FCSTD DOCUMENT  (FreeCAD 0.20R29410 (Git))
Label: step2-sketch-plates-freecad
License: All rights reserved
LicenseURL: http://en.wikipedia.org/wiki/All_rights_reserved
objects: Sketcher::SketchObject×4
note: 4 computed .brp shape members not serialized (recipe doc carries the construction recipe); baked Part::Feature solids carry a one-line shape summary decoded from their .brp

FEATURE [Sketcher::SketchObject] Sketch004  label="bottom-plates"
  FullyConstrained = false
  sketch-geometry (112):
    g0: LineSegment StartX=92.1533 StartY=-3.22906 StartZ=0 EndX=109.153 EndY=-3.22906 EndZ=0
    g1: ArcOfCircle CenterX=109.153 CenterY=-5.22906 CenterZ=0 NormalX=0 NormalY=0 NormalZ=1 AngleXU=0 Radius=2 StartAngle=0 EndAngle=1.5708
    g2: LineSegment StartX=111.153 StartY=-5.22906 StartZ=0 EndX=111.153 EndY=-6.07906 EndZ=0
    g3: ArcOfCircle CenterX=113.153 CenterY=-6.07906 CenterZ=0 NormalX=0 NormalY=0 NormalZ=1 AngleXU=0 Radius=2 StartAngle=3.14159 EndAngle=4.71239
    g4: LineSegment StartX=113.153 StartY=-8.07906 StartZ=0 EndX=128.153 EndY=-8.07906 EndZ=0
    g5: ArcOfCircle CenterX=128.153 CenterY=-10.0791 CenterZ=0 NormalX=0 NormalY=0 NormalZ=1 AngleXU=0 Radius=2 StartAngle=0 EndAngle=1.5708
    g6: LineSegment StartX=130.153 StartY=-10.0791 StartZ=0 EndX=130.153 EndY=-18.0791 EndZ=0
    g7: ArcOfCircle CenterX=132.153 CenterY=-18.0791 CenterZ=0 NormalX=0 NormalY=0 NormalZ=1 AngleXU=0 Radius=2 StartAngle=3.14159 EndAngle=4.71239
    g8: LineSegment StartX=132.153 StartY=-20.0791 StartZ=0 EndX=147.153 EndY=-20.0791 EndZ=0
    g9: ArcOfCircle CenterX=147.153 CenterY=-22.0791 CenterZ=0 NormalX=0 NormalY=0 NormalZ=1 AngleXU=0 Radius=2 StartAngle=0 EndAngle=1.5708
    g10: LineSegment StartX=149.153 StartY=-22.0791 StartZ=0 EndX=149.153 EndY=-77.0791 EndZ=0
    g11: ArcOfCircle CenterX=147.153 CenterY=-77.0791 CenterZ=0 NormalX=0 NormalY=0 NormalZ=1 AngleXU=0 Radius=2 StartAngle=4.71239 EndAngle=6.28319
    g12: LineSegment StartX=147.153 StartY=-79.0791 StartZ=0 EndX=130.153 EndY=-79.0791 EndZ=0
    g13: ArcOfCircle CenterX=130.153 CenterY=-81.0791 CenterZ=0 NormalX=0 NormalY=0 NormalZ=1 AngleXU=0 Radius=2 StartAngle=1.5708 EndAngle=3.14159
    g14: LineSegment StartX=128.153 StartY=-81.0791 StartZ=0 EndX=128.153 EndY=-82.0791 EndZ=0
    g15: ArcOfCircle CenterX=126.653 CenterY=-82.0791 CenterZ=0 NormalX=0 NormalY=0 NormalZ=1 AngleXU=0 Radius=1.5 StartAngle=4.71239 EndAngle=6.28319
    g16: LineSegment StartX=126.653 StartY=-83.5791 StartZ=0 EndX=88.1533 EndY=-83.5791 EndZ=0
    g17: ArcOfCircle CenterX=88.1533 CenterY=-85.5791 CenterZ=0 NormalX=0 NormalY=0 NormalZ=1 AngleXU=0 Radius=2 StartAngle=1.5708 EndAngle=3.14159
    g18: LineSegment StartX=86.1533 StartY=-85.5791 StartZ=0 EndX=86.1533 EndY=-88.5791 EndZ=0
    g19: ArcOfCircle CenterX=84.1533 CenterY=-88.5791 CenterZ=0 NormalX=0 NormalY=0 NormalZ=1 AngleXU=0 Radius=2 StartAngle=4.71239 EndAngle=6.28319
    g20: Circle CenterX=18.6533 CenterY=-59.0791 CenterZ=0 NormalX=0 NormalY=0 NormalZ=-1 AngleXU=0 Radius=1.1
    g21: LineSegment StartX=12.6533 StartY=-75.5791 StartZ=0 EndX=12.6533 EndY=-10.0791 EndZ=0
    g22: ArcOfCircle CenterX=14.6533 CenterY=-10.0791 CenterZ=0 NormalX=0 NormalY=0 NormalZ=1 AngleXU=0 Radius=2 StartAngle=1.5708 EndAngle=3.14159
    g23: LineSegment StartX=14.6533 StartY=-8.07906 StartZ=0 EndX=88.1533 EndY=-8.07906 EndZ=0
    g24: ArcOfCircle CenterX=88.1533 CenterY=-6.07906 CenterZ=0 NormalX=0 NormalY=0 NormalZ=1 AngleXU=0 Radius=2 StartAngle=4.71239 EndAngle=6.28319
    g25: LineSegment StartX=90.1533 StartY=-6.07906 StartZ=0 EndX=90.1533 EndY=-5.22906 EndZ=0
    g26: ArcOfCircle CenterX=92.1533 CenterY=-5.22906 CenterZ=0 NormalX=0 NormalY=0 NormalZ=1 AngleXU=0 Radius=2 StartAngle=1.5708 EndAngle=3.14159
    g27: ArcOfCircle CenterX=26.7587 CenterY=-99.1946 CenterZ=0 NormalX=0 NormalY=0 NormalZ=1 AngleXU=0 Radius=3.4 StartAngle=3.56097 EndAngle=4.80802
    g28: Circle CenterX=50.1533 CenterY=-11.5791 CenterZ=0 NormalX=0 NormalY=0 NormalZ=-1 AngleXU=0 Radius=1.1
    g29: LineSegment StartX=13.6533 StartY=-79.5791 StartZ=0 EndX=23.6533 EndY=-100.579 EndZ=0
    g30: Circle CenterX=50.1533 CenterY=-59.0791 CenterZ=0 NormalX=0 NormalY=0 NormalZ=-1 AngleXU=0 Radius=1.1
    g31: ArcOfCircle CenterX=77.65 CenterY=-201.358 CenterZ=0 NormalX=0 NormalY=0 NormalZ=1 AngleXU=0 Radius=110.97 StartAngle=1.51216 EndAngle=2.04393
    g32: Circle CenterX=129.153 CenterY=-21.0791 CenterZ=0 NormalX=0 NormalY=0 NormalZ=-1 AngleXU=0 Radius=1.1
    g33: ArcOfCircle CenterX=22.8742 CenterY=-75.1488 CenterZ=0 NormalX=0 NormalY=0 NormalZ=1 AngleXU=0 Radius=10.23 StartAngle=3.18366 EndAngle=3.58948
    g34: Circle CenterX=42.1533 CenterY=-85.0791 CenterZ=0 NormalX=0 NormalY=0 NormalZ=-1 AngleXU=0 Radius=1.1
    g35: Circle CenterX=127.653 CenterY=-77.5791 CenterZ=0 NormalX=0 NormalY=0 NormalZ=-1 AngleXU=0 Radius=1.1
    g36: Circle CenterX=50.1533 CenterY=-31.0791 CenterZ=0 NormalX=0 NormalY=0 NormalZ=-1 AngleXU=0 Radius=1.1
    g37: Circle CenterX=18.6533 CenterY=-31.0791 CenterZ=0 NormalX=0 NormalY=0 NormalZ=-1 AngleXU=0 Radius=1.1
    g38: GeomPoint X=18.6533 Y=-80.4791 Z=0
    g39: GeomPoint X=18.6533 Y=-11.5791 Z=0
    g40: LineSegment StartX=20.3854 StartY=-80.4791 StartZ=0 EndX=19.5193 EndY=-78.9791 EndZ=0
    g41: LineSegment StartX=19.5193 StartY=-78.9791 StartZ=0 EndX=17.7873 EndY=-78.9791 EndZ=0
    g42: LineSegment StartX=17.7873 StartY=-78.9791 StartZ=0 EndX=16.9212 EndY=-80.4791 EndZ=0
    g43: LineSegment StartX=16.9212 StartY=-80.4791 StartZ=0 EndX=17.7873 EndY=-81.9791 EndZ=0
    g44: LineSegment StartX=17.7873 StartY=-81.9791 StartZ=0 EndX=19.5193 EndY=-81.9791 EndZ=0
    g45: LineSegment StartX=19.5193 StartY=-81.9791 StartZ=0 EndX=20.3854 EndY=-80.4791 EndZ=0
    g46: Circle CenterX=18.6533 CenterY=-80.4791 CenterZ=0 NormalX=0 NormalY=0 NormalZ=1 AngleXU=0 Radius=1.73205
    g47: LineSegment StartX=20.3854 StartY=-11.5791 StartZ=0 EndX=19.5193 EndY=-10.0791 EndZ=0
    g48: LineSegment StartX=19.5193 StartY=-10.0791 StartZ=0 EndX=17.7873 EndY=-10.0791 EndZ=0
    g49: LineSegment StartX=17.7873 StartY=-10.0791 StartZ=0 EndX=16.9212 EndY=-11.5791 EndZ=0
    g50: LineSegment StartX=16.9212 StartY=-11.5791 StartZ=0 EndX=17.7873 EndY=-13.0791 EndZ=0
    g51: LineSegment StartX=17.7873 StartY=-13.0791 StartZ=0 EndX=19.5193 EndY=-13.0791 EndZ=0
    g52: LineSegment StartX=19.5193 StartY=-13.0791 StartZ=0 EndX=20.3854 EndY=-11.5791 EndZ=0
    g53: Circle CenterX=18.6533 CenterY=-11.5791 CenterZ=0 NormalX=0 NormalY=0 NormalZ=1 AngleXU=0 Radius=1.73205
    g54: LineSegment StartX=-92.1533 StartY=-3.22906 StartZ=0 EndX=-109.153 EndY=-3.22906 EndZ=0
    g55: ArcOfCircle CenterX=-109.153 CenterY=-5.22906 CenterZ=0 NormalX=0 NormalY=0 NormalZ=1 AngleXU=0 Radius=2 StartAngle=1.5708 EndAngle=3.14159
    g56: LineSegment StartX=-111.153 StartY=-5.22906 StartZ=0 EndX=-111.153 EndY=-6.07906 EndZ=0
    g57: ArcOfCircle CenterX=-113.153 CenterY=-6.07906 CenterZ=0 NormalX=0 NormalY=0 NormalZ=1 AngleXU=0 Radius=2 StartAngle=4.71239 EndAngle=6.28319
    g58: LineSegment StartX=-113.153 StartY=-8.07906 StartZ=0 EndX=-128.153 EndY=-8.07906 EndZ=0
    g59: ArcOfCircle CenterX=-128.153 CenterY=-10.0791 CenterZ=0 NormalX=0 NormalY=0 NormalZ=1 AngleXU=0 Radius=2 StartAngle=1.5708 EndAngle=3.14159
    g60: LineSegment StartX=-130.153 StartY=-10.0791 StartZ=0 EndX=-130.153 EndY=-18.0791 EndZ=0
    g61: ArcOfCircle CenterX=-132.153 CenterY=-18.0791 CenterZ=0 NormalX=0 NormalY=0 NormalZ=1 AngleXU=0 Radius=2 StartAngle=4.71239 EndAngle=6.28319
    g62: LineSegment StartX=-132.153 StartY=-20.0791 StartZ=0 EndX=-147.153 EndY=-20.0791 EndZ=0
    g63: ArcOfCircle CenterX=-147.153 CenterY=-22.0791 CenterZ=0 NormalX=0 NormalY=0 NormalZ=1 AngleXU=0 Radius=2 StartAngle=1.5708 EndAngle=3.14159
    g64: LineSegment StartX=-149.153 StartY=-22.0791 StartZ=0 EndX=-149.153 EndY=-77.0791 EndZ=0
    g65: ArcOfCircle CenterX=-147.153 CenterY=-77.0791 CenterZ=0 NormalX=0 NormalY=0 NormalZ=1 AngleXU=0 Radius=2 StartAngle=3.14159 EndAngle=4.71239
    g66: LineSegment StartX=-147.153 StartY=-79.0791 StartZ=0 EndX=-130.153 EndY=-79.0791 EndZ=0
    g67: ArcOfCircle CenterX=-130.153 CenterY=-81.0791 CenterZ=0 NormalX=0 NormalY=0 NormalZ=1 AngleXU=0 Radius=2 StartAngle=0 EndAngle=1.5708
    g68: LineSegment StartX=-128.153 StartY=-81.0791 StartZ=0 EndX=-128.153 EndY=-82.0791 EndZ=0
    g69: ArcOfCircle CenterX=-126.653 CenterY=-82.0791 CenterZ=0 NormalX=0 NormalY=0 NormalZ=1 AngleXU=0 Radius=1.5 StartAngle=3.14159 EndAngle=4.71239
    g70: LineSegment StartX=-126.653 StartY=-83.5791 StartZ=0 EndX=-88.1533 EndY=-83.5791 EndZ=0
    g71: ArcOfCircle CenterX=-88.1533 CenterY=-85.5791 CenterZ=0 NormalX=0 NormalY=0 NormalZ=1 AngleXU=0 Radius=2 StartAngle=0 EndAngle=1.5708
    g72: LineSegment StartX=-86.1533 StartY=-85.5791 StartZ=0 EndX=-86.1533 EndY=-88.5791 EndZ=0
    g73: ArcOfCircle CenterX=-84.1533 CenterY=-88.5791 CenterZ=0 NormalX=0 NormalY=0 NormalZ=1 AngleXU=0 Radius=2 StartAngle=3.14159 EndAngle=4.71239
    g74: Circle CenterX=-18.6533 CenterY=-59.0791 CenterZ=0 NormalX=0 NormalY=0 NormalZ=-1 AngleXU=0 Radius=1.1
    g75: LineSegment StartX=-12.6533 StartY=-75.5791 StartZ=0 EndX=-12.6533 EndY=-10.0791 EndZ=0
    g76: ArcOfCircle CenterX=-14.6533 CenterY=-10.0791 CenterZ=0 NormalX=0 NormalY=0 NormalZ=1 AngleXU=0 Radius=2 StartAngle=0 EndAngle=1.5708
    g77: LineSegment StartX=-14.6533 StartY=-8.07906 StartZ=0 EndX=-88.1533 EndY=-8.07906 EndZ=0
    g78: ArcOfCircle CenterX=-88.1533 CenterY=-6.07906 CenterZ=0 NormalX=0 NormalY=0 NormalZ=1 AngleXU=0 Radius=2 StartAngle=3.14159 EndAngle=4.71239
    g79: LineSegment StartX=-90.1533 StartY=-6.07906 StartZ=0 EndX=-90.1533 EndY=-5.22906 EndZ=0
    g80: ArcOfCircle CenterX=-92.1533 CenterY=-5.22906 CenterZ=0 NormalX=0 NormalY=0 NormalZ=1 AngleXU=0 Radius=2 StartAngle=0 EndAngle=1.5708
    g81: ArcOfCircle CenterX=-26.7587 CenterY=-99.1946 CenterZ=0 NormalX=0 NormalY=0 NormalZ=1 AngleXU=0 Radius=3.4 StartAngle=4.61676 EndAngle=5.8638
    g82: Circle CenterX=-50.1533 CenterY=-11.5791 CenterZ=0 NormalX=0 NormalY=0 NormalZ=-1 AngleXU=0 Radius=1.1
    g83: LineSegment StartX=-13.6533 StartY=-79.5791 StartZ=0 EndX=-23.6533 EndY=-100.579 EndZ=0
    g84: Circle CenterX=-50.1533 CenterY=-59.0791 CenterZ=0 NormalX=0 NormalY=0 NormalZ=-1 AngleXU=0 Radius=1.1
    g85: ArcOfCircle CenterX=-77.65 CenterY=-201.358 CenterZ=0 NormalX=0 NormalY=0 NormalZ=1 AngleXU=0 Radius=110.97 StartAngle=1.09766 EndAngle=1.62943
    g86: Circle CenterX=-129.153 CenterY=-21.0791 CenterZ=0 NormalX=0 NormalY=0 NormalZ=-1 AngleXU=0 Radius=1.1
    g87: ArcOfCircle CenterX=-22.8742 CenterY=-75.1488 CenterZ=0 NormalX=0 NormalY=0 NormalZ=1 AngleXU=0 Radius=10.23 StartAngle=5.8353 EndAngle=6.24112
    g88: Circle CenterX=-42.1533 CenterY=-85.0791 CenterZ=0 NormalX=0 NormalY=0 NormalZ=-1 AngleXU=0 Radius=1.1
    g89: LineSegment StartX=-31.0333 StartY=-19.7091 StartZ=0 EndX=-40.2733 EndY=-19.7091 EndZ=0
    g90: LineSegment StartX=-40.2733 StartY=-19.7091 StartZ=0 EndX=-40.2733 EndY=-28.0791 EndZ=0
    g91: LineSegment StartX=-40.2733 StartY=-28.0791 StartZ=0 EndX=-31.0333 EndY=-28.0791 EndZ=0
    g92: LineSegment StartX=-31.0333 StartY=-28.0791 StartZ=0 EndX=-31.0333 EndY=-19.7091 EndZ=0
    g93: Circle CenterX=-127.653 CenterY=-77.5791 CenterZ=0 NormalX=0 NormalY=0 NormalZ=-1 AngleXU=0 Radius=1.1
    g94: Circle CenterX=-50.1533 CenterY=-31.0791 CenterZ=0 NormalX=0 NormalY=0 NormalZ=-1 AngleXU=0 Radius=1.1
    g95: Circle CenterX=-18.6533 CenterY=-31.0791 CenterZ=0 NormalX=0 NormalY=0 NormalZ=-1 AngleXU=0 Radius=1.1
    g96: GeomPoint X=-18.6533 Y=-80.4791 Z=0
    g97: GeomPoint X=-18.6533 Y=-11.5791 Z=0
    g98: LineSegment StartX=-20.3854 StartY=-80.4791 StartZ=0 EndX=-19.5193 EndY=-78.9791 EndZ=0
    g99: LineSegment StartX=-19.5193 StartY=-78.9791 StartZ=0 EndX=-17.7873 EndY=-78.9791 EndZ=0
    g100: LineSegment StartX=-17.7873 StartY=-78.9791 StartZ=0 EndX=-16.9212 EndY=-80.4791 EndZ=0
    g101: LineSegment StartX=-16.9212 StartY=-80.4791 StartZ=0 EndX=-17.7873 EndY=-81.9791 EndZ=0
    g102: LineSegment StartX=-17.7873 StartY=-81.9791 StartZ=0 EndX=-19.5193 EndY=-81.9791 EndZ=0
    g103: LineSegment StartX=-19.5193 StartY=-81.9791 StartZ=0 EndX=-20.3854 EndY=-80.4791 EndZ=0
    g104: Circle CenterX=-18.6533 CenterY=-80.4791 CenterZ=0 NormalX=0 NormalY=0 NormalZ=1 AngleXU=0 Radius=1.73205
    g105: LineSegment StartX=-20.3854 StartY=-11.5791 StartZ=0 EndX=-19.5193 EndY=-10.0791 EndZ=0
    g106: LineSegment StartX=-19.5193 StartY=-10.0791 StartZ=0 EndX=-17.7873 EndY=-10.0791 EndZ=0
    g107: LineSegment StartX=-17.7873 StartY=-10.0791 StartZ=0 EndX=-16.9212 EndY=-11.5791 EndZ=0
    g108: LineSegment StartX=-16.9212 StartY=-11.5791 StartZ=0 EndX=-17.7873 EndY=-13.0791 EndZ=0
    g109: LineSegment StartX=-17.7873 StartY=-13.0791 StartZ=0 EndX=-19.5193 EndY=-13.0791 EndZ=0
    g110: LineSegment StartX=-19.5193 StartY=-13.0791 StartZ=0 EndX=-20.3854 EndY=-11.5791 EndZ=0
    g111: Circle CenterX=-18.6533 CenterY=-11.5791 CenterZ=0 NormalX=0 NormalY=0 NormalZ=1 AngleXU=0 Radius=1.73205
  constraints (267):
    c: Coincident(g0,g1)
    c: Coincident(g1,g2)
    c: Vertical(g2)
    c: Coincident(g2,g3)
    c: Coincident(g3,g4)
    c: Horizontal(g4)
    c: Coincident(g4,g5)
    c: Coincident(g5,g6)
    c: Vertical(g6)
    c: Coincident(g6,g7)
    c: Coincident(g7,g8)
    c: Horizontal(g8)
    c: Coincident(g9,g10)
    c: Vertical(g10)
    c: Coincident(g10,g11)
    c: Horizontal(g12)
    c: Coincident(g12,g13)
    c: Coincident(g13,g14)
    c: Vertical(g14)
    c: Coincident(g14,g15)
    c: Coincident(g15,g16)
    c: Horizontal(g16)
    c: Coincident(g16,g17)
    c: Coincident(g17,g18)
    c: Vertical(g18)
    c: Coincident(g18,g19)
    c: Vertical(g21)
    c: Coincident(g21,g22)
    c: Horizontal(g23)
    c: Coincident(g23,g24)
    c: Coincident(g24,g25)
    c: Vertical(g25)
    c: Coincident(g25,g26)
    c: Horizontal(g23,g4)
    c: DistanceY(g27,g29) = 21
    c: DistanceY(g21,g21) = 65.5
    c: Radius(g15) = 1.5
    c: Radius(g1) = 2
    c: Equal(g26,g24)
    c: Coincident(g21,g33)
    c: Coincident(g29,g33)
    c: Coincident(g27,g29)
    c: Coincident(g27,g31)
    c: Coincident(g19,g31)
    c: Radius(g31) = 110.97
    c: Coincident(g0,g26)
    c: Coincident(g22,g23)
    c: Vertical(g38,g39)
    c: Coincident(g40,g41)
    c: Coincident(g41,g42)
    c: Coincident(g42,g43)
    c: Coincident(g43,g44)
    c: Coincident(g44,g45)
    c: Coincident(g45,g40)
    c: Equal(g40, g41-g45) x5
    c: PointOnObject(g40,g46)
    c: PointOnObject(g41,g46)
    c: PointOnObject(g42,g46)
    c: PointOnObject(g43,g46)
    c: PointOnObject(g44,g46)
    c: PointOnObject(g45,g46)
    c: Horizontal(g41)
    c: Coincident(g47,g48)
    c: Coincident(g48,g49)
    c: Coincident(g49,g50)
    c: Coincident(g50,g51)
    c: Coincident(g51,g52)
    c: Coincident(g52,g47)
    c: Equal(g47, g48-g52) x5
    c: PointOnObject(g47,g53)
    c: PointOnObject(g48,g53)
    c: PointOnObject(g49,g53)
    c: PointOnObject(g50,g53)
    c: PointOnObject(g51,g53)
    c: PointOnObject(g52,g53)
    c: Distance(g49,g47) = 3
    c: Equal(g41,g52)
    c: Horizontal(g48)
    c: Coincident(g39,g53)
    c: DistanceX(g21,g39) = 6
    c: DistanceY(g39,g22) = 3.5
    c: Coincident(g38,g46)
    c: Radius(g33) = 10.23
    c: Radius(g27) = 3.4
    c: Equal(g19,g17)
    c: DistanceY(g8,g4) = 12
    c: DistanceY(g11,g8) = 59
    c: DistanceY(g15,g12) = 4.5
    c: DistanceY(g29,g21) = 4
    c: DistanceX(g27,g27) = 3.43
    c: Equal(g1,g26)
    c: Equal(g5,g3)
    c: Equal(g3,g24)
    c: Equal(g9,g7)
    c: Equal(g7,g1)
    c: Equal(g17,g11)
    c: Equal(g11,g13)
    c: Equal(g13,g9)
    c: Equal(g22,g26)
    c: Horizontal(g0)
    c: Vertical(g22,g22)
    c: Horizontal(g21,g22)
    c: Vertical(g24,g23)
    c: Horizontal(g24,g24)
    c: Horizontal(g26,g25)
    c: Vertical(g0,g26)
    c: Vertical(g0,g1)
    c: Horizontal(g1,g1)
    c: Horizontal(g2,g3)
    c: Vertical(g3,g3)
    c: Vertical(g4,g5)
    c: Horizontal(g5,g5)
    c: Horizontal(g6,g7)
    c: Vertical(g7,g7)
    c: Vertical(g8,g9)
    c: Horizontal(g9,g9)
    c: Horizontal(g10,g11)
    c: Vertical(g11,g11)
    c: Vertical(g13,g12)
    c: Horizontal(g13,g13)
    c: Horizontal(g14,g15)
    c: Vertical(g15,g15)
    c: Vertical(g16,g17)
    c: Horizontal(g17,g17)
    c: Horizontal(g19,g18)
    c: Vertical(g19,g19)
    c: DistanceY(g27,g27) = 2
    c: DistanceY(g27,g19) = 12
    c: Horizontal(g39,g28)
    c: DistanceX(g39,g28) = 31.5
    c: Vertical(g28,g36)
    c: Vertical(g36,g30)
    c: DistanceY(g36,g28) = 19.5
    c: DistanceY(g30,g36) = 28
    c: DistanceY(g34,g30) = 26
    c: DistanceY(g38,g20) = 21.4
    c: DistanceX(g34,g30) = 8
    c: DistanceY(g32,g7) = 3
    c: DistanceX(g32,g7) = 3
    c: DistanceX(g35,g13) = 2.5
    c: DistanceY(g13,g35) = 3.5
    c: DistanceX(g14,g10) = 21
    c: DistanceX(g27,g18) = 62.5
    c: DistanceX(g18,g14) = 42
    c: Horizontal(g20,g30)
    c: Vertical(g20,g37)
    c: Vertical(g37,g39)
    c: Equal(g28,g36)
    c: Equal(g28,g30)
    c: Equal(g28,g20)
    c: Equal(g28,g37)
    c: Equal(g28,g34)
    c: Diameter(g28) = 2.2
    c: DistanceX(g22,g24) = 73.5
    c: DistanceX(g24,g3) = 25
    c: DistanceX(g3,g5) = 15
    c: DistanceX(g5,g9) = 19
    c: DistanceY(g3,g1) = 0.85
    c: Coincident(g8,g9)
    c: DistanceX(g21,g29) = 1
    c: Horizontal(g37,g36)
    c: Coincident(g12,g11)
    c: Coincident(g54,g55)
    c: Coincident(g55,g56)
    c: Vertical(g56)
    c: Coincident(g56,g57)
    c: Coincident(g57,g58)
    c: Horizontal(g58)
    c: Coincident(g58,g59)
    c: Coincident(g59,g60)
    c: Vertical(g60)
    c: Coincident(g60,g61)
    c: Coincident(g61,g62)
    c: Horizontal(g62)
    c: Coincident(g63,g64)
    c: Vertical(g64)
    c: Coincident(g64,g65)
    c: Horizontal(g66)
    c: Coincident(g66,g67)
    c: Coincident(g67,g68)
    c: Vertical(g68)
    c: Coincident(g68,g69)
    c: Coincident(g69,g70)
    c: Horizontal(g70)
    c: Coincident(g70,g71)
    c: Coincident(g71,g72)
    c: Vertical(g72)
    c: Coincident(g72,g73)
    c: Vertical(g75)
    c: Coincident(g75,g76)
    c: Horizontal(g77)
    c: Coincident(g77,g78)
    c: Coincident(g78,g79)
    c: Vertical(g79)
    c: Coincident(g79,g80)
    c: Horizontal(g89)
    c: Coincident(g89,g90)
    c: Vertical(g90)
    c: Coincident(g90,g91)
    c: Horizontal(g91)
    c: Coincident(g91,g92)
    c: Vertical(g92)
    c: Coincident(g92,g89)
    c: Radius(g69) = 1.5
    c: Radius(g55) = 2
    c: Equal(g80,g78)
    c: Coincident(g75,g87)
    c: Coincident(g83,g87)
    c: Coincident(g81,g83)
    c: Coincident(g81,g85)
    c: Coincident(g73,g85)
    c: Radius(g85) = 110.97
    c: Coincident(g54,g80)
    c: Coincident(g76,g77)
    c: Coincident(g98,g99)
    c: Coincident(g99,g100)
    c: Coincident(g100,g101)
    c: Coincident(g101,g102)
    c: Coincident(g102,g103)
    c: Coincident(g103,g98)
    c: Equal(g98, g99-g103) x5
    c: PointOnObject(g98,g104)
    c: PointOnObject(g99,g104)
    c: PointOnObject(g100,g104)
    c: PointOnObject(g101,g104)
    c: PointOnObject(g102,g104)
    c: PointOnObject(g103,g104)
    c: Horizontal(g99)
    c: Coincident(g105,g106)
    c: Coincident(g106,g107)
    c: Coincident(g107,g108)
    c: Coincident(g108,g109)
    c: Coincident(g109,g110)
    c: Coincident(g110,g105)
    c: Equal(g105, g106-g110) x5
    c: PointOnObject(g105,g111)
    c: PointOnObject(g106,g111)
    c: PointOnObject(g107,g111)
    c: PointOnObject(g108,g111)
    c: PointOnObject(g109,g111)
    c: PointOnObject(g110,g111)
    c: Distance(g107,g105) = 3
    c: Equal(g99,g110)
    c: Horizontal(g106)
    c: Coincident(g97,g111)
    c: Coincident(g96,g104)
    c: Radius(g87) = 10.23
    c: Radius(g81) = 3.4
    c: Equal(g73,g71)
    c: Equal(g55,g80)
    c: Equal(g59,g57)
    c: Equal(g57,g78)
    c: Equal(g63,g61)
    c: Equal(g61,g55)
    c: Equal(g71,g65)
    c: Equal(g65,g67)
    c: Equal(g67,g63)
    c: Equal(g76,g80)
    c: Horizontal(g54)
    c: Equal(g82,g94)
    c: Equal(g82,g84)
    c: Equal(g82,g74)
    c: Equal(g82,g95)
    c: Equal(g82,g88)
    c: Diameter(g82) = 2.2
    c: Coincident(g62,g63)
    c: Coincident(g66,g65)
FEATURE [Sketcher::SketchObject] Sketch005  label="shields"
  FullyConstrained = false
  sketch-geometry (86):
    g0: Circle CenterX=48.0022 CenterY=192.575 CenterZ=0 NormalX=0 NormalY=0 NormalZ=1 AngleXU=0 Radius=1.1
    g1: Circle CenterX=79.5022 CenterY=192.575 CenterZ=0 NormalX=0 NormalY=0 NormalZ=1 AngleXU=0 Radius=1.1
    g2: Circle CenterX=48.0022 CenterY=145.075 CenterZ=0 NormalX=0 NormalY=0 NormalZ=1 AngleXU=0 Radius=1.1
    g3: Circle CenterX=79.5022 CenterY=145.075 CenterZ=0 NormalX=0 NormalY=0 NormalZ=1 AngleXU=0 Radius=1.1
    g4: ArcOfCircle CenterX=44.0022 CenterY=193.575 CenterZ=0 NormalX=0 NormalY=0 NormalZ=1 AngleXU=0 Radius=2 StartAngle=1.5708 EndAngle=3.14159
    g5: LineSegment StartX=44.0022 StartY=195.575 StartZ=0 EndX=80.5022 EndY=195.575 EndZ=0
    g6: ArcOfCircle CenterX=80.5022 CenterY=193.575 CenterZ=0 NormalX=0 NormalY=0 NormalZ=1 AngleXU=0 Radius=2 StartAngle=6e-16 EndAngle=1.5708
    g7: LineSegment StartX=82.5022 StartY=193.575 StartZ=0 EndX=82.5022 EndY=144.075 EndZ=0
    g8: ArcOfCircle CenterX=80.5022 CenterY=144.075 CenterZ=0 NormalX=0 NormalY=0 NormalZ=1 AngleXU=0 Radius=2 StartAngle=4.71239 EndAngle=6.28319
    g9: ArcOfCircle CenterX=44.0022 CenterY=132.075 CenterZ=0 NormalX=0 NormalY=0 NormalZ=1 AngleXU=0 Radius=2 StartAngle=3.14159 EndAngle=4.71239
    g10: LineSegment StartX=42.0022 StartY=132.075 StartZ=0 EndX=42.0022 EndY=193.575 EndZ=0
    g11: GeomPoint X=42.0022 Y=195.575 Z=0
    g12: GeomPoint X=82.5022 Y=142.075 Z=0
    g13: Circle CenterX=74.5022 CenterY=160.575 CenterZ=0 NormalX=0 NormalY=0 NormalZ=1 AngleXU=0 Radius=4
    g14: Circle CenterX=66.5649 CenterY=170.075 CenterZ=0 NormalX=0 NormalY=0 NormalZ=1 AngleXU=0 Radius=1.1
    g15: Circle CenterX=66.5649 CenterY=151.075 CenterZ=0 NormalX=0 NormalY=0 NormalZ=1 AngleXU=0 Radius=1.1
    g16: Circle CenterX=74.5022 CenterY=171.075 CenterZ=0 NormalX=0 NormalY=0 NormalZ=1 AngleXU=0 Radius=1.1
    g17: Circle CenterX=74.5022 CenterY=150.075 CenterZ=0 NormalX=0 NormalY=0 NormalZ=1 AngleXU=0 Radius=1.1
    g18: Circle CenterX=13.2827 CenterY=170.075 CenterZ=0 NormalX=0 NormalY=0 NormalZ=1 AngleXU=0 Radius=1.1
    g19: Circle CenterX=10.0331 CenterY=171.075 CenterZ=0 NormalX=0 NormalY=0 NormalZ=1 AngleXU=0 Radius=1.1
    g20: Circle CenterX=10.0331 CenterY=150.075 CenterZ=0 NormalX=0 NormalY=0 NormalZ=1 AngleXU=0 Radius=1.1
    g21: Circle CenterX=13.2827 CenterY=151.075 CenterZ=0 NormalX=0 NormalY=0 NormalZ=1 AngleXU=0 Radius=1.1
    g22: Circle CenterX=-13.2173 CenterY=192.575 CenterZ=0 NormalX=0 NormalY=0 NormalZ=1 AngleXU=0 Radius=1.1
    g23: Circle CenterX=18.2827 CenterY=192.575 CenterZ=0 NormalX=0 NormalY=0 NormalZ=1 AngleXU=0 Radius=1.1
    g24: Circle CenterX=-13.2173 CenterY=145.075 CenterZ=0 NormalX=0 NormalY=0 NormalZ=1 AngleXU=0 Radius=1.1
    g25: Circle CenterX=18.2827 CenterY=145.075 CenterZ=0 NormalX=0 NormalY=0 NormalZ=1 AngleXU=0 Radius=1.1
    g26: ArcOfCircle CenterX=-17.2173 CenterY=193.575 CenterZ=0 NormalX=0 NormalY=0 NormalZ=1 AngleXU=0 Radius=2 StartAngle=1.5708 EndAngle=3.14159
    g27: LineSegment StartX=-17.2173 StartY=195.575 StartZ=0 EndX=19.2827 EndY=195.575 EndZ=0
    g28: ArcOfCircle CenterX=19.2827 CenterY=193.575 CenterZ=0 NormalX=0 NormalY=0 NormalZ=1 AngleXU=0 Radius=2 StartAngle=3.4e-15 EndAngle=1.5708
    g29: LineSegment StartX=21.2827 StartY=193.575 StartZ=0 EndX=21.2827 EndY=144.075 EndZ=0
    g30: ArcOfCircle CenterX=19.2827 CenterY=144.075 CenterZ=0 NormalX=0 NormalY=0 NormalZ=1 AngleXU=0 Radius=2 StartAngle=4.71239 EndAngle=6.28319
    g31: ArcOfCircle CenterX=-17.2173 CenterY=132.075 CenterZ=0 NormalX=0 NormalY=0 NormalZ=1 AngleXU=0 Radius=2 StartAngle=3.14159 EndAngle=4.71239
    g32: LineSegment StartX=-19.2173 StartY=132.075 StartZ=0 EndX=-19.2173 EndY=193.575 EndZ=0
    g33: GeomPoint X=-19.2173 Y=195.575 Z=0
    g34: GeomPoint X=21.2827 Y=142.075 Z=0
    g35: Circle CenterX=13.2827 CenterY=160.575 CenterZ=0 NormalX=0 NormalY=0 NormalZ=1 AngleXU=0 Radius=4
    g36: Circle CenterX=-67.6669 CenterY=163.075 CenterZ=0 NormalX=0 NormalY=0 NormalZ=1 AngleXU=0 Radius=1.1
    g37: Circle CenterX=-86.7669 CenterY=161.975 CenterZ=0 NormalX=0 NormalY=0 NormalZ=1 AngleXU=0 Radius=1.1
    g38: Circle CenterX=-90.1669 CenterY=192.575 CenterZ=0 NormalX=0 NormalY=0 NormalZ=1 AngleXU=0 Radius=1.1
    g39: Circle CenterX=-58.6669 CenterY=192.575 CenterZ=0 NormalX=0 NormalY=0 NormalZ=1 AngleXU=0 Radius=1.1
    g40: Circle CenterX=-90.1669 CenterY=145.075 CenterZ=0 NormalX=0 NormalY=0 NormalZ=1 AngleXU=0 Radius=1.1
    g41: Circle CenterX=-58.6669 CenterY=145.075 CenterZ=0 NormalX=0 NormalY=0 NormalZ=1 AngleXU=0 Radius=1.1
    g42: ArcOfCircle CenterX=-91.1669 CenterY=193.575 CenterZ=0 NormalX=0 NormalY=0 NormalZ=1 AngleXU=0 Radius=2 StartAngle=1.5708 EndAngle=3.14159
    g43: LineSegment StartX=-91.1669 StartY=195.575 StartZ=0 EndX=-54.6669 EndY=195.575 EndZ=0
    g44: ArcOfCircle CenterX=-54.6669 CenterY=193.575 CenterZ=0 NormalX=0 NormalY=0 NormalZ=1 AngleXU=0 Radius=2 StartAngle=1.8e-15 EndAngle=1.5708
    g45: LineSegment StartX=-52.6669 StartY=193.575 StartZ=0 EndX=-52.6669 EndY=132.075 EndZ=0
    g46: ArcOfCircle CenterX=-54.6669 CenterY=132.075 CenterZ=0 NormalX=0 NormalY=0 NormalZ=1 AngleXU=0 Radius=2 StartAngle=4.71239 EndAngle=6.28319
    g47: ArcOfCircle CenterX=-91.1669 CenterY=144.075 CenterZ=0 NormalX=0 NormalY=0 NormalZ=1 AngleXU=0 Radius=2 StartAngle=3.14159 EndAngle=4.71239
    g48: LineSegment StartX=-93.1669 StartY=144.075 StartZ=0 EndX=-93.1669 EndY=193.575 EndZ=0
    g49: GeomPoint X=-93.1669 Y=195.575 Z=0
    g50: GeomPoint X=-52.6669 Y=130.075 Z=0
    g51: LineSegment StartX=-6.21728 StartY=130.075 StartZ=0 EndX=-17.2173 EndY=130.075 EndZ=0
    g52: LineSegment StartX=19.2827 StartY=142.075 StartZ=0 EndX=-2.21728 EndY=142.075 EndZ=0
    g53: LineSegment StartX=-4.21728 StartY=140.075 StartZ=0 EndX=-4.21728 EndY=132.075 EndZ=0
    g54: ArcOfCircle CenterX=-6.21728 CenterY=132.075 CenterZ=0 NormalX=0 NormalY=0 NormalZ=1 AngleXU=0 Radius=2 StartAngle=4.71239 EndAngle=6.28319
    g55: ArcOfCircle CenterX=-2.21728 CenterY=140.075 CenterZ=0 NormalX=0 NormalY=0 NormalZ=1 AngleXU=0 Radius=2 StartAngle=1.5708 EndAngle=3.14159
    g56: LineSegment StartX=55.0022 StartY=130.075 StartZ=0 EndX=44.0022 EndY=130.075 EndZ=0
    g57: LineSegment StartX=80.5022 StartY=142.075 StartZ=0 EndX=59.0022 EndY=142.075 EndZ=0
    g58: LineSegment StartX=57.0022 StartY=140.075 StartZ=0 EndX=57.0022 EndY=132.075 EndZ=0
    g59: ArcOfCircle CenterX=55.0022 CenterY=132.075 CenterZ=0 NormalX=0 NormalY=0 NormalZ=1 AngleXU=0 Radius=2 StartAngle=4.71239 EndAngle=6.28319
    g60: ArcOfCircle CenterX=59.0022 CenterY=140.075 CenterZ=0 NormalX=0 NormalY=0 NormalZ=1 AngleXU=0 Radius=2 StartAngle=1.5708 EndAngle=3.14159
    g61: LineSegment StartX=-69.6669 StartY=142.075 StartZ=0 EndX=-91.1669 EndY=142.075 EndZ=0
    g62: LineSegment StartX=-54.6669 StartY=130.075 StartZ=0 EndX=-65.6669 EndY=130.075 EndZ=0
    g63: LineSegment StartX=-67.6669 StartY=132.075 StartZ=0 EndX=-67.6669 EndY=140.075 EndZ=0
    g64: ArcOfCircle CenterX=-65.6669 CenterY=132.075 CenterZ=0 NormalX=0 NormalY=0 NormalZ=1 AngleXU=0 Radius=2 StartAngle=3.14159 EndAngle=4.71239
    g65: ArcOfCircle CenterX=-69.6669 CenterY=140.075 CenterZ=0 NormalX=0 NormalY=0 NormalZ=1 AngleXU=0 Radius=2 StartAngle=5.01027e-11 EndAngle=1.5708
    g66: Circle CenterX=48.0022 CenterY=173.075 CenterZ=0 NormalX=0 NormalY=0 NormalZ=1 AngleXU=0 Radius=1.1
    g67: Circle CenterX=-58.6669 CenterY=173.075 CenterZ=0 NormalX=0 NormalY=0 NormalZ=1 AngleXU=0 Radius=1.1
    g68: Circle CenterX=-13.2173 CenterY=173.075 CenterZ=0 NormalX=0 NormalY=0 NormalZ=1 AngleXU=0 Radius=1.1
    g69: LineSegment StartX=-67.1669 StartY=148.322 StartZ=0 EndX=-67.1669 EndY=159.827 EndZ=0
    g70: LineSegment StartX=-67.1669 StartY=159.827 StartZ=0 EndX=-70.9145 EndY=163.575 EndZ=0
    g71: LineSegment StartX=-70.9145 StartY=163.575 StartZ=0 EndX=-82.4192 EndY=163.575 EndZ=0
    g72: LineSegment StartX=-82.4192 StartY=163.575 StartZ=0 EndX=-86.1669 EndY=159.827 EndZ=0
    g73: LineSegment StartX=-86.1669 StartY=159.827 StartZ=0 EndX=-86.1669 EndY=148.322 EndZ=0
    g74: LineSegment StartX=-86.1669 StartY=148.322 StartZ=0 EndX=-82.4192 EndY=144.575 EndZ=0
    g75: LineSegment StartX=-82.4192 StartY=144.575 StartZ=0 EndX=-70.9145 EndY=144.575 EndZ=0
    g76: LineSegment StartX=-70.9145 StartY=144.575 StartZ=0 EndX=-67.1669 EndY=148.322 EndZ=0
    g77: LineSegment StartX=-82.4192 StartY=163.575 StartZ=0 EndX=-70.9145 EndY=144.575 EndZ=0
    g78: LineSegment StartX=-82.4192 StartY=144.575 StartZ=0 EndX=-70.9145 EndY=163.575 EndZ=0
    g79: GeomPoint X=-76.6669 Y=154.075 Z=0
    g80: LineSegment StartX=-85.6669 StartY=163.075 StartZ=0 EndX=-85.6669 EndY=145.075 EndZ=0
    g81: LineSegment StartX=-85.6669 StartY=145.075 StartZ=0 EndX=-67.6669 EndY=145.075 EndZ=0
    g82: LineSegment StartX=-67.6669 StartY=145.075 StartZ=0 EndX=-67.6669 EndY=163.075 EndZ=0
    g83: LineSegment StartX=-67.6669 StartY=163.075 StartZ=0 EndX=-85.6669 EndY=163.075 EndZ=0
    g84: GeomPoint X=-76.6669 Y=154.075 Z=0
    g85: LineSegment StartX=-85.6669 StartY=163.075 StartZ=0 EndX=-88.2969 EndY=163.075 EndZ=0
  constraints (223):
    c: Equal(g0,g1)
    c: Equal(g0,g2)
    c: Equal(g0,g3)
    c: Diameter(g0) = 2.2
    c: Vertical(g0,g2)
    c: Vertical(g1,g3)
    c: Horizontal(g0,g1)
    c: Horizontal(g2,g3)
    c: Tangent(g4,g5) = 1.5708
    c: Tangent(g5,g6) = 1.5708
    c: Tangent(g6,g7) = 1.5708
    c: Tangent(g7,g8) = 1.5708
    c: Tangent(g8,g57) = 1.5708
    c: Tangent(g56,g9) = 1.5708
    c: Tangent(g9,g10) = 1.5708
    c: Tangent(g10,g4) = 1.5708
    c: Horizontal(g5)
    c: Vertical(g7)
    c: Vertical(g10)
    c: Equal(g4,g6)
    c: Equal(g6,g8)
    c: Equal(g8,g9)
    c: PointOnObject(g11,g5)
    c: PointOnObject(g11,g10)
    c: PointOnObject(g12,g7)
    c: DistanceX(g4,g0) = 6
    c: DistanceY(g0,g4) = 3
    c: Radius(g6) = 2
    c: DistanceX(g1,g6) = 3
    c: DistanceX(g13,g6) = 8
    c: Equal(g14,g15)
    c: Vertical(g14,g15)
    c: Distance(g14,g15) = 19
    c: Equal(g16,g17)
    c: Vertical(g17,g16)
    c: Distance(g16,g17) = 21
    c: Equal(g18,g19)
    c: Equal(g18,g20)
    c: Equal(g18,g21)
    c: Diameter(g18) = 2.2
    c: Vertical(g19,g20)
    c: Distance(g19,g20) = 21
    c: Vertical(g18,g21)
    c: Distance(g18,g21) = 19
    c: Distance(g15,g17) = 8
    c: Distance(g14,g16) = 8
    c: Distance(g20,g21) = 3.4
    c: Distance(g19,g18) = 3.4
    c: Equal(g22,g23)
    c: Equal(g22,g24)
    c: Equal(g22,g25)
    c: Equal(g0,g22) = 2.2
    c: Vertical(g22,g24)
    c: Vertical(g23,g25)
    c: Horizontal(g22,g23)
    c: Horizontal(g24,g25)
    c: Distance(g22,g23) = 31.5
    c: Distance(g22,g24) = 47.5
    c: Tangent(g26,g27) = 1.5708
    c: Tangent(g27,g28) = 1.5708
    c: Tangent(g28,g29) = 1.5708
    c: Tangent(g29,g30) = 1.5708
    c: Tangent(g30,g52) = 1.5708
    c: Tangent(g51,g31) = 1.5708
    c: Tangent(g31,g32) = 1.5708
    c: Tangent(g32,g26) = 1.5708
    c: Horizontal(g27)
    c: Vertical(g29)
    c: Vertical(g32)
    c: Equal(g26,g28)
    c: Equal(g28,g30)
    c: Equal(g30,g31)
    c: PointOnObject(g33,g27)
    c: PointOnObject(g33,g32)
    c: PointOnObject(g34,g29)
    c: DistanceX(g26,g22) = 6
    c: DistanceY(g22,g26) = 3
    c: Equal(g6,g28) = 2
    c: DistanceX(g23,g28) = 3
    c: Equal(g13,g35) = 8
    c: DistanceX(g35,g28) = 8
    c: DistanceY(g35,g23) = 32
    c: Symmetric(g16,g17,g13)
    c: Symmetric(g18,g21,g35)
    c: Equal(g18,g36) = 2.2
    c: Equal(g38,g39)
    c: Equal(g38,g40)
    c: Equal(g38,g41)
    c: Vertical(g38,g40)
    c: Vertical(g39,g41)
    c: Horizontal(g38,g39)
    c: Horizontal(g40,g41)
    c: Tangent(g42,g43) = 1.5708
    c: Tangent(g43,g44) = 1.5708
    c: Tangent(g44,g45) = 1.5708
    c: Tangent(g45,g46) = 1.5708
    c: Tangent(g46,g62) = 1.5708
    c: Tangent(g61,g47) = 1.5708
    c: Tangent(g47,g48) = 1.5708
    c: Tangent(g48,g42) = 1.5708
    c: Horizontal(g43)
    c: Vertical(g45)
    c: Vertical(g48)
    c: Equal(g42,g44)
    c: Equal(g44,g46)
    c: PointOnObject(g49,g43)
    c: PointOnObject(g49,g48)
    c: PointOnObject(g50,g45)
    c: DistanceX(g42,g38) = 3
    c: DistanceY(g38,g42) = 3
    c: DistanceX(g39,g44) = 6
    c: Horizontal(g51)
    c: PointOnObject(g34,g52)
    c: Horizontal(g52)
    c: Vertical(g53)
    c: DistanceY(g30,g25) = 3
    c: DistanceY(g31,g24) = 15
    c: Tangent(g51,g54) = 1.5708
    c: Tangent(g53,g54) = 1.5708
    c: Tangent(g52,g55) = -1.5708
    c: Tangent(g53,g55) = -1.5708
    c: Equal(g54,g55)
    c: Equal(g55,g31)
    c: Horizontal(g56)
    c: PointOnObject(g12,g57)
    c: Horizontal(g57)
    c: Vertical(g58)
    c: Tangent(g56,g59) = 1.5708
    c: Tangent(g58,g59) = 1.5708
    c: Tangent(g57,g60) = -1.5708
    c: Tangent(g58,g60) = -1.5708
    c: Equal(g60,g59)
    c: Equal(g59,g9)
    c: DistanceY(g8,g3) = 3
    c: Equal(g14,g16)
    c: Equal(g56,g51)
    c: Equal(g10,g32)
    c: DistanceX(g24,g53) = 9
    c: Equal(g43,g5)
    c: Equal(g5,g27)
    c: Equal(g48,g29)
    c: Horizontal(g61)
    c: Distance(g40,g61) = 3
    c: PointOnObject(g50,g62)
    c: Horizontal(g62)
    c: Vertical(g63)
    c: Tangent(g62,g64) = 1.5708
    c: Tangent(g63,g64) = 1.5708
    c: Tangent(g61,g65) = -1.5708
    c: Tangent(g63,g65) = -1.5708
    c: Equal(g65,g64)
    c: Equal(g64,g31)
    c: Equal(g31,g46)
    c: Equal(g46,g47)
    c: Equal(g51,g62)
    c: Horizontal(g46,g31)
    c: DistanceY(g13,g1) = 32
    c: DistanceY(g2,g0) = 47.5
    c: DistanceY(g46,g41) = 15
    c: Vertical(g66,g2)
    c: Equal(g2,g66)
    c: DistanceY(g66,g0) = 19.5
    c: Equal(g39,g67)
    c: Diameter(g67) = 2.2
    c: Vertical(g67,g39)
    c: DistanceY(g67,g39) = 19.5
    c: Equal(g68,g22)
    c: Vertical(g22,g68)
    c: DistanceY(g68,g22) = 19.5
    c: Equal(g72,g74)
    c: Equal(g74,g76)
    c: Equal(g76,g70)
    c: Coincident(g71,g72)
    c: Coincident(g70,g71)
    c: Coincident(g69,g70)
    c: Coincident(g69,g76)
    c: Coincident(g75,g76)
    c: Coincident(g74,g75)
    c: Coincident(g73,g74)
    c: Coincident(g72,g73)
    c: Equal(g71,g75)
    c: Equal(g75,g73)
    c: Equal(g73,g69)
    c: Horizontal(g71)
    c: Horizontal(g75)
    c: Vertical(g73)
    c: Vertical(g69)
    c: Distance(g72) = 5.3
    c: DistanceY(g75,g70) = 19
    c: Coincident(g77,g71)
    c: Coincident(g77,g75)
    c: Coincident(g78,g74)
    c: Coincident(g78,g70)
    c: PointOnObject(g79,g78)
    c: PointOnObject(g79,g77)
    c: Coincident(g80,g81)
    c: Coincident(g81,g82)
    c: Coincident(g82,g83)
    c: Coincident(g83,g80)
    c: Horizontal(g81)
    c: Horizontal(g83)
    c: Vertical(g80)
    c: Vertical(g82)
    c: Symmetric(g81,g80,g84)
    c: Coincident(g79,g84)
    c: Equal(g82,g83)
    c: DistanceY(g81,g82) = 18
    c: Coincident(g85,g80)
    c: Horizontal(g85)
    c: Equal(g37,g36)
    c: Tangent(g37,g80)
    c: Tangent(g37,g85)
    c: Coincident(g36,g82)
    c: Horizontal(g0,g22)
    c: Angle(g71,g70) = 2.35619
    c: Angle(g69,g76) = 2.35619
    c: Angle(g74,g73) = 2.35619
    c: Angle(g73,g72) = 2.35619  'aa'
    c: Distance(g37,g36) = 19.1316
    c: Distance(g69,g69) = 11.5047
    c: Distance(g85) = 2.63
    c: DistanceX(g47,g73) = 7
    c: DistanceY(g47,g79) = 12
FEATURE [Sketcher::SketchObject] Sketch006  label="top-plates"
  FullyConstrained = false
  sketch-geometry (363):
    g0: LineSegment StartX=-85.8065 StartY=66.6618 StartZ=0 EndX=-99.8065 EndY=66.6618 EndZ=0
    g1: LineSegment StartX=-99.8065 StartY=66.6618 StartZ=0 EndX=-99.8065 EndY=52.6618 EndZ=0
    g2: LineSegment StartX=-99.8065 StartY=52.6618 StartZ=0 EndX=-85.8065 EndY=52.6618 EndZ=0
    g3: LineSegment StartX=-85.8065 StartY=52.6618 StartZ=0 EndX=-85.8065 EndY=66.6618 EndZ=0
    g4: LineSegment StartX=-47.8065 StartY=97.6618 StartZ=0 EndX=-61.8065 EndY=97.6618 EndZ=0
    g5: LineSegment StartX=-61.8065 StartY=97.6618 StartZ=0 EndX=-61.8065 EndY=83.6618 EndZ=0
    g6: LineSegment StartX=-61.8065 StartY=83.6618 StartZ=0 EndX=-47.8065 EndY=83.6618 EndZ=0
    g7: LineSegment StartX=-47.8065 StartY=83.6618 StartZ=0 EndX=-47.8065 EndY=97.6618 EndZ=0
    g8: LineSegment StartX=-66.8065 StartY=99.6618 StartZ=0 EndX=-80.8065 EndY=99.6618 EndZ=0
    g9: LineSegment StartX=-80.8065 StartY=99.6618 StartZ=0 EndX=-80.8065 EndY=85.6618 EndZ=0
    g10: LineSegment StartX=-80.8065 StartY=85.6618 StartZ=0 EndX=-66.8065 EndY=85.6618 EndZ=0
    g11: LineSegment StartX=-66.8065 StartY=85.6618 StartZ=0 EndX=-66.8065 EndY=99.6618 EndZ=0
    g12: LineSegment StartX=-47.8065 StartY=59.6618 StartZ=0 EndX=-61.8065 EndY=59.6618 EndZ=0
    g13: LineSegment StartX=-61.8065 StartY=59.6618 StartZ=0 EndX=-61.8065 EndY=45.6618 EndZ=0
    g14: LineSegment StartX=-61.8065 StartY=45.6618 StartZ=0 EndX=-47.8065 EndY=45.6618 EndZ=0
    g15: LineSegment StartX=-47.8065 StartY=45.6618 StartZ=0 EndX=-47.8065 EndY=59.6618 EndZ=0
    g16: LineSegment StartX=-104.806 StartY=80.6618 StartZ=0 EndX=-118.806 EndY=80.6618 EndZ=0
    g17: LineSegment StartX=-118.806 StartY=80.6618 StartZ=0 EndX=-118.806 EndY=66.6618 EndZ=0
    g18: LineSegment StartX=-118.806 StartY=66.6618 StartZ=0 EndX=-104.806 EndY=66.6618 EndZ=0
    g19: LineSegment StartX=-104.806 StartY=66.6618 StartZ=0 EndX=-104.806 EndY=80.6618 EndZ=0
    g20: LineSegment StartX=-123.806 StartY=87.6618 StartZ=0 EndX=-137.806 EndY=87.6618 EndZ=0
    g21: LineSegment StartX=-137.806 StartY=87.6618 StartZ=0 EndX=-137.806 EndY=73.6618 EndZ=0
    g22: LineSegment StartX=-137.806 StartY=73.6618 StartZ=0 EndX=-123.806 EndY=73.6618 EndZ=0
    g23: LineSegment StartX=-123.806 StartY=73.6618 StartZ=0 EndX=-123.806 EndY=87.6618 EndZ=0
    g24: LineSegment StartX=-47.8065 StartY=78.6618 StartZ=0 EndX=-61.8065 EndY=78.6618 EndZ=0
    g25: LineSegment StartX=-61.8065 StartY=78.6618 StartZ=0 EndX=-61.8065 EndY=64.6618 EndZ=0
    g26: LineSegment StartX=-61.8065 StartY=64.6618 StartZ=0 EndX=-47.8065 EndY=64.6618 EndZ=0
    g27: LineSegment StartX=-47.8065 StartY=64.6618 StartZ=0 EndX=-47.8065 EndY=78.6618 EndZ=0
    g28: LineSegment StartX=-123.806 StartY=68.6618 StartZ=0 EndX=-137.806 EndY=68.6618 EndZ=0
    g29: LineSegment StartX=-137.806 StartY=68.6618 StartZ=0 EndX=-137.806 EndY=54.6618 EndZ=0
    g30: LineSegment StartX=-137.806 StartY=54.6618 StartZ=0 EndX=-123.806 EndY=54.6618 EndZ=0
    g31: LineSegment StartX=-123.806 StartY=54.6618 StartZ=0 EndX=-123.806 EndY=68.6618 EndZ=0
    g32: LineSegment StartX=-123.806 StartY=49.6618 StartZ=0 EndX=-137.806 EndY=49.6618 EndZ=0
    g33: LineSegment StartX=-137.806 StartY=49.6618 StartZ=0 EndX=-137.806 EndY=35.6618 EndZ=0
    g34: LineSegment StartX=-137.806 StartY=35.6618 StartZ=0 EndX=-123.806 EndY=35.6618 EndZ=0
    g35: LineSegment StartX=-123.806 StartY=35.6618 StartZ=0 EndX=-123.806 EndY=49.6618 EndZ=0
    g36: LineSegment StartX=-66.8065 StartY=61.6618 StartZ=0 EndX=-80.8065 EndY=61.6618 EndZ=0
    g37: LineSegment StartX=-80.8065 StartY=61.6618 StartZ=0 EndX=-80.8065 EndY=47.6618 EndZ=0
    g38: LineSegment StartX=-80.8065 StartY=47.6618 StartZ=0 EndX=-66.8065 EndY=47.6618 EndZ=0
    g39: LineSegment StartX=-66.8065 StartY=47.6618 StartZ=0 EndX=-66.8065 EndY=61.6618 EndZ=0
    g40: LineSegment StartX=-37.1975 StartY=34.8398 StartZ=0 EndX=-50.9845 EndY=37.2708 EndZ=0
    g41: LineSegment StartX=-50.9845 StartY=37.2708 StartZ=0 EndX=-53.4155 EndY=23.4838 EndZ=0
    g42: LineSegment StartX=-53.4155 StartY=23.4838 StartZ=0 EndX=-39.6285 EndY=21.0528 EndZ=0
    g43: LineSegment StartX=-39.6285 StartY=21.0528 StartZ=0 EndX=-37.1975 EndY=34.8398 EndZ=0
    g44: LineSegment StartX=-104.806 StartY=99.6618 StartZ=0 EndX=-118.806 EndY=99.6618 EndZ=0
    g45: LineSegment StartX=-118.806 StartY=99.6618 StartZ=0 EndX=-118.806 EndY=85.6618 EndZ=0
    g46: LineSegment StartX=-118.806 StartY=85.6618 StartZ=0 EndX=-104.806 EndY=85.6618 EndZ=0
    g47: LineSegment StartX=-104.806 StartY=85.6618 StartZ=0 EndX=-104.806 EndY=99.6618 EndZ=0
    g48: LineSegment StartX=-14.004 StartY=26.0478 StartZ=0 EndX=-26.6923 EndY=31.9638 EndZ=0
    g49: LineSegment StartX=-26.6923 StartY=31.9638 StartZ=0 EndX=-32.6085 EndY=19.2758 EndZ=0
    g50: LineSegment StartX=-32.6085 StartY=19.2758 StartZ=0 EndX=-19.9207 EndY=13.3598 EndZ=0
    g51: LineSegment StartX=-19.9207 StartY=13.3598 StartZ=0 EndX=-14.004 EndY=26.0478 EndZ=0
    g52: LineSegment StartX=-104.806 StartY=61.6618 StartZ=0 EndX=-118.806 EndY=61.6618 EndZ=0
    g53: LineSegment StartX=-118.806 StartY=61.6618 StartZ=0 EndX=-118.806 EndY=47.6618 EndZ=0
    g54: LineSegment StartX=-118.806 StartY=47.6618 StartZ=0 EndX=-104.806 EndY=47.6618 EndZ=0
    g55: LineSegment StartX=-104.806 StartY=47.6618 StartZ=0 EndX=-104.806 EndY=61.6618 EndZ=0
    g56: LineSegment StartX=-66.8065 StartY=66.6618 StartZ=0 EndX=-66.8065 EndY=80.6618 EndZ=0
    g57: LineSegment StartX=-66.8065 StartY=80.6618 StartZ=0 EndX=-80.8065 EndY=80.6618 EndZ=0
    g58: LineSegment StartX=-80.8065 StartY=80.6618 StartZ=0 EndX=-80.8065 EndY=66.6618 EndZ=0
    g59: LineSegment StartX=-80.8065 StartY=66.6618 StartZ=0 EndX=-66.8065 EndY=66.6618 EndZ=0
    g60: LineSegment StartX=-60.8065 StartY=38.1618 StartZ=0 EndX=-74.8065 EndY=38.1618 EndZ=0
    g61: LineSegment StartX=-74.8065 StartY=38.1618 StartZ=0 EndX=-74.8065 EndY=24.1618 EndZ=0
    g62: LineSegment StartX=-74.8065 StartY=24.1618 StartZ=0 EndX=-60.8065 EndY=24.1618 EndZ=0
    g63: LineSegment StartX=-60.8065 StartY=24.1618 StartZ=0 EndX=-60.8065 EndY=38.1618 EndZ=0
    g64: LineSegment StartX=-85.8065 StartY=85.6618 StartZ=0 EndX=-99.8065 EndY=85.6618 EndZ=0
    g65: LineSegment StartX=-99.8065 StartY=85.6618 StartZ=0 EndX=-99.8065 EndY=71.6618 EndZ=0
    g66: LineSegment StartX=-99.8065 StartY=71.6618 StartZ=0 EndX=-85.8065 EndY=71.6618 EndZ=0
    g67: LineSegment StartX=-85.8065 StartY=71.6618 StartZ=0 EndX=-85.8065 EndY=85.6618 EndZ=0
    g68: LineSegment StartX=-85.8065 StartY=104.662 StartZ=0 EndX=-99.8065 EndY=104.662 EndZ=0
    g69: LineSegment StartX=-99.8065 StartY=104.662 StartZ=0 EndX=-99.8065 EndY=90.6618 EndZ=0
    g70: LineSegment StartX=-99.8065 StartY=90.6618 StartZ=0 EndX=-85.8065 EndY=90.6618 EndZ=0
    g71: LineSegment StartX=-85.8065 StartY=90.6618 StartZ=0 EndX=-85.8065 EndY=104.662 EndZ=0
    g72: LineSegment StartX=-15.8065 StartY=10.6618 StartZ=0 EndX=-6.57107 EndY=30.0562 EndZ=0
    g73: ArcOfCircle CenterX=-8.37679 CenterY=30.916 CenterZ=0 NormalX=0 NormalY=0 NormalZ=1 AngleXU=0 Radius=2 StartAngle=5.83877 EndAngle=7.30333
    g74: ArcOfCircle CenterX=-50.6965 CenterY=-38.0083 CenterZ=0 NormalX=0 NormalY=0 NormalZ=1 AngleXU=0 Radius=82.8797 StartAngle=1.02014 EndAngle=1.47771
    g75: ArcOfCircle CenterX=-42.8065 CenterY=46.5039 CenterZ=0 NormalX=0 NormalY=0 NormalZ=1 AngleXU=0 Radius=2 StartAngle=3.14159 EndAngle=4.6193
    g76: LineSegment StartX=-44.8065 StartY=46.5039 StartZ=0 EndX=-44.8065 EndY=74.6618 EndZ=0
    g77: ArcOfCircle CenterX=-42.8065 CenterY=74.6618 CenterZ=0 NormalX=0 NormalY=0 NormalZ=1 AngleXU=0 Radius=2 StartAngle=1.5708 EndAngle=3.14159
    g78: LineSegment StartX=-42.8065 StartY=76.6618 StartZ=0 EndX=-41.8065 EndY=76.6618 EndZ=0
    g79: ArcOfCircle CenterX=-41.8065 CenterY=78.6618 CenterZ=0 NormalX=0 NormalY=0 NormalZ=1 AngleXU=0 Radius=2 StartAngle=4.71239 EndAngle=6.28319
    g80: LineSegment StartX=-39.8065 StartY=78.6618 StartZ=0 EndX=-39.8065 EndY=81.6618 EndZ=0
    g81: ArcOfCircle CenterX=-41.8065 CenterY=81.6618 CenterZ=0 NormalX=0 NormalY=0 NormalZ=1 AngleXU=0 Radius=2 StartAngle=0 EndAngle=1.5708
    g82: LineSegment StartX=-41.8065 StartY=83.6618 StartZ=0 EndX=-42.8065 EndY=83.6618 EndZ=0
    g83: ArcOfCircle CenterX=-42.8065 CenterY=85.6618 CenterZ=0 NormalX=0 NormalY=0 NormalZ=1 AngleXU=0 Radius=2 StartAngle=3.14159 EndAngle=4.71239
    g84: LineSegment StartX=-44.8065 StartY=85.6618 StartZ=0 EndX=-44.8065 EndY=101.162 EndZ=0
    g85: ArcOfCircle CenterX=-46.8065 CenterY=101.162 CenterZ=0 NormalX=0 NormalY=0 NormalZ=1 AngleXU=0 Radius=2 StartAngle=0 EndAngle=1.5708
    g86: LineSegment StartX=-46.8065 StartY=103.162 StartZ=0 EndX=-80.3065 EndY=103.162 EndZ=0
    g87: ArcOfCircle CenterX=-80.3065 CenterY=105.162 CenterZ=0 NormalX=0 NormalY=0 NormalZ=1 AngleXU=0 Radius=2 StartAngle=3.14159 EndAngle=4.71239
    g88: LineSegment StartX=-82.3065 StartY=105.162 StartZ=0 EndX=-82.3065 EndY=106.162 EndZ=0
    g89: ArcOfCircle CenterX=-84.3065 CenterY=106.162 CenterZ=0 NormalX=0 NormalY=0 NormalZ=1 AngleXU=0 Radius=2 StartAngle=0 EndAngle=1.5708
    g90: LineSegment StartX=-84.3065 StartY=108.162 StartZ=0 EndX=-101.306 EndY=108.162 EndZ=0
    g91: ArcOfCircle CenterX=-101.306 CenterY=106.162 CenterZ=0 NormalX=0 NormalY=0 NormalZ=1 AngleXU=0 Radius=2 StartAngle=1.5708 EndAngle=3.14159
    g92: LineSegment StartX=-103.306 StartY=106.162 StartZ=0 EndX=-103.306 EndY=105.162 EndZ=0
    g93: ArcOfCircle CenterX=-105.306 CenterY=105.162 CenterZ=0 NormalX=0 NormalY=0 NormalZ=1 AngleXU=0 Radius=2 StartAngle=4.71239 EndAngle=6.28319
    g94: LineSegment StartX=-105.306 StartY=103.162 StartZ=0 EndX=-120.306 EndY=103.162 EndZ=0
    g95: ArcOfCircle CenterX=-120.306 CenterY=101.162 CenterZ=0 NormalX=0 NormalY=0 NormalZ=1 AngleXU=0 Radius=2 StartAngle=1.5708 EndAngle=3.14159
    g96: LineSegment StartX=-122.306 StartY=101.162 StartZ=0 EndX=-122.306 EndY=93.1618 EndZ=0
    g97: ArcOfCircle CenterX=-124.306 CenterY=93.1618 CenterZ=0 NormalX=0 NormalY=0 NormalZ=1 AngleXU=0 Radius=2 StartAngle=4.71239 EndAngle=6.28319
    g98: LineSegment StartX=-124.306 StartY=91.1618 StartZ=0 EndX=-139.306 EndY=91.1618 EndZ=0
    g99: ArcOfCircle CenterX=-139.306 CenterY=89.1618 CenterZ=0 NormalX=0 NormalY=0 NormalZ=1 AngleXU=0 Radius=2 StartAngle=1.5708 EndAngle=3.14159
    g100: LineSegment StartX=-141.306 StartY=89.1618 StartZ=0 EndX=-141.306 EndY=34.1618 EndZ=0
    g101: ArcOfCircle CenterX=-139.306 CenterY=34.1618 CenterZ=0 NormalX=0 NormalY=0 NormalZ=1 AngleXU=0 Radius=2 StartAngle=3.14159 EndAngle=4.71239
    g102: LineSegment StartX=-139.306 StartY=32.1618 StartZ=0 EndX=-122.306 EndY=32.1618 EndZ=0
    g103: ArcOfCircle CenterX=-122.306 CenterY=30.1618 CenterZ=0 NormalX=0 NormalY=0 NormalZ=1 AngleXU=0 Radius=2 StartAngle=0 EndAngle=1.5708
    g104: LineSegment StartX=-120.306 StartY=30.1618 StartZ=0 EndX=-120.306 EndY=29.1618 EndZ=0
    g105: ArcOfCircle CenterX=-118.806 CenterY=29.1618 CenterZ=0 NormalX=0 NormalY=0 NormalZ=1 AngleXU=0 Radius=1.5 StartAngle=3.14159 EndAngle=4.71239
    g106: LineSegment StartX=-118.806 StartY=27.6618 StartZ=0 EndX=-80.3065 EndY=27.6618 EndZ=0
    g107: ArcOfCircle CenterX=-80.3065 CenterY=25.6618 CenterZ=0 NormalX=0 NormalY=0 NormalZ=1 AngleXU=0 Radius=2 StartAngle=0 EndAngle=1.5708
    g108: LineSegment StartX=-78.3065 StartY=25.6618 StartZ=0 EndX=-78.3065 EndY=22.6618 EndZ=0
    g109: ArcOfCircle CenterX=-76.3065 CenterY=22.6618 CenterZ=0 NormalX=0 NormalY=0 NormalZ=1 AngleXU=0 Radius=2 StartAngle=3.14159 EndAngle=4.71239
    g110: Circle CenterX=-10.8065 CenterY=30.7618 CenterZ=0 NormalX=0 NormalY=0 NormalZ=-1 AngleXU=0 Radius=1.1
    g111: ArcOfCircle CenterX=-18.9101 CenterY=12.0428 CenterZ=0 NormalX=0 NormalY=0 NormalZ=1 AngleXU=0 Radius=3.39682 StartAngle=4.61462 EndAngle=5.86464
    g112: ArcOfCircle CenterX=-69.8075 CenterY=-90.1172 CenterZ=0 NormalX=0 NormalY=0 NormalZ=1 AngleXU=0 Radius=110.97 StartAngle=1.09767 EndAngle=1.62939
    g113: Circle CenterX=-121.306 CenterY=90.1618 CenterZ=0 NormalX=0 NormalY=0 NormalZ=-1 AngleXU=0 Radius=1.1
    g114: Circle CenterX=-34.3065 CenterY=26.1618 CenterZ=0 NormalX=0 NormalY=0 NormalZ=-1 AngleXU=0 Radius=1.1
    g115: Circle CenterX=-119.806 CenterY=33.6618 CenterZ=0 NormalX=0 NormalY=0 NormalZ=-1 AngleXU=0 Radius=1.1
    g116: Circle CenterX=-42.3065 CenterY=80.1618 CenterZ=0 NormalX=0 NormalY=0 NormalZ=-1 AngleXU=0 Radius=1.1
    g117: LineSegment StartX=-80.3065 StartY=29.0618 StartZ=0 EndX=-80.3065 EndY=43.2618 EndZ=0
    g118: LineSegment StartX=-80.3065 StartY=43.2618 StartZ=0 EndX=-97.8065 EndY=43.2618 EndZ=0
    g119: LineSegment StartX=-97.8065 StartY=43.2618 StartZ=0 EndX=-97.8065 EndY=29.0618 EndZ=0
    g120: LineSegment StartX=-97.8065 StartY=29.0618 StartZ=0 EndX=-80.3065 EndY=29.0618 EndZ=0
    g121: LineSegment StartX=86.7445 StartY=66.6618 StartZ=0 EndX=100.744 EndY=66.6618 EndZ=0
    g122: LineSegment StartX=100.744 StartY=66.6618 StartZ=0 EndX=100.744 EndY=52.6618 EndZ=0
    g123: LineSegment StartX=100.744 StartY=52.6618 StartZ=0 EndX=86.7445 EndY=52.6618 EndZ=0
    g124: LineSegment StartX=86.7445 StartY=52.6618 StartZ=0 EndX=86.7445 EndY=66.6618 EndZ=0
    g125: LineSegment StartX=48.7445 StartY=97.6618 StartZ=0 EndX=62.7445 EndY=97.6618 EndZ=0
    g126: LineSegment StartX=62.7445 StartY=97.6618 StartZ=0 EndX=62.7445 EndY=83.6618 EndZ=0
    g127: LineSegment StartX=62.7445 StartY=83.6618 StartZ=0 EndX=48.7445 EndY=83.6618 EndZ=0
    g128: LineSegment StartX=48.7445 StartY=83.6618 StartZ=0 EndX=48.7445 EndY=97.6618 EndZ=0
    g129: LineSegment StartX=67.7445 StartY=99.6618 StartZ=0 EndX=81.7445 EndY=99.6618 EndZ=0
    g130: LineSegment StartX=81.7445 StartY=99.6618 StartZ=0 EndX=81.7445 EndY=85.6618 EndZ=0
    g131: LineSegment StartX=81.7445 StartY=85.6618 StartZ=0 EndX=67.7445 EndY=85.6618 EndZ=0
    g132: LineSegment StartX=67.7445 StartY=85.6618 StartZ=0 EndX=67.7445 EndY=99.6618 EndZ=0
    g133: LineSegment StartX=48.7445 StartY=59.6618 StartZ=0 EndX=62.7445 EndY=59.6618 EndZ=0
    g134: LineSegment StartX=62.7445 StartY=59.6618 StartZ=0 EndX=62.7445 EndY=45.6618 EndZ=0
    g135: LineSegment StartX=62.7445 StartY=45.6618 StartZ=0 EndX=48.7445 EndY=45.6618 EndZ=0
    g136: LineSegment StartX=48.7445 StartY=45.6618 StartZ=0 EndX=48.7445 EndY=59.6618 EndZ=0
    g137: LineSegment StartX=105.744 StartY=80.6618 StartZ=0 EndX=119.744 EndY=80.6618 EndZ=0
    g138: LineSegment StartX=119.744 StartY=80.6618 StartZ=0 EndX=119.744 EndY=66.6618 EndZ=0
    g139: LineSegment StartX=119.744 StartY=66.6618 StartZ=0 EndX=105.744 EndY=66.6618 EndZ=0
    g140: LineSegment StartX=105.744 StartY=66.6618 StartZ=0 EndX=105.744 EndY=80.6618 EndZ=0
    g141: LineSegment StartX=124.744 StartY=87.6618 StartZ=0 EndX=138.744 EndY=87.6618 EndZ=0
    g142: LineSegment StartX=138.744 StartY=87.6618 StartZ=0 EndX=138.744 EndY=73.6618 EndZ=0
    g143: LineSegment StartX=138.744 StartY=73.6618 StartZ=0 EndX=124.744 EndY=73.6618 EndZ=0
    g144: LineSegment StartX=124.744 StartY=73.6618 StartZ=0 EndX=124.744 EndY=87.6618 EndZ=0
    g145: LineSegment StartX=48.7445 StartY=78.6618 StartZ=0 EndX=62.7445 EndY=78.6618 EndZ=0
    g146: LineSegment StartX=62.7445 StartY=78.6618 StartZ=0 EndX=62.7445 EndY=64.6618 EndZ=0
    g147: LineSegment StartX=62.7445 StartY=64.6618 StartZ=0 EndX=48.7445 EndY=64.6618 EndZ=0
    g148: LineSegment StartX=48.7445 StartY=64.6618 StartZ=0 EndX=48.7445 EndY=78.6618 EndZ=0
    g149: LineSegment StartX=124.744 StartY=68.6618 StartZ=0 EndX=138.744 EndY=68.6618 EndZ=0
    g150: LineSegment StartX=138.744 StartY=68.6618 StartZ=0 EndX=138.744 EndY=54.6618 EndZ=0
    g151: LineSegment StartX=138.744 StartY=54.6618 StartZ=0 EndX=124.744 EndY=54.6618 EndZ=0
    g152: LineSegment StartX=124.744 StartY=54.6618 StartZ=0 EndX=124.744 EndY=68.6618 EndZ=0
    g153: LineSegment StartX=124.744 StartY=49.6618 StartZ=0 EndX=138.744 EndY=49.6618 EndZ=0
    g154: LineSegment StartX=138.744 StartY=49.6618 StartZ=0 EndX=138.744 EndY=35.6618 EndZ=0
    g155: LineSegment StartX=138.744 StartY=35.6618 StartZ=0 EndX=124.744 EndY=35.6618 EndZ=0
    g156: LineSegment StartX=124.744 StartY=35.6618 StartZ=0 EndX=124.744 EndY=49.6618 EndZ=0
    g157: LineSegment StartX=67.7445 StartY=61.6618 StartZ=0 EndX=81.7445 EndY=61.6618 EndZ=0
    g158: LineSegment StartX=81.7445 StartY=61.6618 StartZ=0 EndX=81.7445 EndY=47.6618 EndZ=0
    g159: LineSegment StartX=81.7445 StartY=47.6618 StartZ=0 EndX=67.7445 EndY=47.6618 EndZ=0
    g160: LineSegment StartX=67.7445 StartY=47.6618 StartZ=0 EndX=67.7445 EndY=61.6618 EndZ=0
    g161: LineSegment StartX=38.1355 StartY=34.8398 StartZ=0 EndX=51.9225 EndY=37.2708 EndZ=0
    g162: LineSegment StartX=51.9225 StartY=37.2708 StartZ=0 EndX=54.3535 EndY=23.4838 EndZ=0
    g163: LineSegment StartX=54.3535 StartY=23.4838 StartZ=0 EndX=40.5665 EndY=21.0528 EndZ=0
    g164: LineSegment StartX=40.5665 StartY=21.0528 StartZ=0 EndX=38.1355 EndY=34.8398 EndZ=0
    g165: LineSegment StartX=105.744 StartY=99.6618 StartZ=0 EndX=119.744 EndY=99.6618 EndZ=0
    g166: LineSegment StartX=119.744 StartY=99.6618 StartZ=0 EndX=119.744 EndY=85.6618 EndZ=0
    g167: LineSegment StartX=119.744 StartY=85.6618 StartZ=0 EndX=105.744 EndY=85.6618 EndZ=0
    g168: LineSegment StartX=105.744 StartY=85.6618 StartZ=0 EndX=105.744 EndY=99.6618 EndZ=0
    g169: LineSegment StartX=14.942 StartY=26.0478 StartZ=0 EndX=27.6303 EndY=31.9638 EndZ=0
    g170: LineSegment StartX=27.6303 StartY=31.9638 StartZ=0 EndX=33.5465 EndY=19.2758 EndZ=0
    g171: LineSegment StartX=33.5465 StartY=19.2758 StartZ=0 EndX=20.8587 EndY=13.3598 EndZ=0
    g172: LineSegment StartX=20.8587 StartY=13.3598 StartZ=0 EndX=14.942 EndY=26.0478 EndZ=0
    g173: LineSegment StartX=105.744 StartY=61.6618 StartZ=0 EndX=119.744 EndY=61.6618 EndZ=0
    g174: LineSegment StartX=119.744 StartY=61.6618 StartZ=0 EndX=119.744 EndY=47.6618 EndZ=0
    g175: LineSegment StartX=119.744 StartY=47.6618 StartZ=0 EndX=105.744 EndY=47.6618 EndZ=0
    g176: LineSegment StartX=105.744 StartY=47.6618 StartZ=0 EndX=105.744 EndY=61.6618 EndZ=0
    g177: LineSegment StartX=67.7445 StartY=66.6618 StartZ=0 EndX=67.7445 EndY=80.6618 EndZ=0
    g178: LineSegment StartX=67.7445 StartY=80.6618 StartZ=0 EndX=81.7445 EndY=80.6618 EndZ=0
    g179: LineSegment StartX=81.7445 StartY=80.6618 StartZ=0 EndX=81.7445 EndY=66.6618 EndZ=0
    g180: LineSegment StartX=81.7445 StartY=66.6618 StartZ=0 EndX=67.7445 EndY=66.6618 EndZ=0
    g181: LineSegment StartX=61.7445 StartY=38.1618 StartZ=0 EndX=75.7445 EndY=38.1618 EndZ=0
    g182: LineSegment StartX=75.7445 StartY=38.1618 StartZ=0 EndX=75.7445 EndY=24.1618 EndZ=0
    g183: LineSegment StartX=75.7445 StartY=24.1618 StartZ=0 EndX=61.7445 EndY=24.1618 EndZ=0
    g184: LineSegment StartX=61.7445 StartY=24.1618 StartZ=0 EndX=61.7445 EndY=38.1618 EndZ=0
    g185: LineSegment StartX=86.7445 StartY=85.6618 StartZ=0 EndX=100.744 EndY=85.6618 EndZ=0
    g186: LineSegment StartX=100.744 StartY=85.6618 StartZ=0 EndX=100.744 EndY=71.6618 EndZ=0
    g187: LineSegment StartX=100.744 StartY=71.6618 StartZ=0 EndX=86.7445 EndY=71.6618 EndZ=0
    g188: LineSegment StartX=86.7445 StartY=71.6618 StartZ=0 EndX=86.7445 EndY=85.6618 EndZ=0
    g189: LineSegment StartX=86.7445 StartY=104.662 StartZ=0 EndX=100.744 EndY=104.662 EndZ=0
    g190: LineSegment StartX=100.744 StartY=104.662 StartZ=0 EndX=100.744 EndY=90.6618 EndZ=0
    g191: LineSegment StartX=100.744 StartY=90.6618 StartZ=0 EndX=86.7445 EndY=90.6618 EndZ=0
    g192: LineSegment StartX=86.7445 StartY=90.6618 StartZ=0 EndX=86.7445 EndY=104.662 EndZ=0
    g193: LineSegment StartX=16.7445 StartY=10.6618 StartZ=0 EndX=7.5091 EndY=30.0562 EndZ=0
    g194: ArcOfCircle CenterX=9.31482 CenterY=30.916 CenterZ=0 NormalX=0 NormalY=0 NormalZ=1 AngleXU=0 Radius=2 StartAngle=2.12145 EndAngle=3.58601
    g195: ArcOfCircle CenterX=51.6345 CenterY=-38.0083 CenterZ=0 NormalX=0 NormalY=0 NormalZ=1 AngleXU=0 Radius=82.8797 StartAngle=1.66389 EndAngle=2.12145
    g196: ArcOfCircle CenterX=43.7445 CenterY=46.5039 CenterZ=0 NormalX=0 NormalY=0 NormalZ=1 AngleXU=0 Radius=2 StartAngle=4.80548 EndAngle=6.28319
    g197: LineSegment StartX=45.7445 StartY=46.5039 StartZ=0 EndX=45.7445 EndY=74.6618 EndZ=0
    g198: ArcOfCircle CenterX=43.7445 CenterY=74.6618 CenterZ=0 NormalX=0 NormalY=0 NormalZ=1 AngleXU=0 Radius=2 StartAngle=0 EndAngle=1.5708
    g199: LineSegment StartX=43.7445 StartY=76.6618 StartZ=0 EndX=42.7445 EndY=76.6618 EndZ=0
    g200: ArcOfCircle CenterX=42.7445 CenterY=78.6618 CenterZ=0 NormalX=0 NormalY=0 NormalZ=1 AngleXU=0 Radius=2 StartAngle=3.14159 EndAngle=4.71239
    g201: LineSegment StartX=40.7445 StartY=78.6618 StartZ=0 EndX=40.7445 EndY=81.6618 EndZ=0
    g202: ArcOfCircle CenterX=42.7445 CenterY=81.6618 CenterZ=0 NormalX=0 NormalY=0 NormalZ=1 AngleXU=0 Radius=2 StartAngle=1.5708 EndAngle=3.14159
    g203: LineSegment StartX=42.7445 StartY=83.6618 StartZ=0 EndX=43.7445 EndY=83.6618 EndZ=0
    g204: ArcOfCircle CenterX=43.7445 CenterY=85.6618 CenterZ=0 NormalX=0 NormalY=0 NormalZ=1 AngleXU=0 Radius=2 StartAngle=4.71239 EndAngle=6.28319
    g205: LineSegment StartX=45.7445 StartY=85.6618 StartZ=0 EndX=45.7445 EndY=101.162 EndZ=0
    g206: ArcOfCircle CenterX=47.7445 CenterY=101.162 CenterZ=0 NormalX=0 NormalY=0 NormalZ=1 AngleXU=0 Radius=2 StartAngle=1.5708 EndAngle=3.14159
    g207: LineSegment StartX=47.7445 StartY=103.162 StartZ=0 EndX=81.2445 EndY=103.162 EndZ=0
    g208: ArcOfCircle CenterX=81.2445 CenterY=105.162 CenterZ=0 NormalX=0 NormalY=0 NormalZ=1 AngleXU=0 Radius=2 StartAngle=4.71239 EndAngle=6.28319
    g209: LineSegment StartX=83.2445 StartY=105.162 StartZ=0 EndX=83.2445 EndY=106.162 EndZ=0
    g210: ArcOfCircle CenterX=85.2445 CenterY=106.162 CenterZ=0 NormalX=0 NormalY=0 NormalZ=1 AngleXU=0 Radius=2 StartAngle=1.5708 EndAngle=3.14159
    g211: LineSegment StartX=85.2445 StartY=108.162 StartZ=0 EndX=102.244 EndY=108.162 EndZ=0
    g212: ArcOfCircle CenterX=102.244 CenterY=106.162 CenterZ=0 NormalX=0 NormalY=0 NormalZ=1 AngleXU=0 Radius=2 StartAngle=0 EndAngle=1.5708
    g213: LineSegment StartX=104.244 StartY=106.162 StartZ=0 EndX=104.244 EndY=105.162 EndZ=0
    g214: ArcOfCircle CenterX=106.244 CenterY=105.162 CenterZ=0 NormalX=0 NormalY=0 NormalZ=1 AngleXU=0 Radius=2 StartAngle=3.14159 EndAngle=4.71239
    g215: LineSegment StartX=106.244 StartY=103.162 StartZ=0 EndX=121.244 EndY=103.162 EndZ=0
    g216: ArcOfCircle CenterX=121.244 CenterY=101.162 CenterZ=0 NormalX=0 NormalY=0 NormalZ=1 AngleXU=0 Radius=2 StartAngle=0 EndAngle=1.5708
    g217: LineSegment StartX=123.244 StartY=101.162 StartZ=0 EndX=123.244 EndY=93.1618 EndZ=0
    g218: ArcOfCircle CenterX=125.244 CenterY=93.1618 CenterZ=0 NormalX=0 NormalY=0 NormalZ=1 AngleXU=0 Radius=2 StartAngle=3.14159 EndAngle=4.71239
    g219: LineSegment StartX=125.244 StartY=91.1618 StartZ=0 EndX=140.244 EndY=91.1618 EndZ=0
    g220: ArcOfCircle CenterX=140.244 CenterY=89.1618 CenterZ=0 NormalX=0 NormalY=0 NormalZ=1 AngleXU=0 Radius=2 StartAngle=0 EndAngle=1.5708
    g221: LineSegment StartX=142.244 StartY=89.1618 StartZ=0 EndX=142.244 EndY=34.1618 EndZ=0
    g222: ArcOfCircle CenterX=140.244 CenterY=34.1618 CenterZ=0 NormalX=0 NormalY=0 NormalZ=1 AngleXU=0 Radius=2 StartAngle=4.71239 EndAngle=6.28319
    g223: LineSegment StartX=140.244 StartY=32.1618 StartZ=0 EndX=123.244 EndY=32.1618 EndZ=0
    g224: ArcOfCircle CenterX=123.244 CenterY=30.1618 CenterZ=0 NormalX=0 NormalY=0 NormalZ=1 AngleXU=0 Radius=2 StartAngle=1.5708 EndAngle=3.14159
    g225: LineSegment StartX=121.244 StartY=30.1618 StartZ=0 EndX=121.244 EndY=29.1618 EndZ=0
    g226: ArcOfCircle CenterX=119.744 CenterY=29.1618 CenterZ=0 NormalX=0 NormalY=0 NormalZ=1 AngleXU=0 Radius=1.5 StartAngle=4.71239 EndAngle=6.28319
    g227: LineSegment StartX=119.744 StartY=27.6618 StartZ=0 EndX=81.2445 EndY=27.6618 EndZ=0
    g228: ArcOfCircle CenterX=81.2445 CenterY=25.6618 CenterZ=0 NormalX=0 NormalY=0 NormalZ=1 AngleXU=0 Radius=2 StartAngle=1.5708 EndAngle=3.14159
    g229: LineSegment StartX=79.2445 StartY=25.6618 StartZ=0 EndX=79.2445 EndY=22.6618 EndZ=0
    g230: ArcOfCircle CenterX=77.2445 CenterY=22.6618 CenterZ=0 NormalX=0 NormalY=0 NormalZ=1 AngleXU=0 Radius=2 StartAngle=4.71239 EndAngle=6.28319
    g231: Circle CenterX=11.7445 CenterY=30.7618 CenterZ=0 NormalX=0 NormalY=0 NormalZ=-1 AngleXU=0 Radius=1.1
    g232: ArcOfCircle CenterX=19.8481 CenterY=12.0428 CenterZ=0 NormalX=0 NormalY=0 NormalZ=1 AngleXU=0 Radius=3.39682 StartAngle=3.56014 EndAngle=4.81016
    g233: ArcOfCircle CenterX=70.7455 CenterY=-90.1172 CenterZ=0 NormalX=0 NormalY=0 NormalZ=1 AngleXU=0 Radius=110.97 StartAngle=1.5122 EndAngle=2.04392
    g234: Circle CenterX=122.244 CenterY=90.1618 CenterZ=0 NormalX=0 NormalY=0 NormalZ=-1 AngleXU=0 Radius=1.1
    g235: Circle CenterX=35.2445 CenterY=26.1618 CenterZ=0 NormalX=0 NormalY=0 NormalZ=-1 AngleXU=0 Radius=1.1
    g236: Circle CenterX=120.744 CenterY=33.6618 CenterZ=0 NormalX=0 NormalY=0 NormalZ=-1 AngleXU=0 Radius=1.1
    g237: Circle CenterX=43.2445 CenterY=80.1618 CenterZ=0 NormalX=0 NormalY=0 NormalZ=-1 AngleXU=0 Radius=1.1
    g238: LineSegment StartX=118.244 StartY=29.0618 StartZ=0 EndX=118.244 EndY=43.2618 EndZ=0
    g239: LineSegment StartX=118.244 StartY=43.2618 StartZ=0 EndX=100.744 EndY=43.2618 EndZ=0
    g240: LineSegment StartX=100.744 StartY=43.2618 StartZ=0 EndX=100.744 EndY=29.0618 EndZ=0
    g241: LineSegment StartX=100.744 StartY=29.0618 StartZ=0 EndX=118.244 EndY=29.0618 EndZ=0
    g242: LineSegment StartX=-85.8065 StartY=66.6618 StartZ=0 EndX=-99.8065 EndY=66.6618 EndZ=0
    g243: LineSegment StartX=-99.8065 StartY=66.6618 StartZ=0 EndX=-99.8065 EndY=52.6618 EndZ=0
    g244: LineSegment StartX=-99.8065 StartY=52.6618 StartZ=0 EndX=-85.8065 EndY=52.6618 EndZ=0
    g245: LineSegment StartX=-85.8065 StartY=52.6618 StartZ=0 EndX=-85.8065 EndY=66.6618 EndZ=0
    g246: LineSegment StartX=-47.8065 StartY=97.6618 StartZ=0 EndX=-61.8065 EndY=97.6618 EndZ=0
    g247: LineSegment StartX=-61.8065 StartY=97.6618 StartZ=0 EndX=-61.8065 EndY=83.6618 EndZ=0
    g248: LineSegment StartX=-61.8065 StartY=83.6618 StartZ=0 EndX=-47.8065 EndY=83.6618 EndZ=0
    g249: LineSegment StartX=-47.8065 StartY=83.6618 StartZ=0 EndX=-47.8065 EndY=97.6618 EndZ=0
    g250: LineSegment StartX=-66.8065 StartY=99.6618 StartZ=0 EndX=-80.8065 EndY=99.6618 EndZ=0
    g251: LineSegment StartX=-80.8065 StartY=99.6618 StartZ=0 EndX=-80.8065 EndY=85.6618 EndZ=0
    g252: LineSegment StartX=-80.8065 StartY=85.6618 StartZ=0 EndX=-66.8065 EndY=85.6618 EndZ=0
    g253: LineSegment StartX=-66.8065 StartY=85.6618 StartZ=0 EndX=-66.8065 EndY=99.6618 EndZ=0
    g254: LineSegment StartX=-47.8065 StartY=59.6618 StartZ=0 EndX=-61.8065 EndY=59.6618 EndZ=0
    g255: LineSegment StartX=-61.8065 StartY=59.6618 StartZ=0 EndX=-61.8065 EndY=45.6618 EndZ=0
    g256: LineSegment StartX=-61.8065 StartY=45.6618 StartZ=0 EndX=-47.8065 EndY=45.6618 EndZ=0
    g257: LineSegment StartX=-47.8065 StartY=45.6618 StartZ=0 EndX=-47.8065 EndY=59.6618 EndZ=0
    g258: LineSegment StartX=-104.806 StartY=80.6618 StartZ=0 EndX=-118.806 EndY=80.6618 EndZ=0
    g259: LineSegment StartX=-118.806 StartY=80.6618 StartZ=0 EndX=-118.806 EndY=66.6618 EndZ=0
    g260: LineSegment StartX=-118.806 StartY=66.6618 StartZ=0 EndX=-104.806 EndY=66.6618 EndZ=0
    g261: LineSegment StartX=-104.806 StartY=66.6618 StartZ=0 EndX=-104.806 EndY=80.6618 EndZ=0
    g262: LineSegment StartX=-123.806 StartY=87.6618 StartZ=0 EndX=-137.806 EndY=87.6618 EndZ=0
    g263: LineSegment StartX=-137.806 StartY=87.6618 StartZ=0 EndX=-137.806 EndY=73.6618 EndZ=0
    g264: LineSegment StartX=-137.806 StartY=73.6618 StartZ=0 EndX=-123.806 EndY=73.6618 EndZ=0
    g265: LineSegment StartX=-123.806 StartY=73.6618 StartZ=0 EndX=-123.806 EndY=87.6618 EndZ=0
    g266: LineSegment StartX=-47.8065 StartY=78.6618 StartZ=0 EndX=-61.8065 EndY=78.6618 EndZ=0
    g267: LineSegment StartX=-61.8065 StartY=78.6618 StartZ=0 EndX=-61.8065 EndY=64.6618 EndZ=0
    g268: LineSegment StartX=-61.8065 StartY=64.6618 StartZ=0 EndX=-47.8065 EndY=64.6618 EndZ=0
    g269: LineSegment StartX=-47.8065 StartY=64.6618 StartZ=0 EndX=-47.8065 EndY=78.6618 EndZ=0
    g270: LineSegment StartX=-123.806 StartY=68.6618 StartZ=0 EndX=-137.806 EndY=68.6618 EndZ=0
    g271: LineSegment StartX=-137.806 StartY=68.6618 StartZ=0 EndX=-137.806 EndY=54.6618 EndZ=0
    g272: LineSegment StartX=-137.806 StartY=54.6618 StartZ=0 EndX=-123.806 EndY=54.6618 EndZ=0
    g273: LineSegment StartX=-123.806 StartY=54.6618 StartZ=0 EndX=-123.806 EndY=68.6618 EndZ=0
    g274: LineSegment StartX=-123.806 StartY=49.6618 StartZ=0 EndX=-137.806 EndY=49.6618 EndZ=0
    g275: LineSegment StartX=-137.806 StartY=49.6618 StartZ=0 EndX=-137.806 EndY=35.6618 EndZ=0
    g276: LineSegment StartX=-137.806 StartY=35.6618 StartZ=0 EndX=-123.806 EndY=35.6618 EndZ=0
    g277: LineSegment StartX=-123.806 StartY=35.6618 StartZ=0 EndX=-123.806 EndY=49.6618 EndZ=0
    g278: LineSegment StartX=-66.8065 StartY=61.6618 StartZ=0 EndX=-80.8065 EndY=61.6618 EndZ=0
    g279: LineSegment StartX=-80.8065 StartY=61.6618 StartZ=0 EndX=-80.8065 EndY=47.6618 EndZ=0
    g280: LineSegment StartX=-80.8065 StartY=47.6618 StartZ=0 EndX=-66.8065 EndY=47.6618 EndZ=0
    g281: LineSegment StartX=-66.8065 StartY=47.6618 StartZ=0 EndX=-66.8065 EndY=61.6618 EndZ=0
    g282: LineSegment StartX=-37.1975 StartY=34.8398 StartZ=0 EndX=-50.9845 EndY=37.2708 EndZ=0
    g283: LineSegment StartX=-50.9845 StartY=37.2708 StartZ=0 EndX=-53.4155 EndY=23.4838 EndZ=0
    g284: LineSegment StartX=-53.4155 StartY=23.4838 StartZ=0 EndX=-39.6285 EndY=21.0528 EndZ=0
    g285: LineSegment StartX=-39.6285 StartY=21.0528 StartZ=0 EndX=-37.1975 EndY=34.8398 EndZ=0
    g286: LineSegment StartX=-104.806 StartY=99.6618 StartZ=0 EndX=-118.806 EndY=99.6618 EndZ=0
    g287: LineSegment StartX=-118.806 StartY=99.6618 StartZ=0 EndX=-118.806 EndY=85.6618 EndZ=0
    g288: LineSegment StartX=-118.806 StartY=85.6618 StartZ=0 EndX=-104.806 EndY=85.6618 EndZ=0
    g289: LineSegment StartX=-104.806 StartY=85.6618 StartZ=0 EndX=-104.806 EndY=99.6618 EndZ=0
    g290: LineSegment StartX=-14.004 StartY=26.0478 StartZ=0 EndX=-26.6923 EndY=31.9638 EndZ=0
    g291: LineSegment StartX=-26.6923 StartY=31.9638 StartZ=0 EndX=-32.6085 EndY=19.2758 EndZ=0
    g292: LineSegment StartX=-32.6085 StartY=19.2758 StartZ=0 EndX=-19.9207 EndY=13.3598 EndZ=0
    g293: LineSegment StartX=-19.9207 StartY=13.3598 StartZ=0 EndX=-14.004 EndY=26.0478 EndZ=0
    g294: LineSegment StartX=-104.806 StartY=61.6618 StartZ=0 EndX=-118.806 EndY=61.6618 EndZ=0
    g295: LineSegment StartX=-118.806 StartY=61.6618 StartZ=0 EndX=-118.806 EndY=47.6618 EndZ=0
    g296: LineSegment StartX=-118.806 StartY=47.6618 StartZ=0 EndX=-104.806 EndY=47.6618 EndZ=0
    g297: LineSegment StartX=-104.806 StartY=47.6618 StartZ=0 EndX=-104.806 EndY=61.6618 EndZ=0
    g298: LineSegment StartX=-66.8065 StartY=66.6618 StartZ=0 EndX=-66.8065 EndY=80.6618 EndZ=0
    g299: LineSegment StartX=-66.8065 StartY=80.6618 StartZ=0 EndX=-80.8065 EndY=80.6618 EndZ=0
    g300: LineSegment StartX=-80.8065 StartY=80.6618 StartZ=0 EndX=-80.8065 EndY=66.6618 EndZ=0
    g301: LineSegment StartX=-80.8065 StartY=66.6618 StartZ=0 EndX=-66.8065 EndY=66.6618 EndZ=0
    g302: LineSegment StartX=-60.8065 StartY=38.1618 StartZ=0 EndX=-74.8065 EndY=38.1618 EndZ=0
    g303: LineSegment StartX=-74.8065 StartY=38.1618 StartZ=0 EndX=-74.8065 EndY=24.1618 EndZ=0
    g304: LineSegment StartX=-74.8065 StartY=24.1618 StartZ=0 EndX=-60.8065 EndY=24.1618 EndZ=0
    g305: LineSegment StartX=-60.8065 StartY=24.1618 StartZ=0 EndX=-60.8065 EndY=38.1618 EndZ=0
    g306: LineSegment StartX=-85.8065 StartY=85.6618 StartZ=0 EndX=-99.8065 EndY=85.6618 EndZ=0
    g307: LineSegment StartX=-99.8065 StartY=85.6618 StartZ=0 EndX=-99.8065 EndY=71.6618 EndZ=0
    g308: LineSegment StartX=-99.8065 StartY=71.6618 StartZ=0 EndX=-85.8065 EndY=71.6618 EndZ=0
    g309: LineSegment StartX=-85.8065 StartY=71.6618 StartZ=0 EndX=-85.8065 EndY=85.6618 EndZ=0
    g310: LineSegment StartX=-85.8065 StartY=104.662 StartZ=0 EndX=-99.8065 EndY=104.662 EndZ=0
    g311: LineSegment StartX=-99.8065 StartY=104.662 StartZ=0 EndX=-99.8065 EndY=90.6618 EndZ=0
    g312: LineSegment StartX=-99.8065 StartY=90.6618 StartZ=0 EndX=-85.8065 EndY=90.6618 EndZ=0
    g313: LineSegment StartX=-85.8065 StartY=90.6618 StartZ=0 EndX=-85.8065 EndY=104.662 EndZ=0
    g314: LineSegment StartX=-15.8065 StartY=10.6618 StartZ=0 EndX=-6.57107 EndY=30.0562 EndZ=0
    g315: ArcOfCircle CenterX=-8.37679 CenterY=30.916 CenterZ=0 NormalX=0 NormalY=0 NormalZ=1 AngleXU=0 Radius=2 StartAngle=5.83877 EndAngle=7.30333
    g316: ArcOfCircle CenterX=-50.6965 CenterY=-38.0083 CenterZ=0 NormalX=0 NormalY=0 NormalZ=1 AngleXU=0 Radius=82.8797 StartAngle=1.02014 EndAngle=1.47771
    g317: ArcOfCircle CenterX=-42.8065 CenterY=46.5039 CenterZ=0 NormalX=0 NormalY=0 NormalZ=1 AngleXU=0 Radius=2 StartAngle=3.14159 EndAngle=4.6193
    g318: LineSegment StartX=-44.8065 StartY=46.5039 StartZ=0 EndX=-44.8065 EndY=74.6618 EndZ=0
    g319: ArcOfCircle CenterX=-42.8065 CenterY=74.6618 CenterZ=0 NormalX=0 NormalY=0 NormalZ=1 AngleXU=0 Radius=2 StartAngle=1.5708 EndAngle=3.14159
    g320: LineSegment StartX=-42.8065 StartY=76.6618 StartZ=0 EndX=-41.8065 EndY=76.6618 EndZ=0
    g321: ArcOfCircle CenterX=-41.8065 CenterY=78.6618 CenterZ=0 NormalX=0 NormalY=0 NormalZ=1 AngleXU=0 Radius=2 StartAngle=4.71239 EndAngle=6.28319
    g322: LineSegment StartX=-39.8065 StartY=78.6618 StartZ=0 EndX=-39.8065 EndY=81.6618 EndZ=0
    g323: ArcOfCircle CenterX=-41.8065 CenterY=81.6618 CenterZ=0 NormalX=0 NormalY=0 NormalZ=1 AngleXU=0 Radius=2 StartAngle=0 EndAngle=1.5708
    g324: LineSegment StartX=-41.8065 StartY=83.6618 StartZ=0 EndX=-42.8065 EndY=83.6618 EndZ=0
    g325: ArcOfCircle CenterX=-42.8065 CenterY=85.6618 CenterZ=0 NormalX=0 NormalY=0 NormalZ=1 AngleXU=0 Radius=2 StartAngle=3.14159 EndAngle=4.71239
    g326: LineSegment StartX=-44.8065 StartY=85.6618 StartZ=0 EndX=-44.8065 EndY=101.162 EndZ=0
    g327: ArcOfCircle CenterX=-46.8065 CenterY=101.162 CenterZ=0 NormalX=0 NormalY=0 NormalZ=1 AngleXU=0 Radius=2 StartAngle=0 EndAngle=1.5708
    g328: LineSegment StartX=-46.8065 StartY=103.162 StartZ=0 EndX=-80.3065 EndY=103.162 EndZ=0
    g329: ArcOfCircle CenterX=-80.3065 CenterY=105.162 CenterZ=0 NormalX=0 NormalY=0 NormalZ=1 AngleXU=0 Radius=2 StartAngle=3.14159 EndAngle=4.71239
    g330: LineSegment StartX=-82.3065 StartY=105.162 StartZ=0 EndX=-82.3065 EndY=106.162 EndZ=0
    g331: ArcOfCircle CenterX=-84.3065 CenterY=106.162 CenterZ=0 NormalX=0 NormalY=0 NormalZ=1 AngleXU=0 Radius=2 StartAngle=0 EndAngle=1.5708
    g332: LineSegment StartX=-84.3065 StartY=108.162 StartZ=0 EndX=-101.306 EndY=108.162 EndZ=0
    g333: ArcOfCircle CenterX=-101.306 CenterY=106.162 CenterZ=0 NormalX=0 NormalY=0 NormalZ=1 AngleXU=0 Radius=2 StartAngle=1.5708 EndAngle=3.14159
    g334: LineSegment StartX=-103.306 StartY=106.162 StartZ=0 EndX=-103.306 EndY=105.162 EndZ=0
    g335: ArcOfCircle CenterX=-105.306 CenterY=105.162 CenterZ=0 NormalX=0 NormalY=0 NormalZ=1 AngleXU=0 Radius=2 StartAngle=4.71239 EndAngle=6.28319
    g336: LineSegment StartX=-105.306 StartY=103.162 StartZ=0 EndX=-120.306 EndY=103.162 EndZ=0
    g337: ArcOfCircle CenterX=-120.306 CenterY=101.162 CenterZ=0 NormalX=0 NormalY=0 NormalZ=1 AngleXU=0 Radius=2 StartAngle=1.5708 EndAngle=3.14159
    g338: LineSegment StartX=-122.306 StartY=101.162 StartZ=0 EndX=-122.306 EndY=93.1618 EndZ=0
    g339: ArcOfCircle CenterX=-124.306 CenterY=93.1618 CenterZ=0 NormalX=0 NormalY=0 NormalZ=1 AngleXU=0 Radius=2 StartAngle=4.71239 EndAngle=6.28319
    g340: LineSegment StartX=-124.306 StartY=91.1618 StartZ=0 EndX=-139.306 EndY=91.1618 EndZ=0
    g341: ArcOfCircle CenterX=-139.306 CenterY=89.1618 CenterZ=0 NormalX=0 NormalY=0 NormalZ=1 AngleXU=0 Radius=2 StartAngle=1.5708 EndAngle=3.14159
    g342: LineSegment StartX=-141.306 StartY=89.1618 StartZ=0 EndX=-141.306 EndY=34.1618 EndZ=0
    g343: ArcOfCircle CenterX=-139.306 CenterY=34.1618 CenterZ=0 NormalX=0 NormalY=0 NormalZ=1 AngleXU=0 Radius=2 StartAngle=3.14159 EndAngle=4.71239
    g344: LineSegment StartX=-139.306 StartY=32.1618 StartZ=0 EndX=-122.306 EndY=32.1618 EndZ=0
    g345: ArcOfCircle CenterX=-122.306 CenterY=30.1618 CenterZ=0 NormalX=0 NormalY=0 NormalZ=1 AngleXU=0 Radius=2 StartAngle=0 EndAngle=1.5708
    g346: LineSegment StartX=-120.306 StartY=30.1618 StartZ=0 EndX=-120.306 EndY=29.1618 EndZ=0
    g347: ArcOfCircle CenterX=-118.806 CenterY=29.1618 CenterZ=0 NormalX=0 NormalY=0 NormalZ=1 AngleXU=0 Radius=1.5 StartAngle=3.14159 EndAngle=4.71239
    g348: LineSegment StartX=-118.806 StartY=27.6618 StartZ=0 EndX=-80.3065 EndY=27.6618 EndZ=0
    g349: ArcOfCircle CenterX=-80.3065 CenterY=25.6618 CenterZ=0 NormalX=0 NormalY=0 NormalZ=1 AngleXU=0 Radius=2 StartAngle=0 EndAngle=1.5708
    g350: LineSegment StartX=-78.3065 StartY=25.6618 StartZ=0 EndX=-78.3065 EndY=22.6618 EndZ=0
    g351: ArcOfCircle CenterX=-76.3065 CenterY=22.6618 CenterZ=0 NormalX=0 NormalY=0 NormalZ=1 AngleXU=0 Radius=2 StartAngle=3.14159 EndAngle=4.71239
    g352: Circle CenterX=-10.8065 CenterY=30.7618 CenterZ=0 NormalX=0 NormalY=0 NormalZ=-1 AngleXU=0 Radius=1.1
    g353: ArcOfCircle CenterX=-18.9101 CenterY=12.0428 CenterZ=0 NormalX=0 NormalY=0 NormalZ=1 AngleXU=0 Radius=3.39682 StartAngle=4.61462 EndAngle=5.86464
    g354: ArcOfCircle CenterX=-69.8075 CenterY=-90.1172 CenterZ=0 NormalX=0 NormalY=0 NormalZ=1 AngleXU=0 Radius=110.97 StartAngle=1.09767 EndAngle=1.62939
    g355: Circle CenterX=-121.306 CenterY=90.1618 CenterZ=0 NormalX=0 NormalY=0 NormalZ=-1 AngleXU=0 Radius=1.1
    g356: Circle CenterX=-34.3065 CenterY=26.1618 CenterZ=0 NormalX=0 NormalY=0 NormalZ=-1 AngleXU=0 Radius=1.1
    g357: Circle CenterX=-119.806 CenterY=33.6618 CenterZ=0 NormalX=0 NormalY=0 NormalZ=-1 AngleXU=0 Radius=1.1
    g358: Circle CenterX=-42.3065 CenterY=80.1618 CenterZ=0 NormalX=0 NormalY=0 NormalZ=-1 AngleXU=0 Radius=1.1
    g359: LineSegment StartX=-80.3065 StartY=29.0618 StartZ=0 EndX=-80.3065 EndY=43.2618 EndZ=0
    g360: LineSegment StartX=-80.3065 StartY=43.2618 StartZ=0 EndX=-97.8065 EndY=43.2618 EndZ=0
    g361: LineSegment StartX=-97.8065 StartY=43.2618 StartZ=0 EndX=-97.8065 EndY=29.0618 EndZ=0
    g362: LineSegment StartX=-97.8065 StartY=29.0618 StartZ=0 EndX=-80.3065 EndY=29.0618 EndZ=0
  constraints (594):
    c: Horizontal(g0)
    c: Coincident(g0,g1)
    c: Vertical(g1)
    c: Coincident(g1,g2)
    c: Horizontal(g2)
    c: Coincident(g2,g3)
    c: Vertical(g3)
    c: Coincident(g3,g0)
    c: Horizontal(g4)
    c: Coincident(g4,g5)
    c: Vertical(g5)
    c: Coincident(g5,g6)
    c: Horizontal(g6)
    c: Coincident(g6,g7)
    c: Vertical(g7)
    c: Coincident(g7,g4)
    c: Horizontal(g8)
    c: Coincident(g8,g9)
    c: Vertical(g9)
    c: Coincident(g9,g10)
    c: Horizontal(g10)
    c: Coincident(g10,g11)
    c: Vertical(g11)
    c: Coincident(g11,g8)
    c: Horizontal(g12)
    c: Coincident(g12,g13)
    c: Vertical(g13)
    c: Coincident(g13,g14)
    c: Horizontal(g14)
    c: Coincident(g14,g15)
    c: Vertical(g15)
    c: Coincident(g15,g12)
    c: Horizontal(g16)
    c: Coincident(g16,g17)
    c: Vertical(g17)
    c: Coincident(g17,g18)
    c: Horizontal(g18)
    c: Coincident(g18,g19)
    c: Vertical(g19)
    c: Coincident(g19,g16)
    c: Horizontal(g20)
    c: Coincident(g20,g21)
    c: Vertical(g21)
    c: Coincident(g21,g22)
    c: Horizontal(g22)
    c: Coincident(g22,g23)
    c: Vertical(g23)
    c: Coincident(g23,g20)
    c: Horizontal(g24)
    c: Coincident(g24,g25)
    c: Vertical(g25)
    c: Coincident(g25,g26)
    c: Horizontal(g26)
    c: Coincident(g26,g27)
    c: Vertical(g27)
    c: Coincident(g27,g24)
    c: Horizontal(g28)
    c: Coincident(g28,g29)
    c: Vertical(g29)
    c: Coincident(g29,g30)
    c: Horizontal(g30)
    c: Coincident(g30,g31)
    c: Vertical(g31)
    c: Coincident(g31,g28)
    c: Horizontal(g32)
    c: Coincident(g32,g33)
    c: Vertical(g33)
    c: Coincident(g33,g34)
    c: Horizontal(g34)
    c: Coincident(g34,g35)
    c: Vertical(g35)
    c: Coincident(g35,g32)
    c: Horizontal(g36)
    c: Coincident(g36,g37)
    c: Vertical(g37)
    c: Coincident(g37,g38)
    c: Horizontal(g38)
    c: Coincident(g38,g39)
    c: Vertical(g39)
    c: Coincident(g39,g36)
    c: Coincident(g40,g41)
    c: Coincident(g41,g42)
    c: Coincident(g42,g43)
    c: Coincident(g43,g40)
    c: Horizontal(g44)
    c: Coincident(g44,g45)
    c: Vertical(g45)
    c: Coincident(g45,g46)
    c: Horizontal(g46)
    c: Coincident(g46,g47)
    c: Vertical(g47)
    c: Coincident(g47,g44)
    c: Coincident(g48,g49)
    c: Coincident(g49,g50)
    c: Coincident(g50,g51)
    c: Coincident(g51,g48)
    c: Horizontal(g52)
    c: Coincident(g52,g53)
    c: Vertical(g53)
    c: Coincident(g53,g54)
    c: Horizontal(g54)
    c: Coincident(g54,g55)
    c: Vertical(g55)
    c: Coincident(g55,g52)
    c: Vertical(g56)
    c: Coincident(g56,g57)
    c: Horizontal(g57)
    c: Coincident(g57,g58)
    c: Vertical(g58)
    c: Coincident(g58,g59)
    c: Horizontal(g59)
    c: Coincident(g59,g56)
    c: Horizontal(g60)
    c: Coincident(g60,g61)
    c: Vertical(g61)
    c: Coincident(g61,g62)
    c: Horizontal(g62)
    c: Coincident(g62,g63)
    c: Vertical(g63)
    c: Coincident(g63,g60)
    c: Horizontal(g64)
    c: Coincident(g64,g65)
    c: Vertical(g65)
    c: Coincident(g65,g66)
    c: Horizontal(g66)
    c: Coincident(g66,g67)
    c: Vertical(g67)
    c: Coincident(g67,g64)
    c: Horizontal(g68)
    c: Coincident(g68,g69)
    c: Vertical(g69)
    c: Coincident(g69,g70)
    c: Horizontal(g70)
    c: Coincident(g70,g71)
    c: Vertical(g71)
    c: Coincident(g71,g68)
    c: Coincident(g72,g73)
    c: Coincident(g73,g74)
    c: Coincident(g74,g75)
    c: Coincident(g75,g76)
    c: Vertical(g76)
    c: Coincident(g76,g77)
    c: Coincident(g77,g78)
    c: Horizontal(g78)
    c: Coincident(g78,g79)
    c: Coincident(g79,g80)
    c: Vertical(g80)
    c: Coincident(g80,g81)
    c: Coincident(g81,g82)
    c: Horizontal(g82)
    c: Coincident(g82,g83)
    c: Coincident(g83,g84)
    c: Vertical(g84)
    c: Coincident(g84,g85)
    c: Coincident(g85,g86)
    c: Horizontal(g86)
    c: Coincident(g86,g87)
    c: Coincident(g87,g88)
    c: Vertical(g88)
    c: Coincident(g88,g89)
    c: Coincident(g89,g90)
    c: Horizontal(g90)
    c: Coincident(g90,g91)
    c: Coincident(g91,g92)
    c: Vertical(g92)
    c: Coincident(g92,g93)
    c: Coincident(g93,g94)
    c: Horizontal(g94)
    c: Coincident(g94,g95)
    c: Coincident(g95,g96)
    c: Vertical(g96)
    c: Coincident(g96,g97)
    c: Coincident(g97,g98)
    c: Horizontal(g98)
    c: Coincident(g98,g99)
    c: Coincident(g99,g100)
    c: Vertical(g100)
    c: Coincident(g100,g101)
    c: Coincident(g101,g102)
    c: Horizontal(g102)
    c: Coincident(g102,g103)
    c: Coincident(g103,g104)
    c: Vertical(g104)
    c: Coincident(g104,g105)
    c: Coincident(g105,g106)
    c: Horizontal(g106)
    c: Coincident(g106,g107)
    c: Coincident(g107,g108)
    c: Vertical(g108)
    c: Coincident(g108,g109)
    c: Vertical(g117)
    c: Coincident(g117,g118)
    c: Horizontal(g118)
    c: Coincident(g118,g119)
    c: Vertical(g119)
    c: Coincident(g119,g120)
    c: Horizontal(g120)
    c: Coincident(g120,g117)
    c: Horizontal(g121)
    c: Coincident(g121,g122)
    c: Vertical(g122)
    c: Coincident(g122,g123)
    c: Horizontal(g123)
    c: Coincident(g123,g124)
    c: Vertical(g124)
    c: Coincident(g124,g121)
    c: Horizontal(g125)
    c: Coincident(g125,g126)
    c: Vertical(g126)
    c: Coincident(g126,g127)
    c: Horizontal(g127)
    c: Coincident(g127,g128)
    c: Vertical(g128)
    c: Coincident(g128,g125)
    c: Horizontal(g129)
    c: Coincident(g129,g130)
    c: Vertical(g130)
    c: Coincident(g130,g131)
    c: Horizontal(g131)
    c: Coincident(g131,g132)
    c: Vertical(g132)
    c: Coincident(g132,g129)
    c: Horizontal(g133)
    c: Coincident(g133,g134)
    c: Vertical(g134)
    c: Coincident(g134,g135)
    c: Horizontal(g135)
    c: Coincident(g135,g136)
    c: Vertical(g136)
    c: Coincident(g136,g133)
    c: Horizontal(g137)
    c: Coincident(g137,g138)
    c: Vertical(g138)
    c: Coincident(g138,g139)
    c: Horizontal(g139)
    c: Coincident(g139,g140)
    c: Vertical(g140)
    c: Coincident(g140,g137)
    c: Horizontal(g141)
    c: Coincident(g141,g142)
    c: Vertical(g142)
    c: Coincident(g142,g143)
    c: Horizontal(g143)
    c: Coincident(g143,g144)
    c: Vertical(g144)
    c: Coincident(g144,g141)
    c: Horizontal(g145)
    c: Coincident(g145,g146)
    c: Vertical(g146)
    c: Coincident(g146,g147)
    c: Horizontal(g147)
    c: Coincident(g147,g148)
    c: Vertical(g148)
    c: Coincident(g148,g145)
    c: Horizontal(g149)
    c: Coincident(g149,g150)
    c: Vertical(g150)
    c: Coincident(g150,g151)
    c: Horizontal(g151)
    c: Coincident(g151,g152)
    c: Vertical(g152)
    c: Coincident(g152,g149)
    c: Horizontal(g153)
    c: Coincident(g153,g154)
    c: Vertical(g154)
    c: Coincident(g154,g155)
    c: Horizontal(g155)
    c: Coincident(g155,g156)
    c: Vertical(g156)
    c: Coincident(g156,g153)
    c: Horizontal(g157)
    c: Coincident(g157,g158)
    c: Vertical(g158)
    c: Coincident(g158,g159)
    c: Horizontal(g159)
    c: Coincident(g159,g160)
    c: Vertical(g160)
    c: Coincident(g160,g157)
    c: Coincident(g161,g162)
    c: Coincident(g162,g163)
    c: Coincident(g163,g164)
    c: Coincident(g164,g161)
    c: Horizontal(g165)
    c: Coincident(g165,g166)
    c: Vertical(g166)
    c: Coincident(g166,g167)
    c: Horizontal(g167)
    c: Coincident(g167,g168)
    c: Vertical(g168)
    c: Coincident(g168,g165)
    c: Coincident(g169,g170)
    c: Coincident(g170,g171)
    c: Coincident(g171,g172)
    c: Coincident(g172,g169)
    c: Horizontal(g173)
    c: Coincident(g173,g174)
    c: Vertical(g174)
    c: Coincident(g174,g175)
    c: Horizontal(g175)
    c: Coincident(g175,g176)
    c: Vertical(g176)
    c: Coincident(g176,g173)
    c: Vertical(g177)
    c: Coincident(g177,g178)
    c: Horizontal(g178)
    c: Coincident(g178,g179)
    c: Vertical(g179)
    c: Coincident(g179,g180)
    c: Horizontal(g180)
    c: Coincident(g180,g177)
    c: Horizontal(g181)
    c: Coincident(g181,g182)
    c: Vertical(g182)
    c: Coincident(g182,g183)
    c: Horizontal(g183)
    c: Coincident(g183,g184)
    c: Vertical(g184)
    c: Coincident(g184,g181)
    c: Horizontal(g185)
    c: Coincident(g185,g186)
    c: Vertical(g186)
    c: Coincident(g186,g187)
    c: Horizontal(g187)
    c: Coincident(g187,g188)
    c: Vertical(g188)
    c: Coincident(g188,g185)
    c: Horizontal(g189)
    c: Coincident(g189,g190)
    c: Vertical(g190)
    c: Coincident(g190,g191)
    c: Horizontal(g191)
    c: Coincident(g191,g192)
    c: Vertical(g192)
    c: Coincident(g192,g189)
    c: Coincident(g193,g194)
    c: Coincident(g194,g195)
    c: Coincident(g195,g196)
    c: Coincident(g196,g197)
    c: Vertical(g197)
    c: Coincident(g197,g198)
    c: Coincident(g198,g199)
    c: Horizontal(g199)
    c: Coincident(g199,g200)
    c: Coincident(g200,g201)
    c: Vertical(g201)
    c: Coincident(g201,g202)
    c: Coincident(g202,g203)
    c: Horizontal(g203)
    c: Coincident(g203,g204)
    c: Coincident(g204,g205)
    c: Vertical(g205)
    c: Coincident(g205,g206)
    c: Coincident(g206,g207)
    c: Horizontal(g207)
    c: Coincident(g207,g208)
    c: Coincident(g208,g209)
    c: Vertical(g209)
    c: Coincident(g209,g210)
    c: Coincident(g210,g211)
    c: Horizontal(g211)
    c: Coincident(g211,g212)
    c: Coincident(g212,g213)
    c: Vertical(g213)
    c: Coincident(g213,g214)
    c: Coincident(g214,g215)
    c: Horizontal(g215)
    c: Coincident(g215,g216)
    c: Coincident(g216,g217)
    c: Vertical(g217)
    c: Coincident(g217,g218)
    c: Coincident(g218,g219)
    c: Horizontal(g219)
    c: Coincident(g219,g220)
    c: Coincident(g220,g221)
    c: Vertical(g221)
    c: Coincident(g221,g222)
    c: Coincident(g222,g223)
    c: Horizontal(g223)
    c: Coincident(g223,g224)
    c: Coincident(g224,g225)
    c: Vertical(g225)
    c: Coincident(g225,g226)
    c: Coincident(g226,g227)
    c: Horizontal(g227)
    c: Coincident(g227,g228)
    c: Coincident(g228,g229)
    c: Vertical(g229)
    c: Coincident(g229,g230)
    c: Vertical(g238)
    c: Coincident(g238,g239)
    c: Horizontal(g239)
    c: Coincident(g239,g240)
    c: Vertical(g240)
    c: Coincident(g240,g241)
    c: Horizontal(g241)
    c: Coincident(g241,g238)
    c: Horizontal(g242)
    c: Coincident(g242,g243)
    c: Vertical(g243)
    c: Coincident(g243,g244)
    c: Horizontal(g244)
    c: Coincident(g244,g245)
    c: Vertical(g245)
    c: Coincident(g245,g242)
    c: Horizontal(g246)
    c: Coincident(g246,g247)
    c: Vertical(g247)
    c: Coincident(g247,g248)
    c: Horizontal(g248)
    c: Coincident(g248,g249)
    c: Vertical(g249)
    c: Coincident(g249,g246)
    c: Horizontal(g250)
    c: Coincident(g250,g251)
    c: Vertical(g251)
    c: Coincident(g251,g252)
    c: Horizontal(g252)
    c: Coincident(g252,g253)
    c: Vertical(g253)
    c: Coincident(g253,g250)
    c: Horizontal(g254)
    c: Coincident(g254,g255)
    c: Vertical(g255)
    c: Coincident(g255,g256)
    c: Horizontal(g256)
    c: Coincident(g256,g257)
    c: Vertical(g257)
    c: Coincident(g257,g254)
    c: Horizontal(g258)
    c: Coincident(g258,g259)
    c: Vertical(g259)
    c: Coincident(g259,g260)
    c: Horizontal(g260)
    c: Coincident(g260,g261)
    c: Vertical(g261)
    c: Coincident(g261,g258)
    c: Horizontal(g262)
    c: Coincident(g262,g263)
    c: Vertical(g263)
    c: Coincident(g263,g264)
    c: Horizontal(g264)
    c: Coincident(g264,g265)
    c: Vertical(g265)
    c: Coincident(g265,g262)
    c: Horizontal(g266)
    c: Coincident(g266,g267)
    c: Vertical(g267)
    c: Coincident(g267,g268)
    c: Horizontal(g268)
    c: Coincident(g268,g269)
    c: Vertical(g269)
    c: Coincident(g269,g266)
    c: Horizontal(g270)
    c: Coincident(g270,g271)
    c: Vertical(g271)
    c: Coincident(g271,g272)
    c: Horizontal(g272)
    c: Coincident(g272,g273)
    c: Vertical(g273)
    c: Coincident(g273,g270)
    c: Horizontal(g274)
    c: Coincident(g274,g275)
    c: Vertical(g275)
    c: Coincident(g275,g276)
    c: Horizontal(g276)
    c: Coincident(g276,g277)
    c: Vertical(g277)
    c: Coincident(g277,g274)
    c: Horizontal(g278)
    c: Coincident(g278,g279)
    c: Vertical(g279)
    c: Coincident(g279,g280)
    c: Horizontal(g280)
    c: Coincident(g280,g281)
    c: Vertical(g281)
    c: Coincident(g281,g278)
    c: Coincident(g282,g283)
    c: Coincident(g283,g284)
    c: Coincident(g284,g285)
    c: Coincident(g285,g282)
    c: Horizontal(g286)
    c: Coincident(g286,g287)
    c: Vertical(g287)
    c: Coincident(g287,g288)
    c: Horizontal(g288)
    c: Coincident(g288,g289)
    c: Vertical(g289)
    c: Coincident(g289,g286)
    c: Coincident(g290,g291)
    c: Coincident(g291,g292)
    c: Coincident(g292,g293)
    c: Coincident(g293,g290)
    c: Horizontal(g294)
    c: Coincident(g294,g295)
    c: Vertical(g295)
    c: Coincident(g295,g296)
    c: Horizontal(g296)
    c: Coincident(g296,g297)
    c: Vertical(g297)
    c: Coincident(g297,g294)
    c: Vertical(g298)
    c: Coincident(g298,g299)
    c: Horizontal(g299)
    c: Coincident(g299,g300)
    c: Vertical(g300)
    c: Coincident(g300,g301)
    c: Horizontal(g301)
    c: Coincident(g301,g298)
    c: Horizontal(g302)
    c: Coincident(g302,g303)
    c: Vertical(g303)
    c: Coincident(g303,g304)
    c: Horizontal(g304)
    c: Coincident(g304,g305)
    c: Vertical(g305)
    c: Coincident(g305,g302)
    c: Horizontal(g306)
    c: Coincident(g306,g307)
    c: Vertical(g307)
    c: Coincident(g307,g308)
    c: Horizontal(g308)
    c: Coincident(g308,g309)
    c: Vertical(g309)
    c: Coincident(g309,g306)
    c: Horizontal(g310)
    c: Coincident(g310,g311)
    c: Vertical(g311)
    c: Coincident(g311,g312)
    c: Horizontal(g312)
    c: Coincident(g312,g313)
    c: Vertical(g313)
    c: Coincident(g313,g310)
    c: Coincident(g314,g315)
    c: Coincident(g315,g316)
    c: Coincident(g316,g317)
    c: Coincident(g317,g318)
    c: Vertical(g318)
    c: Coincident(g318,g319)
    c: Coincident(g319,g320)
    c: Horizontal(g320)
    c: Coincident(g320,g321)
    c: Coincident(g321,g322)
    c: Vertical(g322)
    c: Coincident(g322,g323)
    c: Coincident(g323,g324)
    c: Horizontal(g324)
    c: Coincident(g324,g325)
    c: Coincident(g325,g326)
    c: Vertical(g326)
    c: Coincident(g326,g327)
    c: Coincident(g327,g328)
    c: Horizontal(g328)
    c: Coincident(g328,g329)
    c: Coincident(g329,g330)
    c: Vertical(g330)
    c: Coincident(g330,g331)
    c: Coincident(g331,g332)
    c: Horizontal(g332)
    c: Coincident(g332,g333)
    c: Coincident(g333,g334)
    c: Vertical(g334)
    c: Coincident(g334,g335)
    c: Coincident(g335,g336)
    c: Horizontal(g336)
    c: Coincident(g336,g337)
    c: Coincident(g337,g338)
    c: Vertical(g338)
    c: Coincident(g338,g339)
    c: Coincident(g339,g340)
    c: Horizontal(g340)
    c: Coincident(g340,g341)
    c: Coincident(g341,g342)
    c: Vertical(g342)
    c: Coincident(g342,g343)
    c: Coincident(g343,g344)
    c: Horizontal(g344)
    c: Coincident(g344,g345)
    c: Coincident(g345,g346)
    c: Vertical(g346)
    c: Coincident(g346,g347)
    c: Coincident(g347,g348)
    c: Horizontal(g348)
    c: Coincident(g348,g349)
    c: Coincident(g349,g350)
    c: Vertical(g350)
    c: Coincident(g350,g351)
    c: Vertical(g359)
    c: Coincident(g359,g360)
    c: Horizontal(g360)
    c: Coincident(g360,g361)
    c: Vertical(g361)
    c: Coincident(g361,g362)
    c: Horizontal(g362)
    c: Coincident(g362,g359)
FEATURE [Sketcher::SketchObject] Sketch  label="top-plates-and-shield-221015"
  FullyConstrained = false
  sketch-geometry (439):
    g0: LineSegment StartX=-95.1105 StartY=66.7259 StartZ=0 EndX=-109.11 EndY=66.7259 EndZ=0
    g1: LineSegment StartX=-109.11 StartY=66.7259 StartZ=0 EndX=-109.11 EndY=52.7259 EndZ=0
    g2: LineSegment StartX=-109.11 StartY=52.7259 StartZ=0 EndX=-95.1105 EndY=52.7259 EndZ=0
    g3: LineSegment StartX=-95.1105 StartY=52.7259 StartZ=0 EndX=-95.1105 EndY=66.7259 EndZ=0
    g4: LineSegment StartX=-57.1105 StartY=97.7259 StartZ=0 EndX=-71.1105 EndY=97.7259 EndZ=0
    g5: LineSegment StartX=-71.1105 StartY=97.7259 StartZ=0 EndX=-71.1105 EndY=83.7259 EndZ=0
    g6: LineSegment StartX=-71.1105 StartY=83.7259 StartZ=0 EndX=-57.1105 EndY=83.7259 EndZ=0
    g7: LineSegment StartX=-57.1105 StartY=83.7259 StartZ=0 EndX=-57.1105 EndY=97.7259 EndZ=0
    g8: LineSegment StartX=-76.1105 StartY=99.7259 StartZ=0 EndX=-90.1105 EndY=99.7259 EndZ=0
    g9: LineSegment StartX=-90.1105 StartY=99.7259 StartZ=0 EndX=-90.1105 EndY=85.7259 EndZ=0
    g10: LineSegment StartX=-90.1105 StartY=85.7259 StartZ=0 EndX=-76.1105 EndY=85.7259 EndZ=0
    g11: LineSegment StartX=-76.1105 StartY=85.7259 StartZ=0 EndX=-76.1105 EndY=99.7259 EndZ=0
    g12: LineSegment StartX=-57.1105 StartY=59.7259 StartZ=0 EndX=-71.1105 EndY=59.7259 EndZ=0
    g13: LineSegment StartX=-71.1105 StartY=59.7259 StartZ=0 EndX=-71.1105 EndY=45.7259 EndZ=0
    g14: LineSegment StartX=-71.1105 StartY=45.7259 StartZ=0 EndX=-57.1105 EndY=45.7259 EndZ=0
    g15: LineSegment StartX=-57.1105 StartY=45.7259 StartZ=0 EndX=-57.1105 EndY=59.7259 EndZ=0
    g16: LineSegment StartX=-114.11 StartY=80.7259 StartZ=0 EndX=-128.11 EndY=80.7259 EndZ=0
    g17: LineSegment StartX=-128.11 StartY=80.7259 StartZ=0 EndX=-128.11 EndY=66.7259 EndZ=0
    g18: LineSegment StartX=-128.11 StartY=66.7259 StartZ=0 EndX=-114.11 EndY=66.7259 EndZ=0
    g19: LineSegment StartX=-114.11 StartY=66.7259 StartZ=0 EndX=-114.11 EndY=80.7259 EndZ=0
    g20: LineSegment StartX=-133.11 StartY=87.7259 StartZ=0 EndX=-147.11 EndY=87.7259 EndZ=0
    g21: LineSegment StartX=-147.11 StartY=87.7259 StartZ=0 EndX=-147.11 EndY=73.7259 EndZ=0
    g22: LineSegment StartX=-147.11 StartY=73.7259 StartZ=0 EndX=-133.11 EndY=73.7259 EndZ=0
    g23: LineSegment StartX=-133.11 StartY=73.7259 StartZ=0 EndX=-133.11 EndY=87.7259 EndZ=0
    g24: LineSegment StartX=-57.1105 StartY=78.7259 StartZ=0 EndX=-71.1105 EndY=78.7259 EndZ=0
    g25: LineSegment StartX=-71.1105 StartY=78.7259 StartZ=0 EndX=-71.1105 EndY=64.7259 EndZ=0
    g26: LineSegment StartX=-71.1105 StartY=64.7259 StartZ=0 EndX=-57.1105 EndY=64.7259 EndZ=0
    g27: LineSegment StartX=-57.1105 StartY=64.7259 StartZ=0 EndX=-57.1105 EndY=78.7259 EndZ=0
    g28: LineSegment StartX=-133.11 StartY=68.7259 StartZ=0 EndX=-147.11 EndY=68.7259 EndZ=0
    g29: LineSegment StartX=-147.11 StartY=68.7259 StartZ=0 EndX=-147.11 EndY=54.7259 EndZ=0
    g30: LineSegment StartX=-147.11 StartY=54.7259 StartZ=0 EndX=-133.11 EndY=54.7259 EndZ=0
    g31: LineSegment StartX=-133.11 StartY=54.7259 StartZ=0 EndX=-133.11 EndY=68.7259 EndZ=0
    g32: LineSegment StartX=-133.11 StartY=49.7259 StartZ=0 EndX=-147.11 EndY=49.7259 EndZ=0
    g33: LineSegment StartX=-147.11 StartY=49.7259 StartZ=0 EndX=-147.11 EndY=35.7259 EndZ=0
    g34: LineSegment StartX=-147.11 StartY=35.7259 StartZ=0 EndX=-133.11 EndY=35.7259 EndZ=0
    g35: LineSegment StartX=-133.11 StartY=35.7259 StartZ=0 EndX=-133.11 EndY=49.7259 EndZ=0
    g36: LineSegment StartX=-76.1105 StartY=61.7259 StartZ=0 EndX=-90.1105 EndY=61.7259 EndZ=0
    g37: LineSegment StartX=-90.1105 StartY=61.7259 StartZ=0 EndX=-90.1105 EndY=47.7259 EndZ=0
    g38: LineSegment StartX=-90.1105 StartY=47.7259 StartZ=0 EndX=-76.1105 EndY=47.7259 EndZ=0
    g39: LineSegment StartX=-76.1105 StartY=47.7259 StartZ=0 EndX=-76.1105 EndY=61.7259 EndZ=0
    g40: LineSegment StartX=-46.5015 StartY=34.9039 StartZ=0 EndX=-60.2885 EndY=37.3349 EndZ=0
    g41: LineSegment StartX=-60.2885 StartY=37.3349 StartZ=0 EndX=-62.7195 EndY=23.5479 EndZ=0
    g42: LineSegment StartX=-62.7195 StartY=23.5479 StartZ=0 EndX=-48.9325 EndY=21.1169 EndZ=0
    g43: LineSegment StartX=-48.9325 StartY=21.1169 StartZ=0 EndX=-46.5015 EndY=34.9039 EndZ=0
    g44: LineSegment StartX=-114.11 StartY=99.7259 StartZ=0 EndX=-128.11 EndY=99.7259 EndZ=0
    g45: LineSegment StartX=-128.11 StartY=99.7259 StartZ=0 EndX=-128.11 EndY=85.7259 EndZ=0
    g46: LineSegment StartX=-128.11 StartY=85.7259 StartZ=0 EndX=-114.11 EndY=85.7259 EndZ=0
    g47: LineSegment StartX=-114.11 StartY=85.7259 StartZ=0 EndX=-114.11 EndY=99.7259 EndZ=0
    g48: LineSegment StartX=-23.308 StartY=26.1119 StartZ=0 EndX=-35.9963 EndY=32.0279 EndZ=0
    g49: LineSegment StartX=-35.9963 StartY=32.0279 StartZ=0 EndX=-41.9125 EndY=19.3399 EndZ=0
    g50: LineSegment StartX=-41.9125 StartY=19.3399 StartZ=0 EndX=-29.2247 EndY=13.4239 EndZ=0
    g51: LineSegment StartX=-29.2247 StartY=13.4239 StartZ=0 EndX=-23.308 EndY=26.1119 EndZ=0
    g52: LineSegment StartX=-114.11 StartY=61.7259 StartZ=0 EndX=-128.11 EndY=61.7259 EndZ=0
    g53: LineSegment StartX=-128.11 StartY=61.7259 StartZ=0 EndX=-128.11 EndY=47.7259 EndZ=0
    g54: LineSegment StartX=-128.11 StartY=47.7259 StartZ=0 EndX=-114.11 EndY=47.7259 EndZ=0
    g55: LineSegment StartX=-114.11 StartY=47.7259 StartZ=0 EndX=-114.11 EndY=61.7259 EndZ=0
    g56: LineSegment StartX=-76.1105 StartY=66.7259 StartZ=0 EndX=-76.1105 EndY=80.7259 EndZ=0
    g57: LineSegment StartX=-76.1105 StartY=80.7259 StartZ=0 EndX=-90.1105 EndY=80.7259 EndZ=0
    g58: LineSegment StartX=-90.1105 StartY=80.7259 StartZ=0 EndX=-90.1105 EndY=66.7259 EndZ=0
    g59: LineSegment StartX=-90.1105 StartY=66.7259 StartZ=0 EndX=-76.1105 EndY=66.7259 EndZ=0
    g60: LineSegment StartX=-70.1105 StartY=38.2259 StartZ=0 EndX=-84.1105 EndY=38.2259 EndZ=0
    g61: LineSegment StartX=-84.1105 StartY=38.2259 StartZ=0 EndX=-84.1105 EndY=24.2259 EndZ=0
    g62: LineSegment StartX=-84.1105 StartY=24.2259 StartZ=0 EndX=-70.1105 EndY=24.2259 EndZ=0
    g63: LineSegment StartX=-70.1105 StartY=24.2259 StartZ=0 EndX=-70.1105 EndY=38.2259 EndZ=0
    g64: LineSegment StartX=-95.1105 StartY=85.7259 StartZ=0 EndX=-109.11 EndY=85.7259 EndZ=0
    g65: LineSegment StartX=-109.11 StartY=85.7259 StartZ=0 EndX=-109.11 EndY=71.7259 EndZ=0
    g66: LineSegment StartX=-109.11 StartY=71.7259 StartZ=0 EndX=-95.1105 EndY=71.7259 EndZ=0
    g67: LineSegment StartX=-95.1105 StartY=71.7259 StartZ=0 EndX=-95.1105 EndY=85.7259 EndZ=0
    g68: LineSegment StartX=-95.1105 StartY=104.726 StartZ=0 EndX=-109.11 EndY=104.726 EndZ=0
    g69: LineSegment StartX=-109.11 StartY=104.726 StartZ=0 EndX=-109.11 EndY=90.7259 EndZ=0
    g70: LineSegment StartX=-109.11 StartY=90.7259 StartZ=0 EndX=-95.1105 EndY=90.7259 EndZ=0
    g71: LineSegment StartX=-95.1105 StartY=90.7259 StartZ=0 EndX=-95.1105 EndY=104.726 EndZ=0
    g72: LineSegment StartX=-25.1105 StartY=10.7259 StartZ=0 EndX=-15.8751 EndY=30.1203 EndZ=0
    g73: ArcOfCircle CenterX=-17.6808 CenterY=30.9802 CenterZ=0 NormalX=0 NormalY=0 NormalZ=1 AngleXU=0 Radius=2 StartAngle=5.83877 EndAngle=7.30333
    g74: ArcOfCircle CenterX=-60.0005 CenterY=-37.9442 CenterZ=0 NormalX=0 NormalY=0 NormalZ=1 AngleXU=0 Radius=82.8797 StartAngle=1.02014 EndAngle=1.47771
    g75: ArcOfCircle CenterX=-52.1105 CenterY=46.568 CenterZ=0 NormalX=0 NormalY=0 NormalZ=1 AngleXU=0 Radius=2 StartAngle=3.14159 EndAngle=4.6193
    g76: LineSegment StartX=-54.1105 StartY=46.568 StartZ=0 EndX=-54.1105 EndY=74.7259 EndZ=0
    g77: ArcOfCircle CenterX=-52.1105 CenterY=74.7259 CenterZ=0 NormalX=0 NormalY=0 NormalZ=1 AngleXU=0 Radius=2 StartAngle=1.5708 EndAngle=3.14159
    g78: LineSegment StartX=-52.1105 StartY=76.7259 StartZ=0 EndX=-51.1105 EndY=76.7259 EndZ=0
    g79: ArcOfCircle CenterX=-51.1105 CenterY=78.7259 CenterZ=0 NormalX=0 NormalY=0 NormalZ=1 AngleXU=0 Radius=2 StartAngle=4.71239 EndAngle=6.28319
    g80: LineSegment StartX=-49.1105 StartY=78.7259 StartZ=0 EndX=-49.1105 EndY=81.7259 EndZ=0
    g81: ArcOfCircle CenterX=-51.1105 CenterY=81.7259 CenterZ=0 NormalX=0 NormalY=0 NormalZ=1 AngleXU=0 Radius=2 StartAngle=0 EndAngle=1.5708
    g82: LineSegment StartX=-51.1105 StartY=83.7259 StartZ=0 EndX=-52.1105 EndY=83.7259 EndZ=0
    g83: ArcOfCircle CenterX=-52.1105 CenterY=85.7259 CenterZ=0 NormalX=0 NormalY=0 NormalZ=1 AngleXU=0 Radius=2 StartAngle=3.14159 EndAngle=4.71239
    g84: LineSegment StartX=-54.1105 StartY=85.7259 StartZ=0 EndX=-54.1105 EndY=101.226 EndZ=0
    g85: ArcOfCircle CenterX=-56.1105 CenterY=101.226 CenterZ=0 NormalX=0 NormalY=0 NormalZ=1 AngleXU=0 Radius=2 StartAngle=0 EndAngle=1.5708
    g86: LineSegment StartX=-56.1105 StartY=103.226 StartZ=0 EndX=-89.6105 EndY=103.226 EndZ=0
    g87: ArcOfCircle CenterX=-89.6105 CenterY=105.226 CenterZ=0 NormalX=0 NormalY=0 NormalZ=1 AngleXU=0 Radius=2 StartAngle=3.14159 EndAngle=4.71239
    g88: LineSegment StartX=-91.6105 StartY=105.226 StartZ=0 EndX=-91.6105 EndY=106.226 EndZ=0
    g89: ArcOfCircle CenterX=-93.6105 CenterY=106.226 CenterZ=0 NormalX=0 NormalY=0 NormalZ=1 AngleXU=0 Radius=2 StartAngle=0 EndAngle=1.5708
    g90: LineSegment StartX=-93.6105 StartY=108.226 StartZ=0 EndX=-110.61 EndY=108.226 EndZ=0
    g91: ArcOfCircle CenterX=-110.61 CenterY=106.226 CenterZ=0 NormalX=0 NormalY=0 NormalZ=1 AngleXU=0 Radius=2 StartAngle=1.5708 EndAngle=3.14159
    g92: LineSegment StartX=-112.61 StartY=106.226 StartZ=0 EndX=-112.61 EndY=105.226 EndZ=0
    g93: ArcOfCircle CenterX=-114.61 CenterY=105.226 CenterZ=0 NormalX=0 NormalY=0 NormalZ=1 AngleXU=0 Radius=2 StartAngle=4.71239 EndAngle=6.28319
    g94: LineSegment StartX=-114.61 StartY=103.226 StartZ=0 EndX=-129.61 EndY=103.226 EndZ=0
    g95: ArcOfCircle CenterX=-129.61 CenterY=101.226 CenterZ=0 NormalX=0 NormalY=0 NormalZ=1 AngleXU=0 Radius=2 StartAngle=1.5708 EndAngle=3.14159
    g96: LineSegment StartX=-131.61 StartY=101.226 StartZ=0 EndX=-131.61 EndY=93.2259 EndZ=0
    g97: ArcOfCircle CenterX=-133.61 CenterY=93.2259 CenterZ=0 NormalX=0 NormalY=0 NormalZ=1 AngleXU=0 Radius=2 StartAngle=4.71239 EndAngle=6.28319
    g98: LineSegment StartX=-133.61 StartY=91.2259 StartZ=0 EndX=-148.61 EndY=91.2259 EndZ=0
    g99: ArcOfCircle CenterX=-148.61 CenterY=89.2259 CenterZ=0 NormalX=0 NormalY=0 NormalZ=1 AngleXU=0 Radius=2 StartAngle=1.5708 EndAngle=3.14159
    g100: LineSegment StartX=-150.61 StartY=89.2259 StartZ=0 EndX=-150.61 EndY=34.2259 EndZ=0
    g101: ArcOfCircle CenterX=-148.61 CenterY=34.2259 CenterZ=0 NormalX=0 NormalY=0 NormalZ=1 AngleXU=0 Radius=2 StartAngle=3.14159 EndAngle=4.71239
    g102: LineSegment StartX=-148.61 StartY=32.2259 StartZ=0 EndX=-131.61 EndY=32.2259 EndZ=0
    g103: ArcOfCircle CenterX=-131.61 CenterY=30.2259 CenterZ=0 NormalX=0 NormalY=0 NormalZ=1 AngleXU=0 Radius=2 StartAngle=0 EndAngle=1.5708
    g104: LineSegment StartX=-129.61 StartY=30.2259 StartZ=0 EndX=-129.61 EndY=29.2259 EndZ=0
    g105: ArcOfCircle CenterX=-128.11 CenterY=29.2259 CenterZ=0 NormalX=0 NormalY=0 NormalZ=1 AngleXU=0 Radius=1.5 StartAngle=3.14159 EndAngle=4.71239
    g106: LineSegment StartX=-128.11 StartY=27.7259 StartZ=0 EndX=-89.6105 EndY=27.7259 EndZ=0
    g107: ArcOfCircle CenterX=-89.6105 CenterY=25.7259 CenterZ=0 NormalX=0 NormalY=0 NormalZ=1 AngleXU=0 Radius=2 StartAngle=0 EndAngle=1.5708
    g108: LineSegment StartX=-87.6105 StartY=25.7259 StartZ=0 EndX=-87.6105 EndY=22.7259 EndZ=0
    g109: ArcOfCircle CenterX=-85.6105 CenterY=22.7259 CenterZ=0 NormalX=0 NormalY=0 NormalZ=1 AngleXU=0 Radius=2 StartAngle=3.14159 EndAngle=4.71239
    g110: Circle CenterX=-20.1105 CenterY=30.8259 CenterZ=0 NormalX=0 NormalY=0 NormalZ=-1 AngleXU=0 Radius=1.1
    g111: ArcOfCircle CenterX=-28.2141 CenterY=12.1069 CenterZ=0 NormalX=0 NormalY=0 NormalZ=1 AngleXU=0 Radius=3.39682 StartAngle=4.61462 EndAngle=5.86464
    g112: ArcOfCircle CenterX=-79.1115 CenterY=-90.0531 CenterZ=0 NormalX=0 NormalY=0 NormalZ=1 AngleXU=0 Radius=110.97 StartAngle=1.09767 EndAngle=1.62939
    g113: Circle CenterX=-130.61 CenterY=90.2259 CenterZ=0 NormalX=0 NormalY=0 NormalZ=-1 AngleXU=0 Radius=1.1
    g114: Circle CenterX=-43.6105 CenterY=26.2259 CenterZ=0 NormalX=0 NormalY=0 NormalZ=-1 AngleXU=0 Radius=1.1
    g115: Circle CenterX=-129.11 CenterY=33.7259 CenterZ=0 NormalX=0 NormalY=0 NormalZ=-1 AngleXU=0 Radius=1.1
    g116: Circle CenterX=-51.6105 CenterY=80.2259 CenterZ=0 NormalX=0 NormalY=0 NormalZ=-1 AngleXU=0 Radius=1.1
    g117: LineSegment StartX=-89.6105 StartY=29.1259 StartZ=0 EndX=-89.6105 EndY=43.3259 EndZ=0
    g118: LineSegment StartX=-89.6105 StartY=43.3259 StartZ=0 EndX=-107.11 EndY=43.3259 EndZ=0
    g119: LineSegment StartX=-107.11 StartY=43.3259 StartZ=0 EndX=-107.11 EndY=29.1259 EndZ=0
    g120: LineSegment StartX=-107.11 StartY=29.1259 StartZ=0 EndX=-89.6105 EndY=29.1259 EndZ=0
    g121: LineSegment StartX=94.6251 StartY=66.8023 StartZ=0 EndX=108.625 EndY=66.8023 EndZ=0
    g122: LineSegment StartX=108.625 StartY=66.8023 StartZ=0 EndX=108.625 EndY=52.8023 EndZ=0
    g123: LineSegment StartX=108.625 StartY=52.8023 StartZ=0 EndX=94.6251 EndY=52.8023 EndZ=0
    g124: LineSegment StartX=94.6251 StartY=52.8023 StartZ=0 EndX=94.6251 EndY=66.8023 EndZ=0
    g125: LineSegment StartX=56.6251 StartY=97.8023 StartZ=0 EndX=70.6251 EndY=97.8023 EndZ=0
    g126: LineSegment StartX=70.6251 StartY=97.8023 StartZ=0 EndX=70.6251 EndY=83.8023 EndZ=0
    g127: LineSegment StartX=70.6251 StartY=83.8023 StartZ=0 EndX=56.6251 EndY=83.8023 EndZ=0
    g128: LineSegment StartX=56.6251 StartY=83.8023 StartZ=0 EndX=56.6251 EndY=97.8023 EndZ=0
    g129: LineSegment StartX=75.6251 StartY=99.8023 StartZ=0 EndX=89.6251 EndY=99.8023 EndZ=0
    g130: LineSegment StartX=89.6251 StartY=99.8023 StartZ=0 EndX=89.6251 EndY=85.8023 EndZ=0
    g131: LineSegment StartX=89.6251 StartY=85.8023 StartZ=0 EndX=75.6251 EndY=85.8023 EndZ=0
    g132: LineSegment StartX=75.6251 StartY=85.8023 StartZ=0 EndX=75.6251 EndY=99.8023 EndZ=0
    g133: LineSegment StartX=56.6251 StartY=59.8023 StartZ=0 EndX=70.6251 EndY=59.8023 EndZ=0
    g134: LineSegment StartX=70.6251 StartY=59.8023 StartZ=0 EndX=70.6251 EndY=45.8023 EndZ=0
    g135: LineSegment StartX=70.6251 StartY=45.8023 StartZ=0 EndX=56.6251 EndY=45.8023 EndZ=0
    g136: LineSegment StartX=56.6251 StartY=45.8023 StartZ=0 EndX=56.6251 EndY=59.8023 EndZ=0
    g137: LineSegment StartX=113.625 StartY=80.8023 StartZ=0 EndX=127.625 EndY=80.8023 EndZ=0
    g138: LineSegment StartX=127.625 StartY=80.8023 StartZ=0 EndX=127.625 EndY=66.8023 EndZ=0
    g139: LineSegment StartX=127.625 StartY=66.8023 StartZ=0 EndX=113.625 EndY=66.8023 EndZ=0
    g140: LineSegment StartX=113.625 StartY=66.8023 StartZ=0 EndX=113.625 EndY=80.8023 EndZ=0
    g141: LineSegment StartX=132.625 StartY=87.8023 StartZ=0 EndX=146.625 EndY=87.8023 EndZ=0
    g142: LineSegment StartX=146.625 StartY=87.8023 StartZ=0 EndX=146.625 EndY=73.8023 EndZ=0
    g143: LineSegment StartX=146.625 StartY=73.8023 StartZ=0 EndX=132.625 EndY=73.8023 EndZ=0
    g144: LineSegment StartX=132.625 StartY=73.8023 StartZ=0 EndX=132.625 EndY=87.8023 EndZ=0
    g145: LineSegment StartX=56.6251 StartY=78.8023 StartZ=0 EndX=70.6251 EndY=78.8023 EndZ=0
    g146: LineSegment StartX=70.6251 StartY=78.8023 StartZ=0 EndX=70.6251 EndY=64.8023 EndZ=0
    g147: LineSegment StartX=70.6251 StartY=64.8023 StartZ=0 EndX=56.6251 EndY=64.8023 EndZ=0
    g148: LineSegment StartX=56.6251 StartY=64.8023 StartZ=0 EndX=56.6251 EndY=78.8023 EndZ=0
    g149: LineSegment StartX=132.625 StartY=68.8023 StartZ=0 EndX=146.625 EndY=68.8023 EndZ=0
    g150: LineSegment StartX=146.625 StartY=68.8023 StartZ=0 EndX=146.625 EndY=54.8023 EndZ=0
    g151: LineSegment StartX=146.625 StartY=54.8023 StartZ=0 EndX=132.625 EndY=54.8023 EndZ=0
    g152: LineSegment StartX=132.625 StartY=54.8023 StartZ=0 EndX=132.625 EndY=68.8023 EndZ=0
    g153: LineSegment StartX=132.625 StartY=49.8023 StartZ=0 EndX=146.625 EndY=49.8023 EndZ=0
    g154: LineSegment StartX=146.625 StartY=49.8023 StartZ=0 EndX=146.625 EndY=35.8023 EndZ=0
    g155: LineSegment StartX=146.625 StartY=35.8023 StartZ=0 EndX=132.625 EndY=35.8023 EndZ=0
    g156: LineSegment StartX=132.625 StartY=35.8023 StartZ=0 EndX=132.625 EndY=49.8023 EndZ=0
    g157: LineSegment StartX=75.6251 StartY=61.8023 StartZ=0 EndX=89.6251 EndY=61.8023 EndZ=0
    g158: LineSegment StartX=89.6251 StartY=61.8023 StartZ=0 EndX=89.6251 EndY=47.8023 EndZ=0
    g159: LineSegment StartX=89.6251 StartY=47.8023 StartZ=0 EndX=75.6251 EndY=47.8023 EndZ=0
    g160: LineSegment StartX=75.6251 StartY=47.8023 StartZ=0 EndX=75.6251 EndY=61.8023 EndZ=0
    g161: LineSegment StartX=46.0161 StartY=34.9803 StartZ=0 EndX=59.8031 EndY=37.4113 EndZ=0
    g162: LineSegment StartX=59.8031 StartY=37.4113 StartZ=0 EndX=62.2341 EndY=23.6243 EndZ=0
    g163: LineSegment StartX=62.2341 StartY=23.6243 StartZ=0 EndX=48.4471 EndY=21.1933 EndZ=0
    g164: LineSegment StartX=48.4471 StartY=21.1933 StartZ=0 EndX=46.0161 EndY=34.9803 EndZ=0
    g165: LineSegment StartX=113.625 StartY=99.8023 StartZ=0 EndX=127.625 EndY=99.8023 EndZ=0
    g166: LineSegment StartX=127.625 StartY=99.8023 StartZ=0 EndX=127.625 EndY=85.8023 EndZ=0
    g167: LineSegment StartX=127.625 StartY=85.8023 StartZ=0 EndX=113.625 EndY=85.8023 EndZ=0
    g168: LineSegment StartX=113.625 StartY=85.8023 StartZ=0 EndX=113.625 EndY=99.8023 EndZ=0
    g169: LineSegment StartX=22.8226 StartY=26.1883 StartZ=0 EndX=35.5109 EndY=32.1043 EndZ=0
    g170: LineSegment StartX=35.5109 StartY=32.1043 StartZ=0 EndX=41.4271 EndY=19.4163 EndZ=0
    g171: LineSegment StartX=41.4271 StartY=19.4163 StartZ=0 EndX=28.7393 EndY=13.5003 EndZ=0
    g172: LineSegment StartX=28.7393 StartY=13.5003 StartZ=0 EndX=22.8226 EndY=26.1883 EndZ=0
    g173: LineSegment StartX=113.625 StartY=61.8023 StartZ=0 EndX=127.625 EndY=61.8023 EndZ=0
    g174: LineSegment StartX=127.625 StartY=61.8023 StartZ=0 EndX=127.625 EndY=47.8023 EndZ=0
    g175: LineSegment StartX=127.625 StartY=47.8023 StartZ=0 EndX=113.625 EndY=47.8023 EndZ=0
    g176: LineSegment StartX=113.625 StartY=47.8023 StartZ=0 EndX=113.625 EndY=61.8023 EndZ=0
    g177: LineSegment StartX=75.6251 StartY=66.8023 StartZ=0 EndX=75.6251 EndY=80.8023 EndZ=0
    g178: LineSegment StartX=75.6251 StartY=80.8023 StartZ=0 EndX=89.6251 EndY=80.8023 EndZ=0
    g179: LineSegment StartX=89.6251 StartY=80.8023 StartZ=0 EndX=89.6251 EndY=66.8023 EndZ=0
    g180: LineSegment StartX=89.6251 StartY=66.8023 StartZ=0 EndX=75.6251 EndY=66.8023 EndZ=0
    g181: LineSegment StartX=69.6251 StartY=38.3023 StartZ=0 EndX=83.6251 EndY=38.3023 EndZ=0
    g182: LineSegment StartX=83.6251 StartY=38.3023 StartZ=0 EndX=83.6251 EndY=24.3023 EndZ=0
    g183: LineSegment StartX=83.6251 StartY=24.3023 StartZ=0 EndX=69.6251 EndY=24.3023 EndZ=0
    g184: LineSegment StartX=69.6251 StartY=24.3023 StartZ=0 EndX=69.6251 EndY=38.3023 EndZ=0
    g185: LineSegment StartX=94.6251 StartY=85.8023 StartZ=0 EndX=108.625 EndY=85.8023 EndZ=0
    g186: LineSegment StartX=108.625 StartY=85.8023 StartZ=0 EndX=108.625 EndY=71.8023 EndZ=0
    g187: LineSegment StartX=108.625 StartY=71.8023 StartZ=0 EndX=94.6251 EndY=71.8023 EndZ=0
    g188: LineSegment StartX=94.6251 StartY=71.8023 StartZ=0 EndX=94.6251 EndY=85.8023 EndZ=0
    g189: LineSegment StartX=94.6251 StartY=104.802 StartZ=0 EndX=108.625 EndY=104.802 EndZ=0
    g190: LineSegment StartX=108.625 StartY=104.802 StartZ=0 EndX=108.625 EndY=90.8023 EndZ=0
    g191: LineSegment StartX=108.625 StartY=90.8023 StartZ=0 EndX=94.6251 EndY=90.8023 EndZ=0
    g192: LineSegment StartX=94.6251 StartY=90.8023 StartZ=0 EndX=94.6251 EndY=104.802 EndZ=0
    g193: LineSegment StartX=24.6251 StartY=10.8023 StartZ=0 EndX=15.3897 EndY=30.1966 EndZ=0
    g194: ArcOfCircle CenterX=17.1954 CenterY=31.0565 CenterZ=0 NormalX=0 NormalY=0 NormalZ=1 AngleXU=0 Radius=2 StartAngle=2.12145 EndAngle=3.58601
    g195: ArcOfCircle CenterX=59.5152 CenterY=-37.8679 CenterZ=0 NormalX=0 NormalY=0 NormalZ=1 AngleXU=0 Radius=82.8797 StartAngle=1.66389 EndAngle=2.12145
    g196: ArcOfCircle CenterX=51.6251 CenterY=46.6443 CenterZ=0 NormalX=0 NormalY=0 NormalZ=1 AngleXU=0 Radius=2 StartAngle=4.80548 EndAngle=6.28319
    g197: LineSegment StartX=53.6251 StartY=46.6443 StartZ=0 EndX=53.6251 EndY=74.8023 EndZ=0
    g198: ArcOfCircle CenterX=51.6251 CenterY=74.8023 CenterZ=0 NormalX=0 NormalY=0 NormalZ=1 AngleXU=0 Radius=2 StartAngle=0 EndAngle=1.5708
    g199: LineSegment StartX=51.6251 StartY=76.8023 StartZ=0 EndX=50.6251 EndY=76.8023 EndZ=0
    g200: ArcOfCircle CenterX=50.6251 CenterY=78.8023 CenterZ=0 NormalX=0 NormalY=0 NormalZ=1 AngleXU=0 Radius=2 StartAngle=3.14159 EndAngle=4.71239
    g201: LineSegment StartX=48.6251 StartY=78.8023 StartZ=0 EndX=48.6251 EndY=81.8023 EndZ=0
    g202: ArcOfCircle CenterX=50.6251 CenterY=81.8023 CenterZ=0 NormalX=0 NormalY=0 NormalZ=1 AngleXU=0 Radius=2 StartAngle=1.5708 EndAngle=3.14159
    g203: LineSegment StartX=50.6251 StartY=83.8023 StartZ=0 EndX=51.6251 EndY=83.8023 EndZ=0
    g204: ArcOfCircle CenterX=51.6251 CenterY=85.8023 CenterZ=0 NormalX=0 NormalY=0 NormalZ=1 AngleXU=0 Radius=2 StartAngle=4.71239 EndAngle=6.28319
    g205: LineSegment StartX=53.6251 StartY=85.8023 StartZ=0 EndX=53.6251 EndY=101.302 EndZ=0
    g206: ArcOfCircle CenterX=55.6251 CenterY=101.302 CenterZ=0 NormalX=0 NormalY=0 NormalZ=1 AngleXU=0 Radius=2 StartAngle=1.5708 EndAngle=3.14159
    g207: LineSegment StartX=55.6251 StartY=103.302 StartZ=0 EndX=89.1251 EndY=103.302 EndZ=0
    g208: ArcOfCircle CenterX=89.1251 CenterY=105.302 CenterZ=0 NormalX=0 NormalY=0 NormalZ=1 AngleXU=0 Radius=2 StartAngle=4.71239 EndAngle=6.28319
    g209: LineSegment StartX=91.1251 StartY=105.302 StartZ=0 EndX=91.1251 EndY=106.302 EndZ=0
    g210: ArcOfCircle CenterX=93.1251 CenterY=106.302 CenterZ=0 NormalX=0 NormalY=0 NormalZ=1 AngleXU=0 Radius=2 StartAngle=1.5708 EndAngle=3.14159
    g211: LineSegment StartX=93.1251 StartY=108.302 StartZ=0 EndX=110.125 EndY=108.302 EndZ=0
    g212: ArcOfCircle CenterX=110.125 CenterY=106.302 CenterZ=0 NormalX=0 NormalY=0 NormalZ=1 AngleXU=0 Radius=2 StartAngle=0 EndAngle=1.5708
    g213: LineSegment StartX=112.125 StartY=106.302 StartZ=0 EndX=112.125 EndY=105.302 EndZ=0
    g214: ArcOfCircle CenterX=114.125 CenterY=105.302 CenterZ=0 NormalX=0 NormalY=0 NormalZ=1 AngleXU=0 Radius=2 StartAngle=3.14159 EndAngle=4.71239
    g215: LineSegment StartX=114.125 StartY=103.302 StartZ=0 EndX=129.125 EndY=103.302 EndZ=0
    g216: ArcOfCircle CenterX=129.125 CenterY=101.302 CenterZ=0 NormalX=0 NormalY=0 NormalZ=1 AngleXU=0 Radius=2 StartAngle=0 EndAngle=1.5708
    g217: LineSegment StartX=131.125 StartY=101.302 StartZ=0 EndX=131.125 EndY=93.3023 EndZ=0
    g218: ArcOfCircle CenterX=133.125 CenterY=93.3023 CenterZ=0 NormalX=0 NormalY=0 NormalZ=1 AngleXU=0 Radius=2 StartAngle=3.14159 EndAngle=4.71239
    g219: LineSegment StartX=133.125 StartY=91.3023 StartZ=0 EndX=148.125 EndY=91.3023 EndZ=0
    g220: ArcOfCircle CenterX=148.125 CenterY=89.3023 CenterZ=0 NormalX=0 NormalY=0 NormalZ=1 AngleXU=0 Radius=2 StartAngle=0 EndAngle=1.5708
    g221: LineSegment StartX=150.125 StartY=89.3023 StartZ=0 EndX=150.125 EndY=34.3023 EndZ=0
    g222: ArcOfCircle CenterX=148.125 CenterY=34.3023 CenterZ=0 NormalX=0 NormalY=0 NormalZ=1 AngleXU=0 Radius=2 StartAngle=4.71239 EndAngle=6.28319
    g223: LineSegment StartX=148.125 StartY=32.3023 StartZ=0 EndX=131.125 EndY=32.3023 EndZ=0
    g224: ArcOfCircle CenterX=131.125 CenterY=30.3023 CenterZ=0 NormalX=0 NormalY=0 NormalZ=1 AngleXU=0 Radius=2 StartAngle=1.5708 EndAngle=3.14159
    g225: LineSegment StartX=129.125 StartY=30.3023 StartZ=0 EndX=129.125 EndY=29.3023 EndZ=0
    g226: ArcOfCircle CenterX=127.625 CenterY=29.3023 CenterZ=0 NormalX=0 NormalY=0 NormalZ=1 AngleXU=0 Radius=1.5 StartAngle=4.71239 EndAngle=6.28319
    g227: LineSegment StartX=127.625 StartY=27.8023 StartZ=0 EndX=89.1251 EndY=27.8023 EndZ=0
    g228: ArcOfCircle CenterX=89.1251 CenterY=25.8023 CenterZ=0 NormalX=0 NormalY=0 NormalZ=1 AngleXU=0 Radius=2 StartAngle=1.5708 EndAngle=3.14159
    g229: LineSegment StartX=87.1251 StartY=25.8023 StartZ=0 EndX=87.1251 EndY=22.8023 EndZ=0
    g230: ArcOfCircle CenterX=85.1251 CenterY=22.8023 CenterZ=0 NormalX=0 NormalY=0 NormalZ=1 AngleXU=0 Radius=2 StartAngle=4.71239 EndAngle=6.28319
    g231: Circle CenterX=19.6251 CenterY=30.9023 CenterZ=0 NormalX=0 NormalY=0 NormalZ=-1 AngleXU=0 Radius=1.1
    g232: ArcOfCircle CenterX=27.7287 CenterY=12.1833 CenterZ=0 NormalX=0 NormalY=0 NormalZ=1 AngleXU=0 Radius=3.39682 StartAngle=3.56014 EndAngle=4.81016
    g233: ArcOfCircle CenterX=78.6261 CenterY=-89.9767 CenterZ=0 NormalX=0 NormalY=0 NormalZ=1 AngleXU=0 Radius=110.97 StartAngle=1.5122 EndAngle=2.04392
    g234: Circle CenterX=130.125 CenterY=90.3023 CenterZ=0 NormalX=0 NormalY=0 NormalZ=-1 AngleXU=0 Radius=1.1
    g235: Circle CenterX=43.1251 CenterY=26.3023 CenterZ=0 NormalX=0 NormalY=0 NormalZ=-1 AngleXU=0 Radius=1.1
    g236: Circle CenterX=128.625 CenterY=33.8023 CenterZ=0 NormalX=0 NormalY=0 NormalZ=-1 AngleXU=0 Radius=1.1
    g237: Circle CenterX=51.1251 CenterY=80.3023 CenterZ=0 NormalX=0 NormalY=0 NormalZ=-1 AngleXU=0 Radius=1.1
    g238: LineSegment StartX=126.125 StartY=29.2023 StartZ=0 EndX=126.125 EndY=43.4023 EndZ=0
    g239: LineSegment StartX=126.125 StartY=43.4023 StartZ=0 EndX=108.625 EndY=43.4023 EndZ=0
    g240: LineSegment StartX=108.625 StartY=43.4023 StartZ=0 EndX=108.625 EndY=29.2023 EndZ=0
    g241: LineSegment StartX=108.625 StartY=29.2023 StartZ=0 EndX=126.125 EndY=29.2023 EndZ=0
    g242: LineSegment StartX=-95.1105 StartY=66.7259 StartZ=0 EndX=-109.11 EndY=66.7259 EndZ=0
    g243: LineSegment StartX=-109.11 StartY=66.7259 StartZ=0 EndX=-109.11 EndY=52.7259 EndZ=0
    g244: LineSegment StartX=-109.11 StartY=52.7259 StartZ=0 EndX=-95.1105 EndY=52.7259 EndZ=0
    g245: LineSegment StartX=-95.1105 StartY=52.7259 StartZ=0 EndX=-95.1105 EndY=66.7259 EndZ=0
    g246: LineSegment StartX=-57.1105 StartY=97.7259 StartZ=0 EndX=-71.1105 EndY=97.7259 EndZ=0
    g247: LineSegment StartX=-71.1105 StartY=97.7259 StartZ=0 EndX=-71.1105 EndY=83.7259 EndZ=0
    g248: LineSegment StartX=-71.1105 StartY=83.7259 StartZ=0 EndX=-57.1105 EndY=83.7259 EndZ=0
    g249: LineSegment StartX=-57.1105 StartY=83.7259 StartZ=0 EndX=-57.1105 EndY=97.7259 EndZ=0
    g250: LineSegment StartX=-76.1105 StartY=99.7259 StartZ=0 EndX=-90.1105 EndY=99.7259 EndZ=0
    g251: LineSegment StartX=-90.1105 StartY=99.7259 StartZ=0 EndX=-90.1105 EndY=85.7259 EndZ=0
    g252: LineSegment StartX=-90.1105 StartY=85.7259 StartZ=0 EndX=-76.1105 EndY=85.7259 EndZ=0
    g253: LineSegment StartX=-76.1105 StartY=85.7259 StartZ=0 EndX=-76.1105 EndY=99.7259 EndZ=0
    g254: LineSegment StartX=-57.1105 StartY=59.7259 StartZ=0 EndX=-71.1105 EndY=59.7259 EndZ=0
    g255: LineSegment StartX=-71.1105 StartY=59.7259 StartZ=0 EndX=-71.1105 EndY=45.7259 EndZ=0
    g256: LineSegment StartX=-71.1105 StartY=45.7259 StartZ=0 EndX=-57.1105 EndY=45.7259 EndZ=0
    g257: LineSegment StartX=-57.1105 StartY=45.7259 StartZ=0 EndX=-57.1105 EndY=59.7259 EndZ=0
    g258: LineSegment StartX=-114.11 StartY=80.7259 StartZ=0 EndX=-128.11 EndY=80.7259 EndZ=0
    g259: LineSegment StartX=-128.11 StartY=80.7259 StartZ=0 EndX=-128.11 EndY=66.7259 EndZ=0
    g260: LineSegment StartX=-128.11 StartY=66.7259 StartZ=0 EndX=-114.11 EndY=66.7259 EndZ=0
    g261: LineSegment StartX=-114.11 StartY=66.7259 StartZ=0 EndX=-114.11 EndY=80.7259 EndZ=0
    g262: LineSegment StartX=-133.11 StartY=87.7259 StartZ=0 EndX=-147.11 EndY=87.7259 EndZ=0
    g263: LineSegment StartX=-147.11 StartY=87.7259 StartZ=0 EndX=-147.11 EndY=73.7259 EndZ=0
    g264: LineSegment StartX=-147.11 StartY=73.7259 StartZ=0 EndX=-133.11 EndY=73.7259 EndZ=0
    g265: LineSegment StartX=-133.11 StartY=73.7259 StartZ=0 EndX=-133.11 EndY=87.7259 EndZ=0
    g266: LineSegment StartX=-57.1105 StartY=78.7259 StartZ=0 EndX=-71.1105 EndY=78.7259 EndZ=0
    g267: LineSegment StartX=-71.1105 StartY=78.7259 StartZ=0 EndX=-71.1105 EndY=64.7259 EndZ=0
    g268: LineSegment StartX=-71.1105 StartY=64.7259 StartZ=0 EndX=-57.1105 EndY=64.7259 EndZ=0
    g269: LineSegment StartX=-57.1105 StartY=64.7259 StartZ=0 EndX=-57.1105 EndY=78.7259 EndZ=0
    g270: LineSegment StartX=-133.11 StartY=68.7259 StartZ=0 EndX=-147.11 EndY=68.7259 EndZ=0
    g271: LineSegment StartX=-147.11 StartY=68.7259 StartZ=0 EndX=-147.11 EndY=54.7259 EndZ=0
    g272: LineSegment StartX=-147.11 StartY=54.7259 StartZ=0 EndX=-133.11 EndY=54.7259 EndZ=0
    g273: LineSegment StartX=-133.11 StartY=54.7259 StartZ=0 EndX=-133.11 EndY=68.7259 EndZ=0
    g274: LineSegment StartX=-133.11 StartY=49.7259 StartZ=0 EndX=-147.11 EndY=49.7259 EndZ=0
    g275: LineSegment StartX=-147.11 StartY=49.7259 StartZ=0 EndX=-147.11 EndY=35.7259 EndZ=0
    g276: LineSegment StartX=-147.11 StartY=35.7259 StartZ=0 EndX=-133.11 EndY=35.7259 EndZ=0
    g277: LineSegment StartX=-133.11 StartY=35.7259 StartZ=0 EndX=-133.11 EndY=49.7259 EndZ=0
    g278: LineSegment StartX=-76.1105 StartY=61.7259 StartZ=0 EndX=-90.1105 EndY=61.7259 EndZ=0
    g279: LineSegment StartX=-90.1105 StartY=61.7259 StartZ=0 EndX=-90.1105 EndY=47.7259 EndZ=0
    g280: LineSegment StartX=-90.1105 StartY=47.7259 StartZ=0 EndX=-76.1105 EndY=47.7259 EndZ=0
    g281: LineSegment StartX=-76.1105 StartY=47.7259 StartZ=0 EndX=-76.1105 EndY=61.7259 EndZ=0
    g282: LineSegment StartX=-46.5015 StartY=34.9039 StartZ=0 EndX=-60.2885 EndY=37.3349 EndZ=0
    g283: LineSegment StartX=-60.2885 StartY=37.3349 StartZ=0 EndX=-62.7195 EndY=23.5479 EndZ=0
    g284: LineSegment StartX=-62.7195 StartY=23.5479 StartZ=0 EndX=-48.9325 EndY=21.1169 EndZ=0
    g285: LineSegment StartX=-48.9325 StartY=21.1169 StartZ=0 EndX=-46.5015 EndY=34.9039 EndZ=0
    g286: LineSegment StartX=-114.11 StartY=99.7259 StartZ=0 EndX=-128.11 EndY=99.7259 EndZ=0
    g287: LineSegment StartX=-128.11 StartY=99.7259 StartZ=0 EndX=-128.11 EndY=85.7259 EndZ=0
    g288: LineSegment StartX=-128.11 StartY=85.7259 StartZ=0 EndX=-114.11 EndY=85.7259 EndZ=0
    g289: LineSegment StartX=-114.11 StartY=85.7259 StartZ=0 EndX=-114.11 EndY=99.7259 EndZ=0
    g290: LineSegment StartX=-23.308 StartY=26.1119 StartZ=0 EndX=-35.9963 EndY=32.0279 EndZ=0
    g291: LineSegment StartX=-35.9963 StartY=32.0279 StartZ=0 EndX=-41.9125 EndY=19.3399 EndZ=0
    g292: LineSegment StartX=-41.9125 StartY=19.3399 StartZ=0 EndX=-29.2247 EndY=13.4239 EndZ=0
    g293: LineSegment StartX=-29.2247 StartY=13.4239 StartZ=0 EndX=-23.308 EndY=26.1119 EndZ=0
    g294: LineSegment StartX=-114.11 StartY=61.7259 StartZ=0 EndX=-128.11 EndY=61.7259 EndZ=0
    g295: LineSegment StartX=-128.11 StartY=61.7259 StartZ=0 EndX=-128.11 EndY=47.7259 EndZ=0
    g296: LineSegment StartX=-128.11 StartY=47.7259 StartZ=0 EndX=-114.11 EndY=47.7259 EndZ=0
    g297: LineSegment StartX=-114.11 StartY=47.7259 StartZ=0 EndX=-114.11 EndY=61.7259 EndZ=0
    g298: LineSegment StartX=-76.1105 StartY=66.7259 StartZ=0 EndX=-76.1105 EndY=80.7259 EndZ=0
    g299: LineSegment StartX=-76.1105 StartY=80.7259 StartZ=0 EndX=-90.1105 EndY=80.7259 EndZ=0
    g300: LineSegment StartX=-90.1105 StartY=80.7259 StartZ=0 EndX=-90.1105 EndY=66.7259 EndZ=0
    g301: LineSegment StartX=-90.1105 StartY=66.7259 StartZ=0 EndX=-76.1105 EndY=66.7259 EndZ=0
    g302: LineSegment StartX=-70.1105 StartY=38.2259 StartZ=0 EndX=-84.1105 EndY=38.2259 EndZ=0
    g303: LineSegment StartX=-84.1105 StartY=38.2259 StartZ=0 EndX=-84.1105 EndY=24.2259 EndZ=0
    g304: LineSegment StartX=-84.1105 StartY=24.2259 StartZ=0 EndX=-70.1105 EndY=24.2259 EndZ=0
    g305: LineSegment StartX=-70.1105 StartY=24.2259 StartZ=0 EndX=-70.1105 EndY=38.2259 EndZ=0
    g306: LineSegment StartX=-95.1105 StartY=85.7259 StartZ=0 EndX=-109.11 EndY=85.7259 EndZ=0
    g307: LineSegment StartX=-109.11 StartY=85.7259 StartZ=0 EndX=-109.11 EndY=71.7259 EndZ=0
    g308: LineSegment StartX=-109.11 StartY=71.7259 StartZ=0 EndX=-95.1105 EndY=71.7259 EndZ=0
    g309: LineSegment StartX=-95.1105 StartY=71.7259 StartZ=0 EndX=-95.1105 EndY=85.7259 EndZ=0
    g310: LineSegment StartX=-95.1105 StartY=104.726 StartZ=0 EndX=-109.11 EndY=104.726 EndZ=0
    g311: LineSegment StartX=-109.11 StartY=104.726 StartZ=0 EndX=-109.11 EndY=90.7259 EndZ=0
    g312: LineSegment StartX=-109.11 StartY=90.7259 StartZ=0 EndX=-95.1105 EndY=90.7259 EndZ=0
    g313: LineSegment StartX=-95.1105 StartY=90.7259 StartZ=0 EndX=-95.1105 EndY=104.726 EndZ=0
    g314: LineSegment StartX=-25.1105 StartY=10.7259 StartZ=0 EndX=-15.8751 EndY=30.1203 EndZ=0
    g315: ArcOfCircle CenterX=-17.6808 CenterY=30.9802 CenterZ=0 NormalX=0 NormalY=0 NormalZ=1 AngleXU=0 Radius=2 StartAngle=5.83877 EndAngle=7.30333
    g316: ArcOfCircle CenterX=-60.0005 CenterY=-37.9442 CenterZ=0 NormalX=0 NormalY=0 NormalZ=1 AngleXU=0 Radius=82.8797 StartAngle=1.02014 EndAngle=1.47771
    g317: ArcOfCircle CenterX=-52.1105 CenterY=46.568 CenterZ=0 NormalX=0 NormalY=0 NormalZ=1 AngleXU=0 Radius=2 StartAngle=3.14159 EndAngle=4.6193
    g318: LineSegment StartX=-54.1105 StartY=46.568 StartZ=0 EndX=-54.1105 EndY=74.7259 EndZ=0
    g319: ArcOfCircle CenterX=-52.1105 CenterY=74.7259 CenterZ=0 NormalX=0 NormalY=0 NormalZ=1 AngleXU=0 Radius=2 StartAngle=1.5708 EndAngle=3.14159
    g320: LineSegment StartX=-52.1105 StartY=76.7259 StartZ=0 EndX=-51.1105 EndY=76.7259 EndZ=0
    g321: ArcOfCircle CenterX=-51.1105 CenterY=78.7259 CenterZ=0 NormalX=0 NormalY=0 NormalZ=1 AngleXU=0 Radius=2 StartAngle=4.71239 EndAngle=6.28319
    g322: LineSegment StartX=-49.1105 StartY=78.7259 StartZ=0 EndX=-49.1105 EndY=81.7259 EndZ=0
    g323: ArcOfCircle CenterX=-51.1105 CenterY=81.7259 CenterZ=0 NormalX=0 NormalY=0 NormalZ=1 AngleXU=0 Radius=2 StartAngle=0 EndAngle=1.5708
    g324: LineSegment StartX=-51.1105 StartY=83.7259 StartZ=0 EndX=-52.1105 EndY=83.7259 EndZ=0
    g325: ArcOfCircle CenterX=-52.1105 CenterY=85.7259 CenterZ=0 NormalX=0 NormalY=0 NormalZ=1 AngleXU=0 Radius=2 StartAngle=3.14159 EndAngle=4.71239
    g326: LineSegment StartX=-54.1105 StartY=85.7259 StartZ=0 EndX=-54.1105 EndY=101.226 EndZ=0
    g327: ArcOfCircle CenterX=-56.1105 CenterY=101.226 CenterZ=0 NormalX=0 NormalY=0 NormalZ=1 AngleXU=0 Radius=2 StartAngle=0 EndAngle=1.5708
    g328: LineSegment StartX=-56.1105 StartY=103.226 StartZ=0 EndX=-89.6105 EndY=103.226 EndZ=0
    g329: ArcOfCircle CenterX=-89.6105 CenterY=105.226 CenterZ=0 NormalX=0 NormalY=0 NormalZ=1 AngleXU=0 Radius=2 StartAngle=3.14159 EndAngle=4.71239
    g330: LineSegment StartX=-91.6105 StartY=105.226 StartZ=0 EndX=-91.6105 EndY=106.226 EndZ=0
    g331: ArcOfCircle CenterX=-93.6105 CenterY=106.226 CenterZ=0 NormalX=0 NormalY=0 NormalZ=1 AngleXU=0 Radius=2 StartAngle=0 EndAngle=1.5708
    g332: LineSegment StartX=-93.6105 StartY=108.226 StartZ=0 EndX=-110.61 EndY=108.226 EndZ=0
    g333: ArcOfCircle CenterX=-110.61 CenterY=106.226 CenterZ=0 NormalX=0 NormalY=0 NormalZ=1 AngleXU=0 Radius=2 StartAngle=1.5708 EndAngle=3.14159
    g334: LineSegment StartX=-112.61 StartY=106.226 StartZ=0 EndX=-112.61 EndY=105.226 EndZ=0
    g335: ArcOfCircle CenterX=-114.61 CenterY=105.226 CenterZ=0 NormalX=0 NormalY=0 NormalZ=1 AngleXU=0 Radius=2 StartAngle=4.71239 EndAngle=6.28319
    g336: LineSegment StartX=-114.61 StartY=103.226 StartZ=0 EndX=-129.61 EndY=103.226 EndZ=0
    g337: ArcOfCircle CenterX=-129.61 CenterY=101.226 CenterZ=0 NormalX=0 NormalY=0 NormalZ=1 AngleXU=0 Radius=2 StartAngle=1.5708 EndAngle=3.14159
    g338: LineSegment StartX=-131.61 StartY=101.226 StartZ=0 EndX=-131.61 EndY=93.2259 EndZ=0
    g339: ArcOfCircle CenterX=-133.61 CenterY=93.2259 CenterZ=0 NormalX=0 NormalY=0 NormalZ=1 AngleXU=0 Radius=2 StartAngle=4.71239 EndAngle=6.28319
    g340: LineSegment StartX=-133.61 StartY=91.2259 StartZ=0 EndX=-148.61 EndY=91.2259 EndZ=0
    g341: ArcOfCircle CenterX=-148.61 CenterY=89.2259 CenterZ=0 NormalX=0 NormalY=0 NormalZ=1 AngleXU=0 Radius=2 StartAngle=1.5708 EndAngle=3.14159
    g342: LineSegment StartX=-150.61 StartY=89.2259 StartZ=0 EndX=-150.61 EndY=34.2259 EndZ=0
    g343: ArcOfCircle CenterX=-148.61 CenterY=34.2259 CenterZ=0 NormalX=0 NormalY=0 NormalZ=1 AngleXU=0 Radius=2 StartAngle=3.14159 EndAngle=4.71239
    g344: LineSegment StartX=-148.61 StartY=32.2259 StartZ=0 EndX=-131.61 EndY=32.2259 EndZ=0
    g345: ArcOfCircle CenterX=-131.61 CenterY=30.2259 CenterZ=0 NormalX=0 NormalY=0 NormalZ=1 AngleXU=0 Radius=2 StartAngle=0 EndAngle=1.5708
    g346: LineSegment StartX=-129.61 StartY=30.2259 StartZ=0 EndX=-129.61 EndY=29.2259 EndZ=0
    g347: ArcOfCircle CenterX=-128.11 CenterY=29.2259 CenterZ=0 NormalX=0 NormalY=0 NormalZ=1 AngleXU=0 Radius=1.5 StartAngle=3.14159 EndAngle=4.71239
    g348: LineSegment StartX=-128.11 StartY=27.7259 StartZ=0 EndX=-89.6105 EndY=27.7259 EndZ=0
    g349: ArcOfCircle CenterX=-89.6105 CenterY=25.7259 CenterZ=0 NormalX=0 NormalY=0 NormalZ=1 AngleXU=0 Radius=2 StartAngle=0 EndAngle=1.5708
    g350: LineSegment StartX=-87.6105 StartY=25.7259 StartZ=0 EndX=-87.6105 EndY=22.7259 EndZ=0
    g351: ArcOfCircle CenterX=-85.6105 CenterY=22.7259 CenterZ=0 NormalX=0 NormalY=0 NormalZ=1 AngleXU=0 Radius=2 StartAngle=3.14159 EndAngle=4.71239
    g352: Circle CenterX=-20.1105 CenterY=30.8259 CenterZ=0 NormalX=0 NormalY=0 NormalZ=-1 AngleXU=0 Radius=1.1
    g353: ArcOfCircle CenterX=-28.2141 CenterY=12.1069 CenterZ=0 NormalX=0 NormalY=0 NormalZ=1 AngleXU=0 Radius=3.39682 StartAngle=4.61462 EndAngle=5.86464
    g354: ArcOfCircle CenterX=-79.1115 CenterY=-90.0531 CenterZ=0 NormalX=0 NormalY=0 NormalZ=1 AngleXU=0 Radius=110.97 StartAngle=1.09767 EndAngle=1.62939
    g355: Circle CenterX=-130.61 CenterY=90.2259 CenterZ=0 NormalX=0 NormalY=0 NormalZ=-1 AngleXU=0 Radius=1.1
    g356: Circle CenterX=-43.6105 CenterY=26.2259 CenterZ=0 NormalX=0 NormalY=0 NormalZ=-1 AngleXU=0 Radius=1.1
    g357: Circle CenterX=-129.11 CenterY=33.7259 CenterZ=0 NormalX=0 NormalY=0 NormalZ=-1 AngleXU=0 Radius=1.1
    g358: Circle CenterX=-51.6105 CenterY=80.2259 CenterZ=0 NormalX=0 NormalY=0 NormalZ=-1 AngleXU=0 Radius=1.1
    g359: LineSegment StartX=-89.6105 StartY=29.1259 StartZ=0 EndX=-89.6105 EndY=43.3259 EndZ=0
    g360: LineSegment StartX=-89.6105 StartY=43.3259 StartZ=0 EndX=-107.11 EndY=43.3259 EndZ=0
    g361: LineSegment StartX=-107.11 StartY=43.3259 StartZ=0 EndX=-107.11 EndY=29.1259 EndZ=0
    g362: LineSegment StartX=-107.11 StartY=29.1259 StartZ=0 EndX=-89.6105 EndY=29.1259 EndZ=0
    g363: Circle CenterX=-20.3259 CenterY=76.3525 CenterZ=0 NormalX=0 NormalY=0 NormalZ=1 AngleXU=0 Radius=1.1
    g364: Circle CenterX=-39.4259 CenterY=75.2525 CenterZ=0 NormalX=0 NormalY=0 NormalZ=1 AngleXU=0 Radius=1.1
    g365: Circle CenterX=-42.8259 CenterY=105.852 CenterZ=0 NormalX=0 NormalY=0 NormalZ=1 AngleXU=0 Radius=1.1
    g366: Circle CenterX=-11.3259 CenterY=105.852 CenterZ=0 NormalX=0 NormalY=0 NormalZ=1 AngleXU=0 Radius=1.1
    g367: Circle CenterX=-42.8259 CenterY=58.3525 CenterZ=0 NormalX=0 NormalY=0 NormalZ=1 AngleXU=0 Radius=1.1
    g368: Circle CenterX=-11.3259 CenterY=58.3525 CenterZ=0 NormalX=0 NormalY=0 NormalZ=1 AngleXU=0 Radius=1.1
    g369: ArcOfCircle CenterX=-43.8259 CenterY=106.852 CenterZ=0 NormalX=0 NormalY=0 NormalZ=1 AngleXU=0 Radius=2 StartAngle=1.5708 EndAngle=3.14159
    g370: LineSegment StartX=-43.8259 StartY=108.852 StartZ=0 EndX=-7.32586 EndY=108.852 EndZ=0
    g371: ArcOfCircle CenterX=-7.32586 CenterY=106.852 CenterZ=0 NormalX=0 NormalY=0 NormalZ=1 AngleXU=0 Radius=2 StartAngle=2e-15 EndAngle=1.5708
    g372: LineSegment StartX=-5.32586 StartY=106.852 StartZ=0 EndX=-5.32586 EndY=45.3525 EndZ=0
    g373: ArcOfCircle CenterX=-7.32586 CenterY=45.3525 CenterZ=0 NormalX=0 NormalY=0 NormalZ=1 AngleXU=0 Radius=2 StartAngle=4.71239 EndAngle=6.28319
    g374: ArcOfCircle CenterX=-43.8259 CenterY=57.3525 CenterZ=0 NormalX=0 NormalY=0 NormalZ=1 AngleXU=0 Radius=2 StartAngle=3.14159 EndAngle=4.71239
    g375: LineSegment StartX=-45.8259 StartY=57.3525 StartZ=0 EndX=-45.8259 EndY=106.852 EndZ=0
    g376: GeomPoint X=-45.8259 Y=108.852 Z=0
    g377: GeomPoint X=-5.32586 Y=43.3525 Z=0
    g378: LineSegment StartX=-22.3259 StartY=55.3525 StartZ=0 EndX=-43.8259 EndY=55.3525 EndZ=0
    g379: LineSegment StartX=-7.32586 StartY=43.3525 StartZ=0 EndX=-18.3259 EndY=43.3525 EndZ=0
    g380: LineSegment StartX=-20.3259 StartY=45.3525 StartZ=0 EndX=-20.3259 EndY=53.3525 EndZ=0
    g381: ArcOfCircle CenterX=-18.3259 CenterY=45.3525 CenterZ=0 NormalX=0 NormalY=0 NormalZ=1 AngleXU=0 Radius=2 StartAngle=3.14159 EndAngle=4.71239
    g382: ArcOfCircle CenterX=-22.3259 CenterY=53.3525 CenterZ=0 NormalX=0 NormalY=0 NormalZ=1 AngleXU=0 Radius=2 StartAngle=-9e-16 EndAngle=1.5708
    g383: Circle CenterX=-11.3259 CenterY=86.3525 CenterZ=0 NormalX=0 NormalY=0 NormalZ=1 AngleXU=0 Radius=1.1
    g384: LineSegment StartX=-19.8259 StartY=61.6001 StartZ=0 EndX=-19.8259 EndY=73.1048 EndZ=0
    g385: LineSegment StartX=-19.8259 StartY=73.1048 StartZ=0 EndX=-23.5735 EndY=76.8525 EndZ=0
    g386: LineSegment StartX=-23.5735 StartY=76.8525 StartZ=0 EndX=-35.0782 EndY=76.8525 EndZ=0
    g387: LineSegment StartX=-35.0782 StartY=76.8525 StartZ=0 EndX=-38.8259 EndY=73.1048 EndZ=0
    g388: LineSegment StartX=-38.8259 StartY=73.1048 StartZ=0 EndX=-38.8259 EndY=61.6001 EndZ=0
    g389: LineSegment StartX=-38.8259 StartY=61.6001 StartZ=0 EndX=-35.0782 EndY=57.8525 EndZ=0
    g390: LineSegment StartX=-35.0782 StartY=57.8525 StartZ=0 EndX=-23.5735 EndY=57.8525 EndZ=0
    g391: LineSegment StartX=-23.5735 StartY=57.8525 StartZ=0 EndX=-19.8259 EndY=61.6001 EndZ=0
    g392: LineSegment StartX=-35.0782 StartY=76.8525 StartZ=0 EndX=-23.5735 EndY=57.8525 EndZ=0
    g393: LineSegment StartX=-35.0782 StartY=57.8525 StartZ=0 EndX=-23.5735 EndY=76.8525 EndZ=0
    g394: GeomPoint X=-29.3259 Y=67.3525 Z=0
    g395: LineSegment StartX=-38.3259 StartY=76.3525 StartZ=0 EndX=-38.3259 EndY=58.3525 EndZ=0
    g396: LineSegment StartX=-38.3259 StartY=58.3525 StartZ=0 EndX=-20.3259 EndY=58.3525 EndZ=0
    g397: LineSegment StartX=-20.3259 StartY=58.3525 StartZ=0 EndX=-20.3259 EndY=76.3525 EndZ=0
    g398: LineSegment StartX=-20.3259 StartY=76.3525 StartZ=0 EndX=-38.3259 EndY=76.3525 EndZ=0
    g399: GeomPoint X=-29.3259 Y=67.3525 Z=0
    ... +39 more geometry lines
  constraints (772):
    c: Horizontal(g0)
    c: Coincident(g0,g1)
    c: Vertical(g1)
    c: Coincident(g1,g2)
    c: Horizontal(g2)
    c: Coincident(g2,g3)
    c: Vertical(g3)
    c: Coincident(g3,g0)
    c: Horizontal(g4)
    c: Coincident(g4,g5)
    c: Vertical(g5)
    c: Coincident(g5,g6)
    c: Horizontal(g6)
    c: Coincident(g6,g7)
    c: Vertical(g7)
    c: Coincident(g7,g4)
    c: Horizontal(g8)
    c: Coincident(g8,g9)
    c: Vertical(g9)
    c: Coincident(g9,g10)
    c: Horizontal(g10)
    c: Coincident(g10,g11)
    c: Vertical(g11)
    c: Coincident(g11,g8)
    c: Horizontal(g12)
    c: Coincident(g12,g13)
    c: Vertical(g13)
    c: Coincident(g13,g14)
    c: Horizontal(g14)
    c: Coincident(g14,g15)
    c: Vertical(g15)
    c: Coincident(g15,g12)
    c: Horizontal(g16)
    c: Coincident(g16,g17)
    c: Vertical(g17)
    c: Coincident(g17,g18)
    c: Horizontal(g18)
    c: Coincident(g18,g19)
    c: Vertical(g19)
    c: Coincident(g19,g16)
    c: Horizontal(g20)
    c: Coincident(g20,g21)
    c: Vertical(g21)
    c: Coincident(g21,g22)
    c: Horizontal(g22)
    c: Coincident(g22,g23)
    c: Vertical(g23)
    c: Coincident(g23,g20)
    c: Horizontal(g24)
    c: Coincident(g24,g25)
    c: Vertical(g25)
    c: Coincident(g25,g26)
    c: Horizontal(g26)
    c: Coincident(g26,g27)
    c: Vertical(g27)
    c: Coincident(g27,g24)
    c: Horizontal(g28)
    c: Coincident(g28,g29)
    c: Vertical(g29)
    c: Coincident(g29,g30)
    c: Horizontal(g30)
    c: Coincident(g30,g31)
    c: Vertical(g31)
    c: Coincident(g31,g28)
    c: Horizontal(g32)
    c: Coincident(g32,g33)
    c: Vertical(g33)
    c: Coincident(g33,g34)
    c: Horizontal(g34)
    c: Coincident(g34,g35)
    c: Vertical(g35)
    c: Coincident(g35,g32)
    c: Horizontal(g36)
    c: Coincident(g36,g37)
    c: Vertical(g37)
    c: Coincident(g37,g38)
    c: Horizontal(g38)
    c: Coincident(g38,g39)
    c: Vertical(g39)
    c: Coincident(g39,g36)
    c: Coincident(g40,g41)
    c: Coincident(g41,g42)
    c: Coincident(g42,g43)
    c: Coincident(g43,g40)
    c: Horizontal(g44)
    c: Coincident(g44,g45)
    c: Vertical(g45)
    c: Coincident(g45,g46)
    c: Horizontal(g46)
    c: Coincident(g46,g47)
    c: Vertical(g47)
    c: Coincident(g47,g44)
    c: Coincident(g48,g49)
    c: Coincident(g49,g50)
    c: Coincident(g50,g51)
    c: Coincident(g51,g48)
    c: Horizontal(g52)
    c: Coincident(g52,g53)
    c: Vertical(g53)
    c: Coincident(g53,g54)
    c: Horizontal(g54)
    c: Coincident(g54,g55)
    c: Vertical(g55)
    c: Coincident(g55,g52)
    c: Vertical(g56)
    c: Coincident(g56,g57)
    c: Horizontal(g57)
    c: Coincident(g57,g58)
    c: Vertical(g58)
    c: Coincident(g58,g59)
    c: Horizontal(g59)
    c: Coincident(g59,g56)
    c: Horizontal(g60)
    c: Coincident(g60,g61)
    c: Vertical(g61)
    c: Coincident(g61,g62)
    c: Horizontal(g62)
    c: Coincident(g62,g63)
    c: Vertical(g63)
    c: Coincident(g63,g60)
    c: Horizontal(g64)
    c: Coincident(g64,g65)
    c: Vertical(g65)
    c: Coincident(g65,g66)
    c: Horizontal(g66)
    c: Coincident(g66,g67)
    c: Vertical(g67)
    c: Coincident(g67,g64)
    c: Horizontal(g68)
    c: Coincident(g68,g69)
    c: Vertical(g69)
    c: Coincident(g69,g70)
    c: Horizontal(g70)
    c: Coincident(g70,g71)
    c: Vertical(g71)
    c: Coincident(g71,g68)
    c: Coincident(g72,g73)
    c: Coincident(g73,g74)
    c: Coincident(g74,g75)
    c: Coincident(g75,g76)
    c: Vertical(g76)
    c: Coincident(g76,g77)
    c: Coincident(g77,g78)
    c: Horizontal(g78)
    c: Coincident(g78,g79)
    c: Coincident(g79,g80)
    c: Vertical(g80)
    c: Coincident(g80,g81)
    c: Coincident(g81,g82)
    c: Horizontal(g82)
    c: Coincident(g82,g83)
    c: Coincident(g83,g84)
    c: Vertical(g84)
    c: Coincident(g84,g85)
    c: Coincident(g85,g86)
    c: Horizontal(g86)
    c: Coincident(g86,g87)
    c: Coincident(g87,g88)
    c: Vertical(g88)
    c: Coincident(g88,g89)
    c: Coincident(g89,g90)
    c: Horizontal(g90)
    c: Coincident(g90,g91)
    c: Coincident(g91,g92)
    c: Vertical(g92)
    c: Coincident(g92,g93)
    c: Coincident(g93,g94)
    c: Horizontal(g94)
    c: Coincident(g94,g95)
    c: Coincident(g95,g96)
    c: Vertical(g96)
    c: Coincident(g96,g97)
    c: Coincident(g97,g98)
    c: Horizontal(g98)
    c: Coincident(g98,g99)
    c: Coincident(g99,g100)
    c: Vertical(g100)
    c: Coincident(g100,g101)
    c: Coincident(g101,g102)
    c: Horizontal(g102)
    c: Coincident(g102,g103)
    c: Coincident(g103,g104)
    c: Vertical(g104)
    c: Coincident(g104,g105)
    c: Coincident(g105,g106)
    c: Horizontal(g106)
    c: Coincident(g106,g107)
    c: Coincident(g107,g108)
    c: Vertical(g108)
    c: Coincident(g108,g109)
    c: Vertical(g117)
    c: Coincident(g117,g118)
    c: Horizontal(g118)
    c: Coincident(g118,g119)
    c: Vertical(g119)
    c: Coincident(g119,g120)
    c: Horizontal(g120)
    c: Coincident(g120,g117)
    c: Horizontal(g121)
    c: Coincident(g121,g122)
    c: Vertical(g122)
    c: Coincident(g122,g123)
    c: Horizontal(g123)
    c: Coincident(g123,g124)
    c: Vertical(g124)
    c: Coincident(g124,g121)
    c: Horizontal(g125)
    c: Coincident(g125,g126)
    c: Vertical(g126)
    c: Coincident(g126,g127)
    c: Horizontal(g127)
    c: Coincident(g127,g128)
    c: Vertical(g128)
    c: Coincident(g128,g125)
    c: Horizontal(g129)
    c: Coincident(g129,g130)
    c: Vertical(g130)
    c: Coincident(g130,g131)
    c: Horizontal(g131)
    c: Coincident(g131,g132)
    c: Vertical(g132)
    c: Coincident(g132,g129)
    c: Horizontal(g133)
    c: Coincident(g133,g134)
    c: Vertical(g134)
    c: Coincident(g134,g135)
    c: Horizontal(g135)
    c: Coincident(g135,g136)
    c: Vertical(g136)
    c: Coincident(g136,g133)
    c: Horizontal(g137)
    c: Coincident(g137,g138)
    c: Vertical(g138)
    c: Coincident(g138,g139)
    c: Horizontal(g139)
    c: Coincident(g139,g140)
    c: Vertical(g140)
    c: Coincident(g140,g137)
    c: Horizontal(g141)
    c: Coincident(g141,g142)
    c: Vertical(g142)
    c: Coincident(g142,g143)
    c: Horizontal(g143)
    c: Coincident(g143,g144)
    c: Vertical(g144)
    c: Coincident(g144,g141)
    c: Horizontal(g145)
    c: Coincident(g145,g146)
    c: Vertical(g146)
    c: Coincident(g146,g147)
    c: Horizontal(g147)
    c: Coincident(g147,g148)
    c: Vertical(g148)
    c: Coincident(g148,g145)
    c: Horizontal(g149)
    c: Coincident(g149,g150)
    c: Vertical(g150)
    c: Coincident(g150,g151)
    c: Horizontal(g151)
    c: Coincident(g151,g152)
    c: Vertical(g152)
    c: Coincident(g152,g149)
    c: Horizontal(g153)
    c: Coincident(g153,g154)
    c: Vertical(g154)
    c: Coincident(g154,g155)
    c: Horizontal(g155)
    c: Coincident(g155,g156)
    c: Vertical(g156)
    c: Coincident(g156,g153)
    c: Horizontal(g157)
    c: Coincident(g157,g158)
    c: Vertical(g158)
    c: Coincident(g158,g159)
    c: Horizontal(g159)
    c: Coincident(g159,g160)
    c: Vertical(g160)
    c: Coincident(g160,g157)
    c: Coincident(g161,g162)
    c: Coincident(g162,g163)
    c: Coincident(g163,g164)
    c: Coincident(g164,g161)
    c: Horizontal(g165)
    c: Coincident(g165,g166)
    c: Vertical(g166)
    c: Coincident(g166,g167)
    c: Horizontal(g167)
    c: Coincident(g167,g168)
    c: Vertical(g168)
    c: Coincident(g168,g165)
    c: Coincident(g169,g170)
    c: Coincident(g170,g171)
    c: Coincident(g171,g172)
    c: Coincident(g172,g169)
    c: Horizontal(g173)
    c: Coincident(g173,g174)
    c: Vertical(g174)
    c: Coincident(g174,g175)
    c: Horizontal(g175)
    c: Coincident(g175,g176)
    c: Vertical(g176)
    c: Coincident(g176,g173)
    c: Vertical(g177)
    c: Coincident(g177,g178)
    c: Horizontal(g178)
    c: Coincident(g178,g179)
    c: Vertical(g179)
    c: Coincident(g179,g180)
    c: Horizontal(g180)
    c: Coincident(g180,g177)
    c: Horizontal(g181)
    c: Coincident(g181,g182)
    c: Vertical(g182)
    c: Coincident(g182,g183)
    c: Horizontal(g183)
    c: Coincident(g183,g184)
    c: Vertical(g184)
    c: Coincident(g184,g181)
    c: Horizontal(g185)
    c: Coincident(g185,g186)
    c: Vertical(g186)
    c: Coincident(g186,g187)
    c: Horizontal(g187)
    c: Coincident(g187,g188)
    c: Vertical(g188)
    c: Coincident(g188,g185)
    c: Horizontal(g189)
    c: Coincident(g189,g190)
    c: Vertical(g190)
    c: Coincident(g190,g191)
    c: Horizontal(g191)
    c: Coincident(g191,g192)
    c: Vertical(g192)
    c: Coincident(g192,g189)
    c: Coincident(g193,g194)
    c: Coincident(g194,g195)
    c: Coincident(g195,g196)
    c: Coincident(g196,g197)
    c: Vertical(g197)
    c: Coincident(g197,g198)
    c: Coincident(g198,g199)
    c: Horizontal(g199)
    c: Coincident(g199,g200)
    c: Coincident(g200,g201)
    c: Vertical(g201)
    c: Coincident(g201,g202)
    c: Coincident(g202,g203)
    c: Horizontal(g203)
    c: Coincident(g203,g204)
    c: Coincident(g204,g205)
    c: Vertical(g205)
    c: Coincident(g205,g206)
    c: Coincident(g206,g207)
    c: Horizontal(g207)
    c: Coincident(g207,g208)
    c: Coincident(g208,g209)
    c: Vertical(g209)
    c: Coincident(g209,g210)
    c: Coincident(g210,g211)
    c: Horizontal(g211)
    c: Coincident(g211,g212)
    c: Coincident(g212,g213)
    c: Vertical(g213)
    c: Coincident(g213,g214)
    c: Coincident(g214,g215)
    c: Horizontal(g215)
    c: Coincident(g215,g216)
    c: Coincident(g216,g217)
    c: Vertical(g217)
    c: Coincident(g217,g218)
    c: Coincident(g218,g219)
    c: Horizontal(g219)
    c: Coincident(g219,g220)
    c: Coincident(g220,g221)
    c: Vertical(g221)
    c: Coincident(g221,g222)
    c: Coincident(g222,g223)
    c: Horizontal(g223)
    c: Coincident(g223,g224)
    c: Coincident(g224,g225)
    c: Vertical(g225)
    c: Coincident(g225,g226)
    c: Coincident(g226,g227)
    c: Horizontal(g227)
    c: Coincident(g227,g228)
    c: Coincident(g228,g229)
    c: Vertical(g229)
    c: Coincident(g229,g230)
    c: Vertical(g238)
    c: Coincident(g238,g239)
    c: Horizontal(g239)
    c: Coincident(g239,g240)
    c: Vertical(g240)
    c: Coincident(g240,g241)
    c: Horizontal(g241)
    c: Coincident(g241,g238)
    c: Horizontal(g242)
    c: Coincident(g242,g243)
    c: Vertical(g243)
    c: Coincident(g243,g244)
    c: Horizontal(g244)
    c: Coincident(g244,g245)
    c: Vertical(g245)
    c: Coincident(g245,g242)
    c: Horizontal(g246)
    c: Coincident(g246,g247)
    c: Vertical(g247)
    c: Coincident(g247,g248)
    c: Horizontal(g248)
    c: Coincident(g248,g249)
    c: Vertical(g249)
    c: Coincident(g249,g246)
    c: Horizontal(g250)
    c: Coincident(g250,g251)
    c: Vertical(g251)
    c: Coincident(g251,g252)
    c: Horizontal(g252)
    c: Coincident(g252,g253)
    c: Vertical(g253)
    c: Coincident(g253,g250)
    c: Horizontal(g254)
    c: Coincident(g254,g255)
    c: Vertical(g255)
    c: Coincident(g255,g256)
    c: Horizontal(g256)
    c: Coincident(g256,g257)
    c: Vertical(g257)
    c: Coincident(g257,g254)
    c: Horizontal(g258)
    c: Coincident(g258,g259)
    c: Vertical(g259)
    c: Coincident(g259,g260)
    c: Horizontal(g260)
    c: Coincident(g260,g261)
    c: Vertical(g261)
    c: Coincident(g261,g258)
    c: Horizontal(g262)
    c: Coincident(g262,g263)
    c: Vertical(g263)
    c: Coincident(g263,g264)
    c: Horizontal(g264)
    c: Coincident(g264,g265)
    c: Vertical(g265)
    c: Coincident(g265,g262)
    c: Horizontal(g266)
    c: Coincident(g266,g267)
    c: Vertical(g267)
    c: Coincident(g267,g268)
    c: Horizontal(g268)
    c: Coincident(g268,g269)
    c: Vertical(g269)
    c: Coincident(g269,g266)
    c: Horizontal(g270)
    c: Coincident(g270,g271)
    c: Vertical(g271)
    c: Coincident(g271,g272)
    c: Horizontal(g272)
    c: Coincident(g272,g273)
    c: Vertical(g273)
    c: Coincident(g273,g270)
    c: Horizontal(g274)
    c: Coincident(g274,g275)
    c: Vertical(g275)
    c: Coincident(g275,g276)
    c: Horizontal(g276)
    c: Coincident(g276,g277)
    c: Vertical(g277)
    c: Coincident(g277,g274)
    c: Horizontal(g278)
    c: Coincident(g278,g279)
    c: Vertical(g279)
    c: Coincident(g279,g280)
    c: Horizontal(g280)
    c: Coincident(g280,g281)
    c: Vertical(g281)
    c: Coincident(g281,g278)
    c: Coincident(g282,g283)
    c: Coincident(g283,g284)
    c: Coincident(g284,g285)
    c: Coincident(g285,g282)
    c: Horizontal(g286)
    c: Coincident(g286,g287)
    c: Vertical(g287)
    c: Coincident(g287,g288)
    c: Horizontal(g288)
    c: Coincident(g288,g289)
    c: Vertical(g289)
    c: Coincident(g289,g286)
    c: Coincident(g290,g291)
    c: Coincident(g291,g292)
    c: Coincident(g292,g293)
    c: Coincident(g293,g290)
    c: Horizontal(g294)
    c: Coincident(g294,g295)
    c: Vertical(g295)
    c: Coincident(g295,g296)
    c: Horizontal(g296)
    c: Coincident(g296,g297)
    c: Vertical(g297)
    c: Coincident(g297,g294)
    c: Vertical(g298)
    c: Coincident(g298,g299)
    c: Horizontal(g299)
    c: Coincident(g299,g300)
    c: Vertical(g300)
    c: Coincident(g300,g301)
    c: Horizontal(g301)
    c: Coincident(g301,g298)
    c: Horizontal(g302)
    c: Coincident(g302,g303)
    c: Vertical(g303)
    c: Coincident(g303,g304)
    c: Horizontal(g304)
    c: Coincident(g304,g305)
    c: Vertical(g305)
    c: Coincident(g305,g302)
    c: Horizontal(g306)
    c: Coincident(g306,g307)
    c: Vertical(g307)
    c: Coincident(g307,g308)
    c: Horizontal(g308)
    c: Coincident(g308,g309)
    c: Vertical(g309)
    c: Coincident(g309,g306)
    c: Horizontal(g310)
    c: Coincident(g310,g311)
    c: Vertical(g311)
    c: Coincident(g311,g312)
    c: Horizontal(g312)
    c: Coincident(g312,g313)
    c: Vertical(g313)
    c: Coincident(g313,g310)
    c: Coincident(g314,g315)
    c: Coincident(g315,g316)
    c: Coincident(g316,g317)
    c: Coincident(g317,g318)
    c: Vertical(g318)
    c: Coincident(g318,g319)
    c: Coincident(g319,g320)
    c: Horizontal(g320)
    c: Coincident(g320,g321)
    c: Coincident(g321,g322)
    c: Vertical(g322)
    c: Coincident(g322,g323)
    c: Coincident(g323,g324)
    c: Horizontal(g324)
    c: Coincident(g324,g325)
    c: Coincident(g325,g326)
    c: Vertical(g326)
    c: Coincident(g326,g327)
    c: Coincident(g327,g328)
    c: Horizontal(g328)
    c: Coincident(g328,g329)
    c: Coincident(g329,g330)
    c: Vertical(g330)
    c: Coincident(g330,g331)
    c: Coincident(g331,g332)
    c: Horizontal(g332)
    c: Coincident(g332,g333)
    c: Coincident(g333,g334)
    c: Vertical(g334)
    c: Coincident(g334,g335)
    c: Coincident(g335,g336)
    c: Horizontal(g336)
    c: Coincident(g336,g337)
    c: Coincident(g337,g338)
    c: Vertical(g338)
    c: Coincident(g338,g339)
    c: Coincident(g339,g340)
    c: Horizontal(g340)
    c: Coincident(g340,g341)
    c: Coincident(g341,g342)
    c: Vertical(g342)
    c: Coincident(g342,g343)
    c: Coincident(g343,g344)
    c: Horizontal(g344)
    c: Coincident(g344,g345)
    c: Coincident(g345,g346)
    c: Vertical(g346)
    c: Coincident(g346,g347)
    c: Coincident(g347,g348)
    c: Horizontal(g348)
    c: Coincident(g348,g349)
    c: Coincident(g349,g350)
    c: Vertical(g350)
    c: Coincident(g350,g351)
    c: Vertical(g359)
    c: Coincident(g359,g360)
    c: Horizontal(g360)
    c: Coincident(g360,g361)
    c: Vertical(g361)
    c: Coincident(g361,g362)
    c: Horizontal(g362)
    c: Coincident(g362,g359)
    c: Equal(g365,g366)
    c: Equal(g365,g367)
    c: Equal(g365,g368)
    c: Vertical(g365,g367)
    c: Vertical(g366,g368)
    c: Horizontal(g365,g366)
    c: Horizontal(g367,g368)
    c: Tangent(g369,g370) = 1.5708
    c: Tangent(g370,g371) = 1.5708
    c: Tangent(g371,g372) = 1.5708
    c: Tangent(g372,g373) = 1.5708
    c: Tangent(g373,g379) = 1.5708
    c: Tangent(g378,g374) = 1.5708
    c: Tangent(g374,g375) = 1.5708
    c: Tangent(g375,g369) = 1.5708
    c: Horizontal(g370)
    c: Vertical(g372)
    c: Vertical(g375)
    c: Equal(g369,g371)
    c: Equal(g371,g373)
    c: PointOnObject(g376,g370)
    c: PointOnObject(g376,g375)
    c: PointOnObject(g377,g372)
    c: DistanceX(g369,g365) = 3
    c: DistanceY(g365,g369) = 3
    c: DistanceX(g366,g371) = 6
    c: Horizontal(g378)
    c: Distance(g367,g378) = 3
    c: PointOnObject(g377,g379)
    c: Horizontal(g379)
    c: Vertical(g380)
    c: Tangent(g379,g381) = 1.5708
    c: Tangent(g380,g381) = 1.5708
    c: Tangent(g378,g382) = -1.5708
    c: Tangent(g380,g382) = -1.5708
    c: Equal(g382,g381)
    c: Equal(g373,g374)
    c: DistanceY(g373,g368) = 15
    c: Equal(g366,g383)
    c: Diameter(g383) = 2.2
    c: Vertical(g383,g366)
    c: DistanceY(g383,g366) = 19.5
    c: Equal(g387,g389)
    c: Equal(g389,g391)
    c: Equal(g391,g385)
    c: Coincident(g386,g387)
    c: Coincident(g385,g386)
    c: Coincident(g384,g385)
    c: Coincident(g384,g391)
    c: Coincident(g390,g391)
    c: Coincident(g389,g390)
    c: Coincident(g388,g389)
    c: Coincident(g387,g388)
    c: Equal(g386,g390)
    c: Equal(g390,g388)
    c: Equal(g388,g384)
    c: Horizontal(g386)
    c: Horizontal(g390)
    c: Vertical(g388)
    c: Vertical(g384)
    c: Distance(g387) = 5.3
    c: DistanceY(g390,g385) = 19
    c: Coincident(g392,g386)
    c: Coincident(g392,g390)
    c: Coincident(g393,g389)
    c: Coincident(g393,g385)
    c: PointOnObject(g394,g393)
    c: PointOnObject(g394,g392)
    c: Coincident(g395,g396)
    c: Coincident(g396,g397)
    c: Coincident(g397,g398)
    c: Coincident(g398,g395)
    c: Horizontal(g396)
    c: Horizontal(g398)
    c: Vertical(g395)
    c: Vertical(g397)
    c: Symmetric(g396,g395,g399)
    c: Coincident(g394,g399)
    c: Equal(g397,g398)
    c: DistanceY(g396,g397) = 18
    c: Coincident(g400,g395)
    c: Horizontal(g400)
    c: Equal(g364,g363)
    c: Tangent(g364,g395)
    c: Tangent(g364,g400)
    c: Coincident(g363,g397)
    c: Angle(g386,g385) = 2.35619
    c: Angle(g384,g391) = 2.35619
    c: Angle(g389,g388) = 2.35619
    c: Angle(g388,g387) = 2.35619  'aa'
    c: Distance(g364,g363) = 19.1316
    c: Distance(g384,g384) = 11.5047
    c: Distance(g400) = 2.63
    c: DistanceX(g374,g388) = 7
    c: DistanceY(g374,g394) = 12
    c: Equal(g403,g404)
    c: Equal(g403,g405)
    c: Equal(g403,g406)
    c: Tangent(g407,g408) = -1.5708
    c: Tangent(g408,g409) = -1.5708
    c: Tangent(g409,g410) = -1.5708
    c: Tangent(g410,g411) = -1.5708
    c: Tangent(g411,g417) = -1.5708
    c: Tangent(g416,g412) = -1.5708
    c: Tangent(g412,g413) = -1.5708
    c: Tangent(g413,g407) = -1.5708
    c: Horizontal(g408)
    c: Vertical(g410)
    c: Vertical(g413)
    c: Equal(g407,g409)
    c: Equal(g409,g411)
    c: PointOnObject(g414,g408)
    c: PointOnObject(g414,g413)
    c: PointOnObject(g415,g410)
    c: Horizontal(g416)
    c: Distance(g405,g416) = 3
    c: PointOnObject(g415,g417)
    c: Horizontal(g417)
    c: Vertical(g418)
    c: Tangent(g417,g419) = -1.5708
    c: Tangent(g418,g419) = -1.5708
    c: Tangent(g416,g420) = 1.5708
    c: Tangent(g418,g420) = 1.5708
    c: Equal(g420,g419)
    c: Equal(g411,g412)
    c: Equal(g404,g421)
    c: Diameter(g421) = 2.2
    c: Equal(g425,g427)
    c: Equal(g427,g429)
    c: Equal(g429,g423)
    c: Coincident(g424,g425)
    c: Coincident(g423,g424)
    c: Coincident(g422,g423)
    c: Coincident(g422,g429)
    c: Coincident(g428,g429)
    c: Coincident(g427,g428)
    c: Coincident(g426,g427)
    c: Coincident(g425,g426)
    c: Equal(g424,g428)
    c: Equal(g428,g426)
    c: Equal(g426,g422)
    c: Horizontal(g424)
    c: Horizontal(g428)
    c: Vertical(g426)
    c: Vertical(g422)
    c: Distance(g425) = 5.3
    c: Coincident(g430,g424)
    c: Coincident(g430,g428)
    c: Coincident(g431,g427)
    c: Coincident(g431,g423)
    c: PointOnObject(g432,g431)
    c: PointOnObject(g432,g430)
    c: Coincident(g433,g434)
    c: Coincident(g434,g435)
    c: Coincident(g435,g436)
    c: Coincident(g436,g433)
    c: Horizontal(g434)
    c: Horizontal(g436)
    c: Vertical(g433)
    c: Vertical(g435)
    c: Symmetric(g434,g433,g437)
    c: Coincident(g432,g437)
    c: Equal(g435,g436)
    c: Coincident(g438,g433)
    c: Horizontal(g438)
    c: Equal(g402,g401)
    c: Tangent(g402,g433)
    c: Tangent(g402,g438)
    c: Coincident(g401,g435)
    c: Angle(g424,g423) = -2.35619
    c: Angle(g422,g429) = -2.35619
    c: Angle(g427,g426) = -2.35619
    c: Angle(g426,g425) = -2.35619  'aa'
    c: Distance(g402,g401) = 19.1316
    c: Distance(g422,g422) = 11.5047
    c: Distance(g438) = 2.63
    c: DistanceX(g378,g378) = 21.5
    c: DistanceY(g378,g390) = 2.5
